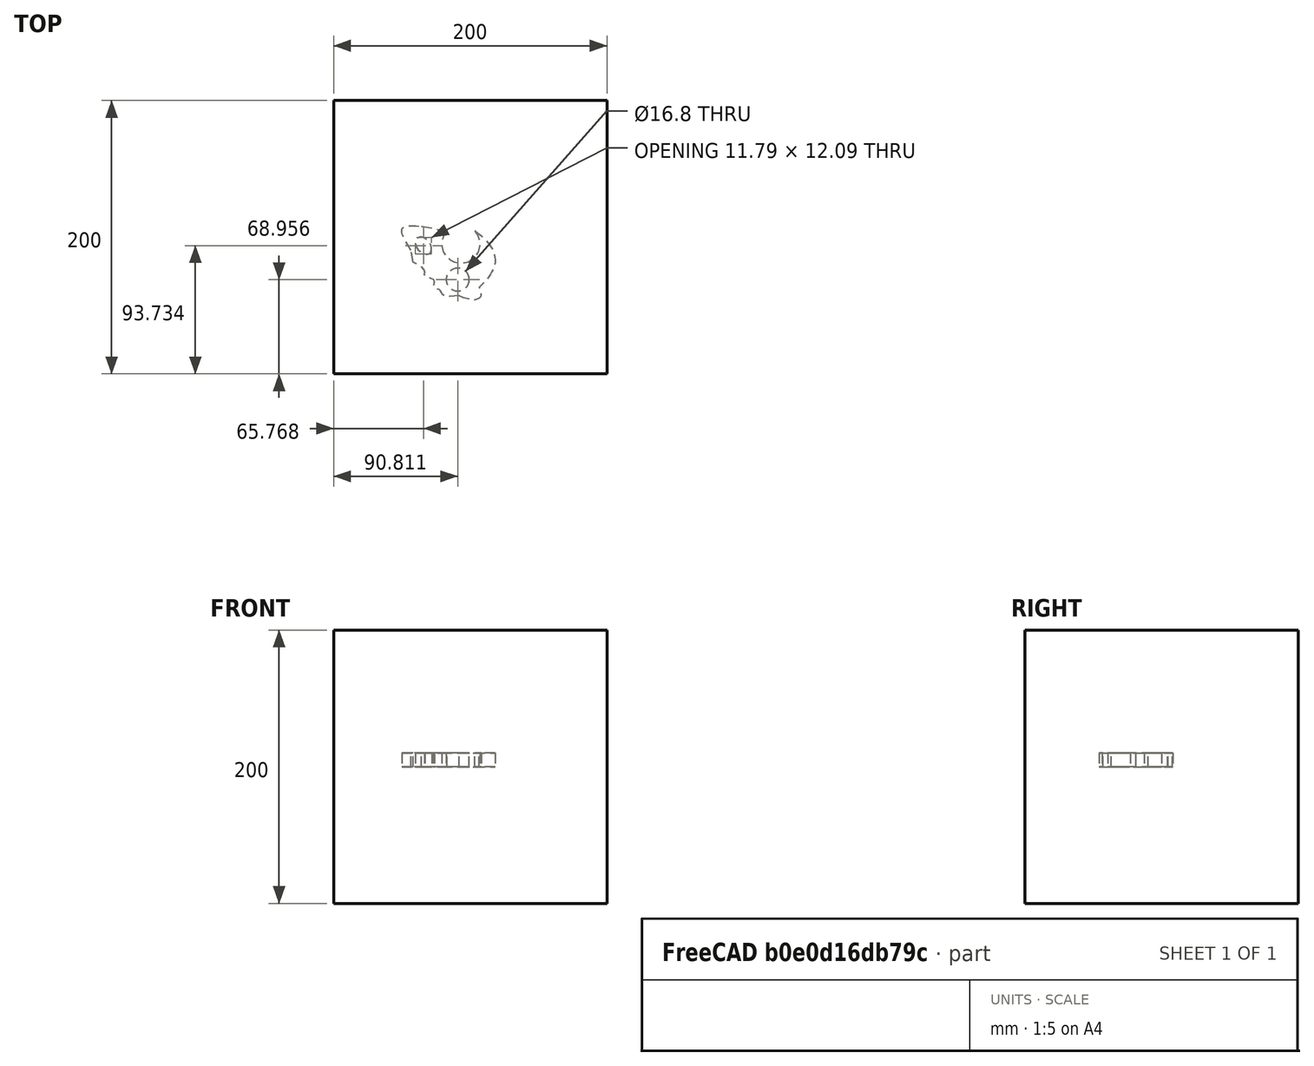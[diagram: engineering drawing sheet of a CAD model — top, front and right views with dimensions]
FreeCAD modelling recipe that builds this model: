
FCSTD DOCUMENT  (FreeCAD 1.0R39109 (Git))
Label: extrudeAllShapes
License: All rights reserved
LicenseURL: http://en.wikipedia.org/wiki/All_rights_reserved
objects: App::DocumentObjectGroupPython×1248, App::Part×2, Part::FeaturePython×1, Sketcher::SketchObject×1, Part::Extrusion×1
note: 4 computed .brp shape members not serialized (recipe doc carries the construction recipe); baked Part::Feature solids carry a one-line shape summary decoded from their .brp

FEATURE [App::DocumentObjectGroupPython] HALFPI  # scripted group (container) (typed FeaturePython)
  name = HALFPI
  value = pi/2.
FEATURE [App::DocumentObjectGroupPython] PI  # scripted group (container) (typed FeaturePython)
  name = PI
  value = 1.*pi
FEATURE [App::DocumentObjectGroupPython] TWOPI  # scripted group (container) (typed FeaturePython)
  name = TWOPI
  value = 2.*pi
FEATURE [App::DocumentObjectGroupPython] Constants  # scripted group (container) (typed FeaturePython)
  Group = -> [HALFPI,PI,TWOPI]
FEATURE [App::DocumentObjectGroupPython] Variables  # scripted group (container) (typed FeaturePython)
FEATURE [App::DocumentObjectGroupPython] Quantities  # scripted group (container) (typed FeaturePython)
FEATURE [App::DocumentObjectGroupPython] Isotopes  # scripted group (container) (typed FeaturePython)
FEATURE [App::DocumentObjectGroupPython] Elements  # scripted group (container) (typed FeaturePython)
FEATURE [App::DocumentObjectGroupPython] G4Isotopes  # scripted group (container) (typed FeaturePython)
FEATURE [App::DocumentObjectGroupPython] H_element  # scripted group (container) (typed FeaturePython)
  Z = 1
  atom_value = 1.008
  formula = H
  name = H_element
FEATURE [App::DocumentObjectGroupPython] He_element  # scripted group (container) (typed FeaturePython)
  Z = 2
  atom_value = 4.0026
  formula = He
  name = He_element
FEATURE [App::DocumentObjectGroupPython] Li_element  # scripted group (container) (typed FeaturePython)
  Z = 3
  atom_value = 6.94
  formula = Li
  name = Li_element
FEATURE [App::DocumentObjectGroupPython] Be_element  # scripted group (container) (typed FeaturePython)
  Z = 4
  atom_value = 9.01218
  formula = Be
  name = Be_element
FEATURE [App::DocumentObjectGroupPython] B_element  # scripted group (container) (typed FeaturePython)
  Z = 5
  atom_value = 10.81
  formula = B
  name = B_element
FEATURE [App::DocumentObjectGroupPython] C_element  # scripted group (container) (typed FeaturePython)
  Z = 6
  atom_value = 12.011
  formula = C
  name = C_element
FEATURE [App::DocumentObjectGroupPython] N_element  # scripted group (container) (typed FeaturePython)
  Z = 7
  atom_value = 14.007
  formula = N
  name = N_element
FEATURE [App::DocumentObjectGroupPython] O_element  # scripted group (container) (typed FeaturePython)
  Z = 8
  atom_value = 15.999
  formula = O
  name = O_element
FEATURE [App::DocumentObjectGroupPython] F_element  # scripted group (container) (typed FeaturePython)
  Z = 9
  atom_value = 18.9984
  formula = F
  name = F_element
FEATURE [App::DocumentObjectGroupPython] Ne_element  # scripted group (container) (typed FeaturePython)
  Z = 10
  atom_value = 20.1797
  formula = Ne
  name = Ne_element
FEATURE [App::DocumentObjectGroupPython] Na_element  # scripted group (container) (typed FeaturePython)
  Z = 11
  atom_value = 22.9898
  formula = Na
  name = Na_element
FEATURE [App::DocumentObjectGroupPython] Mg_element  # scripted group (container) (typed FeaturePython)
  Z = 12
  atom_value = 24.305
  formula = Mg
  name = Mg_element
FEATURE [App::DocumentObjectGroupPython] Al_element  # scripted group (container) (typed FeaturePython)
  Z = 13
  atom_value = 26.9815
  formula = Al
  name = Al_element
FEATURE [App::DocumentObjectGroupPython] Si_element  # scripted group (container) (typed FeaturePython)
  Z = 14
  atom_value = 28.085
  formula = Si
  name = Si_element
FEATURE [App::DocumentObjectGroupPython] P_element  # scripted group (container) (typed FeaturePython)
  Z = 15
  atom_value = 30.9738
  formula = P
  name = P_element
FEATURE [App::DocumentObjectGroupPython] S_element  # scripted group (container) (typed FeaturePython)
  Z = 16
  atom_value = 32.06
  formula = S
  name = S_element
FEATURE [App::DocumentObjectGroupPython] Cl_element  # scripted group (container) (typed FeaturePython)
  Z = 17
  atom_value = 35.45
  formula = Cl
  name = Cl_element
FEATURE [App::DocumentObjectGroupPython] Ar_element  # scripted group (container) (typed FeaturePython)
  Z = 18
  atom_value = 39.95
  formula = Ar
  name = Ar_element
FEATURE [App::DocumentObjectGroupPython] K_element  # scripted group (container) (typed FeaturePython)
  Z = 19
  atom_value = 39.0983
  formula = K
  name = K_element
FEATURE [App::DocumentObjectGroupPython] Ca_element  # scripted group (container) (typed FeaturePython)
  Z = 20
  atom_value = 40.078
  formula = Ca
  name = Ca_element
FEATURE [App::DocumentObjectGroupPython] Sc_element  # scripted group (container) (typed FeaturePython)
  Z = 21
  atom_value = 44.9559
  formula = Sc
  name = Sc_element
FEATURE [App::DocumentObjectGroupPython] Ti_element  # scripted group (container) (typed FeaturePython)
  Z = 22
  atom_value = 47.867
  formula = Ti
  name = Ti_element
FEATURE [App::DocumentObjectGroupPython] V_element  # scripted group (container) (typed FeaturePython)
  Z = 23
  atom_value = 50.9415
  formula = V
  name = V_element
FEATURE [App::DocumentObjectGroupPython] Cr_element  # scripted group (container) (typed FeaturePython)
  Z = 24
  atom_value = 51.9961
  formula = Cr
  name = Cr_element
FEATURE [App::DocumentObjectGroupPython] Mn_element  # scripted group (container) (typed FeaturePython)
  Z = 25
  atom_value = 54.938
  formula = Mn
  name = Mn_element
FEATURE [App::DocumentObjectGroupPython] Fe_element  # scripted group (container) (typed FeaturePython)
  Z = 26
  atom_value = 55.845
  formula = Fe
  name = Fe_element
FEATURE [App::DocumentObjectGroupPython] Co_element  # scripted group (container) (typed FeaturePython)
  Z = 27
  atom_value = 58.9332
  formula = Co
  name = Co_element
FEATURE [App::DocumentObjectGroupPython] Ni_element  # scripted group (container) (typed FeaturePython)
  Z = 28
  atom_value = 58.6934
  formula = Ni
  name = Ni_element
FEATURE [App::DocumentObjectGroupPython] Cu_element  # scripted group (container) (typed FeaturePython)
  Z = 29
  atom_value = 63.546
  formula = Cu
  name = Cu_element
FEATURE [App::DocumentObjectGroupPython] Zn_element  # scripted group (container) (typed FeaturePython)
  Z = 30
  atom_value = 65.38
  formula = Zn
  name = Zn_element
FEATURE [App::DocumentObjectGroupPython] Ga_element  # scripted group (container) (typed FeaturePython)
  Z = 31
  atom_value = 69.723
  formula = Ga
  name = Ga_element
FEATURE [App::DocumentObjectGroupPython] Ge_element  # scripted group (container) (typed FeaturePython)
  Z = 32
  atom_value = 72.63
  formula = Ge
  name = Ge_element
FEATURE [App::DocumentObjectGroupPython] As_element  # scripted group (container) (typed FeaturePython)
  Z = 33
  atom_value = 74.9216
  formula = As
  name = As_element
FEATURE [App::DocumentObjectGroupPython] Se_element  # scripted group (container) (typed FeaturePython)
  Z = 34
  atom_value = 78.971
  formula = Se
  name = Se_element
FEATURE [App::DocumentObjectGroupPython] Br_element  # scripted group (container) (typed FeaturePython)
  Z = 35
  atom_value = 79.904
  formula = Br
  name = Br_element
FEATURE [App::DocumentObjectGroupPython] Kr_element  # scripted group (container) (typed FeaturePython)
  Z = 36
  atom_value = 83.798
  formula = Kr
  name = Kr_element
FEATURE [App::DocumentObjectGroupPython] Rb_element  # scripted group (container) (typed FeaturePython)
  Z = 37
  atom_value = 85.4678
  formula = Rb
  name = Rb_element
FEATURE [App::DocumentObjectGroupPython] Sr_element  # scripted group (container) (typed FeaturePython)
  Z = 38
  atom_value = 87.62
  formula = Sr
  name = Sr_element
FEATURE [App::DocumentObjectGroupPython] Y_element  # scripted group (container) (typed FeaturePython)
  Z = 39
  atom_value = 88.9058
  formula = Y
  name = Y_element
FEATURE [App::DocumentObjectGroupPython] Zr_element  # scripted group (container) (typed FeaturePython)
  Z = 40
  atom_value = 91.224
  formula = Zr
  name = Zr_element
FEATURE [App::DocumentObjectGroupPython] Nb_element  # scripted group (container) (typed FeaturePython)
  Z = 41
  atom_value = 92.9064
  formula = Nb
  name = Nb_element
FEATURE [App::DocumentObjectGroupPython] Mo_element  # scripted group (container) (typed FeaturePython)
  Z = 42
  atom_value = 95.95
  formula = Mo
  name = Mo_element
FEATURE [App::DocumentObjectGroupPython] Tc_element  # scripted group (container) (typed FeaturePython)
  Z = 43
  atom_value = 97
  formula = Tc
  name = Tc_element
FEATURE [App::DocumentObjectGroupPython] Ru_element  # scripted group (container) (typed FeaturePython)
  Z = 44
  atom_value = 101.07
  formula = Ru
  name = Ru_element
FEATURE [App::DocumentObjectGroupPython] Rh_element  # scripted group (container) (typed FeaturePython)
  Z = 45
  atom_value = 102.905
  formula = Rh
  name = Rh_element
FEATURE [App::DocumentObjectGroupPython] Pd_element  # scripted group (container) (typed FeaturePython)
  Z = 46
  atom_value = 106.42
  formula = Pd
  name = Pd_element
FEATURE [App::DocumentObjectGroupPython] Ag_element  # scripted group (container) (typed FeaturePython)
  Z = 47
  atom_value = 107.868
  formula = Ag
  name = Ag_element
FEATURE [App::DocumentObjectGroupPython] Cd_element  # scripted group (container) (typed FeaturePython)
  Z = 48
  atom_value = 112.414
  formula = Cd
  name = Cd_element
FEATURE [App::DocumentObjectGroupPython] In_element  # scripted group (container) (typed FeaturePython)
  Z = 49
  atom_value = 114.818
  formula = In
  name = In_element
FEATURE [App::DocumentObjectGroupPython] Sn_element  # scripted group (container) (typed FeaturePython)
  Z = 50
  atom_value = 118.71
  formula = Sn
  name = Sn_element
FEATURE [App::DocumentObjectGroupPython] Sb_element  # scripted group (container) (typed FeaturePython)
  Z = 51
  atom_value = 121.76
  formula = Sb
  name = Sb_element
FEATURE [App::DocumentObjectGroupPython] Te_element  # scripted group (container) (typed FeaturePython)
  Z = 52
  atom_value = 127.6
  formula = Te
  name = Te_element
FEATURE [App::DocumentObjectGroupPython] I_element  # scripted group (container) (typed FeaturePython)
  Z = 53
  atom_value = 126.904
  formula = I
  name = I_element
FEATURE [App::DocumentObjectGroupPython] Xe_element  # scripted group (container) (typed FeaturePython)
  Z = 54
  atom_value = 131.293
  formula = Xe
  name = Xe_element
FEATURE [App::DocumentObjectGroupPython] Cs_element  # scripted group (container) (typed FeaturePython)
  Z = 55
  atom_value = 132.905
  formula = Cs
  name = Cs_element
FEATURE [App::DocumentObjectGroupPython] Ba_element  # scripted group (container) (typed FeaturePython)
  Z = 56
  atom_value = 137.327
  formula = Ba
  name = Ba_element
FEATURE [App::DocumentObjectGroupPython] La_element  # scripted group (container) (typed FeaturePython)
  Z = 57
  atom_value = 138.905
  formula = La
  name = La_element
FEATURE [App::DocumentObjectGroupPython] Ce_element  # scripted group (container) (typed FeaturePython)
  Z = 58
  atom_value = 140.116
  formula = Ce
  name = Ce_element
FEATURE [App::DocumentObjectGroupPython] Pr_element  # scripted group (container) (typed FeaturePython)
  Z = 59
  atom_value = 140.908
  formula = Pr
  name = Pr_element
FEATURE [App::DocumentObjectGroupPython] Nd_element  # scripted group (container) (typed FeaturePython)
  Z = 60
  atom_value = 144.242
  formula = Nd
  name = Nd_element
FEATURE [App::DocumentObjectGroupPython] Pm_element  # scripted group (container) (typed FeaturePython)
  Z = 61
  atom_value = 145
  formula = Pm
  name = Pm_element
FEATURE [App::DocumentObjectGroupPython] Sm_element  # scripted group (container) (typed FeaturePython)
  Z = 62
  atom_value = 150.36
  formula = Sm
  name = Sm_element
FEATURE [App::DocumentObjectGroupPython] Eu_element  # scripted group (container) (typed FeaturePython)
  Z = 63
  atom_value = 151.964
  formula = Eu
  name = Eu_element
FEATURE [App::DocumentObjectGroupPython] Gd_element  # scripted group (container) (typed FeaturePython)
  Z = 64
  atom_value = 157.25
  formula = Gd
  name = Gd_element
FEATURE [App::DocumentObjectGroupPython] Tb_element  # scripted group (container) (typed FeaturePython)
  Z = 65
  atom_value = 158.925
  formula = Tb
  name = Tb_element
FEATURE [App::DocumentObjectGroupPython] Dy_element  # scripted group (container) (typed FeaturePython)
  Z = 66
  atom_value = 162.5
  formula = Dy
  name = Dy_element
FEATURE [App::DocumentObjectGroupPython] Ho_element  # scripted group (container) (typed FeaturePython)
  Z = 67
  atom_value = 164.93
  formula = Ho
  name = Ho_element
FEATURE [App::DocumentObjectGroupPython] Er_element  # scripted group (container) (typed FeaturePython)
  Z = 68
  atom_value = 167.259
  formula = Er
  name = Er_element
FEATURE [App::DocumentObjectGroupPython] Tm_element  # scripted group (container) (typed FeaturePython)
  Z = 69
  atom_value = 168.934
  formula = Tm
  name = Tm_element
FEATURE [App::DocumentObjectGroupPython] Yb_element  # scripted group (container) (typed FeaturePython)
  Z = 70
  atom_value = 173.045
  formula = Yb
  name = Yb_element
FEATURE [App::DocumentObjectGroupPython] Lu_element  # scripted group (container) (typed FeaturePython)
  Z = 71
  atom_value = 174.967
  formula = Lu
  name = Lu_element
FEATURE [App::DocumentObjectGroupPython] Hf_element  # scripted group (container) (typed FeaturePython)
  Z = 72
  atom_value = 178.49
  formula = Hf
  name = Hf_element
FEATURE [App::DocumentObjectGroupPython] Ta_element  # scripted group (container) (typed FeaturePython)
  Z = 73
  atom_value = 180.948
  formula = Ta
  name = Ta_element
FEATURE [App::DocumentObjectGroupPython] W_element  # scripted group (container) (typed FeaturePython)
  Z = 74
  atom_value = 183.84
  formula = W
  name = W_element
FEATURE [App::DocumentObjectGroupPython] Re_element  # scripted group (container) (typed FeaturePython)
  Z = 75
  atom_value = 186.207
  formula = Re
  name = Re_element
FEATURE [App::DocumentObjectGroupPython] Os_element  # scripted group (container) (typed FeaturePython)
  Z = 76
  atom_value = 190.23
  formula = Os
  name = Os_element
FEATURE [App::DocumentObjectGroupPython] Ir_element  # scripted group (container) (typed FeaturePython)
  Z = 77
  atom_value = 192.217
  formula = Ir
  name = Ir_element
FEATURE [App::DocumentObjectGroupPython] Pt_element  # scripted group (container) (typed FeaturePython)
  Z = 78
  atom_value = 195.084
  formula = Pt
  name = Pt_element
FEATURE [App::DocumentObjectGroupPython] Au_element  # scripted group (container) (typed FeaturePython)
  Z = 79
  atom_value = 196.967
  formula = Au
  name = Au_element
FEATURE [App::DocumentObjectGroupPython] Hg_element  # scripted group (container) (typed FeaturePython)
  Z = 80
  atom_value = 200.592
  formula = Hg
  name = Hg_element
FEATURE [App::DocumentObjectGroupPython] Tl_element  # scripted group (container) (typed FeaturePython)
  Z = 81
  atom_value = 204.38
  formula = Tl
  name = Tl_element
FEATURE [App::DocumentObjectGroupPython] Pb_element  # scripted group (container) (typed FeaturePython)
  Z = 82
  atom_value = 207.2
  formula = Pb
  name = Pb_element
FEATURE [App::DocumentObjectGroupPython] Bi_element  # scripted group (container) (typed FeaturePython)
  Z = 83
  atom_value = 208.98
  formula = Bi
  name = Bi_element
FEATURE [App::DocumentObjectGroupPython] Po_element  # scripted group (container) (typed FeaturePython)
  Z = 84
  atom_value = 209
  formula = Po
  name = Po_element
FEATURE [App::DocumentObjectGroupPython] At_element  # scripted group (container) (typed FeaturePython)
  Z = 85
  atom_value = 210
  formula = At
  name = At_element
FEATURE [App::DocumentObjectGroupPython] Rn_element  # scripted group (container) (typed FeaturePython)
  Z = 86
  atom_value = 222
  formula = Rn
  name = Rn_element
FEATURE [App::DocumentObjectGroupPython] Fr_element  # scripted group (container) (typed FeaturePython)
  Z = 87
  atom_value = 223
  formula = Fr
  name = Fr_element
FEATURE [App::DocumentObjectGroupPython] Ra_element  # scripted group (container) (typed FeaturePython)
  Z = 88
  atom_value = 226
  formula = Ra
  name = Ra_element
FEATURE [App::DocumentObjectGroupPython] Ac_element  # scripted group (container) (typed FeaturePython)
  Z = 89
  atom_value = 227
  formula = Ac
  name = Ac_element
FEATURE [App::DocumentObjectGroupPython] Th_element  # scripted group (container) (typed FeaturePython)
  Z = 90
  atom_value = 232.038
  formula = Th
  name = Th_element
FEATURE [App::DocumentObjectGroupPython] Pa_element  # scripted group (container) (typed FeaturePython)
  Z = 91
  atom_value = 231.036
  formula = Pa
  name = Pa_element
FEATURE [App::DocumentObjectGroupPython] U_element  # scripted group (container) (typed FeaturePython)
  Z = 92
  atom_value = 238.029
  formula = U
  name = U_element
FEATURE [App::DocumentObjectGroupPython] Np_element  # scripted group (container) (typed FeaturePython)
  Z = 93
  atom_value = 237
  formula = Np
  name = Np_element
FEATURE [App::DocumentObjectGroupPython] Pu_element  # scripted group (container) (typed FeaturePython)
  Z = 94
  atom_value = 244
  formula = Pu
  name = Pu_element
FEATURE [App::DocumentObjectGroupPython] Am_element  # scripted group (container) (typed FeaturePython)
  Z = 95
  atom_value = 243
  formula = Am
  name = Am_element
FEATURE [App::DocumentObjectGroupPython] Cm_element  # scripted group (container) (typed FeaturePython)
  Z = 96
  atom_value = 247
  formula = Cm
  name = Cm_element
FEATURE [App::DocumentObjectGroupPython] Bk_element  # scripted group (container) (typed FeaturePython)
  Z = 97
  atom_value = 247
  formula = Bk
  name = Bk_element
FEATURE [App::DocumentObjectGroupPython] Cf_element  # scripted group (container) (typed FeaturePython)
  Z = 98
  atom_value = 251
  formula = Cf
  name = Cf_element
FEATURE [App::DocumentObjectGroupPython] G4Elements  # scripted group (container) (typed FeaturePython)
  Group = -> [H_element,He_element,Li_element,Be_element,B_element,C_element,N_element,O_element,F_element,Ne_element,Na_element,Mg_element,Al_element,Si_element,P_element,S_element,Cl_element,Ar_element,K_element,Ca_element,Sc_element,Ti_element,V_element,Cr_element,Mn_element,Fe_element,Co_element,Ni_element,Cu_element,Zn_element,Ga_element,Ge_element,As_element,Se_element,Br_element,Kr_element,Rb_element,+61 more]
FEATURE [App::DocumentObjectGroupPython] H_element001  label="H_element : 0.101"  # scripted group (container) (typed FeaturePython)
  n = 0.101327
FEATURE [App::DocumentObjectGroupPython] C_element001  label="C_element : 0.775"  # scripted group (container) (typed FeaturePython)
  n = 0.7755
FEATURE [App::DocumentObjectGroupPython] N_element001  label="N_element : 0.035"  # scripted group (container) (typed FeaturePython)
  n = 0.035057
FEATURE [App::DocumentObjectGroupPython] O_element001  label="O_element : 0.052"  # scripted group (container) (typed FeaturePython)
  n = 0.0523159
FEATURE [App::DocumentObjectGroupPython] F_element001  label="F_element : 0.017"  # scripted group (container) (typed FeaturePython)
  n = 0.017422
FEATURE [App::DocumentObjectGroupPython] Ca_element001  label="Ca_element : 0.018"  # scripted group (container) (typed FeaturePython)
  n = 0.018378
FEATURE [App::DocumentObjectGroupPython] G4_A_150_TISSUE  label="G4_A-150_TISSUE"  # scripted group (container) (typed FeaturePython)
  Dunit = g/cm3
  Dvalue = 1.127
  Group = -> [H_element001,C_element001,N_element001,O_element001,F_element001,Ca_element001]
  conduct = 2
  density = 1
  expand = 3
  formula = G4_A-150_TISSUE
  name = G4_A-150_TISSUE
  specific = 4
FEATURE [App::DocumentObjectGroupPython] C_element002  label="C_element : 3"  # scripted group (container) (typed FeaturePython)
  n = 3
  ref = C_element
FEATURE [App::DocumentObjectGroupPython] H_element002  label="H_element : 6"  # scripted group (container) (typed FeaturePython)
  n = 6
  ref = H_element
FEATURE [App::DocumentObjectGroupPython] O_element002  label="O_element : 1"  # scripted group (container) (typed FeaturePython)
  n = 1
  ref = O_element
FEATURE [App::DocumentObjectGroupPython] G4_ACETONE  # scripted group (container) (typed FeaturePython)
  Dunit = g/cm3
  Dvalue = 0.7899
  Group = -> [C_element002,H_element002,O_element002]
  conduct = 2
  density = 1
  expand = 3
  formula = G4_ACETONE
  name = G4_ACETONE
  specific = 4
FEATURE [App::DocumentObjectGroupPython] C_element003  label="C_element : 2"  # scripted group (container) (typed FeaturePython)
  n = 2
  ref = C_element
FEATURE [App::DocumentObjectGroupPython] H_element003  label="H_element : 2"  # scripted group (container) (typed FeaturePython)
  n = 2
  ref = H_element
FEATURE [App::DocumentObjectGroupPython] G4_ACETYLENE  # scripted group (container) (typed FeaturePython)
  Dunit = g/cm3
  Dvalue = 0.0010967
  Group = -> [C_element003,H_element003]
  conduct = 2
  density = 1
  expand = 3
  formula = G4_ACETYLENE
  name = G4_ACETYLENE
  specific = 4
FEATURE [App::DocumentObjectGroupPython] C_element004  label="C_element : 5"  # scripted group (container) (typed FeaturePython)
  n = 5
  ref = C_element
FEATURE [App::DocumentObjectGroupPython] H_element004  label="H_element : 5"  # scripted group (container) (typed FeaturePython)
  n = 5
  ref = H_element
FEATURE [App::DocumentObjectGroupPython] N_element002  label="N_element : 5"  # scripted group (container) (typed FeaturePython)
  n = 5
  ref = N_element
FEATURE [App::DocumentObjectGroupPython] G4_ADENINE  # scripted group (container) (typed FeaturePython)
  Dunit = g/cm3
  Dvalue = 1.6
  Group = -> [C_element004,H_element004,N_element002]
  conduct = 2
  density = 1
  expand = 3
  formula = G4_ADENINE
  name = G4_ADENINE
  specific = 4
FEATURE [App::DocumentObjectGroupPython] H_element005  label="H_element : 0.114"  # scripted group (container) (typed FeaturePython)
  n = 0.114
FEATURE [App::DocumentObjectGroupPython] C_element005  label="C_element : 0.598"  # scripted group (container) (typed FeaturePython)
  n = 0.598
FEATURE [App::DocumentObjectGroupPython] N_element003  label="N_element : 0.007"  # scripted group (container) (typed FeaturePython)
  n = 0.007
FEATURE [App::DocumentObjectGroupPython] O_element003  label="O_element : 0.278"  # scripted group (container) (typed FeaturePython)
  n = 0.278
FEATURE [App::DocumentObjectGroupPython] Na_element001  label="Na_element : 0.001"  # scripted group (container) (typed FeaturePython)
  n = 0.001
FEATURE [App::DocumentObjectGroupPython] S_element001  label="S_element : 0.001"  # scripted group (container) (typed FeaturePython)
  n = 0.001
FEATURE [App::DocumentObjectGroupPython] Cl_element001  label="Cl_element : 0.001"  # scripted group (container) (typed FeaturePython)
  n = 0.001
FEATURE [App::DocumentObjectGroupPython] G4_ADIPOSE_TISSUE_ICRP  # scripted group (container) (typed FeaturePython)
  Dunit = g/cm3
  Dvalue = 0.95
  Group = -> [H_element005,C_element005,N_element003,O_element003,Na_element001,S_element001,Cl_element001]
  conduct = 2
  density = 1
  expand = 3
  formula = G4_ADIPOSE_TISSUE_ICRP
  name = G4_ADIPOSE_TISSUE_ICRP
  specific = 4
FEATURE [App::DocumentObjectGroupPython] C_element006  label="C_element : 0.000"  # scripted group (container) (typed FeaturePython)
  n = 0.000124
FEATURE [App::DocumentObjectGroupPython] N_element004  label="N_element : 0.755"  # scripted group (container) (typed FeaturePython)
  n = 0.755268
FEATURE [App::DocumentObjectGroupPython] O_element004  label="O_element : 0.232"  # scripted group (container) (typed FeaturePython)
  n = 0.231781
FEATURE [App::DocumentObjectGroupPython] Ar_element001  label="Ar_element : 0.013"  # scripted group (container) (typed FeaturePython)
  n = 0.012827
FEATURE [App::DocumentObjectGroupPython] G4_AIR  # scripted group (container) (typed FeaturePython)
  Dunit = g/cm3
  Dvalue = 0.00120479
  Group = -> [C_element006,N_element004,O_element004,Ar_element001]
  conduct = 2
  density = 1
  expand = 3
  formula = G4_AIR
  name = G4_AIR
  specific = 4
FEATURE [App::DocumentObjectGroupPython] C_element007  label="C_element : 006"  # scripted group (container) (typed FeaturePython)
  n = 3
  ref = C_element
FEATURE [App::DocumentObjectGroupPython] H_element006  label="H_element : 7"  # scripted group (container) (typed FeaturePython)
  n = 7
  ref = H_element
FEATURE [App::DocumentObjectGroupPython] N_element005  label="N_element : 1"  # scripted group (container) (typed FeaturePython)
  n = 1
  ref = N_element
FEATURE [App::DocumentObjectGroupPython] O_element005  label="O_element : 2"  # scripted group (container) (typed FeaturePython)
  n = 2
  ref = O_element
FEATURE [App::DocumentObjectGroupPython] G4_ALANINE  # scripted group (container) (typed FeaturePython)
  Dunit = g/cm3
  Dvalue = 1.42
  Group = -> [C_element007,H_element006,N_element005,O_element005]
  conduct = 2
  density = 1
  expand = 3
  formula = G4_ALANINE
  name = G4_ALANINE
  specific = 4
FEATURE [App::DocumentObjectGroupPython] Al_element001  label="Al_element : 2"  # scripted group (container) (typed FeaturePython)
  n = 2
  ref = Al_element
FEATURE [App::DocumentObjectGroupPython] O_element006  label="O_element : 3"  # scripted group (container) (typed FeaturePython)
  n = 3
  ref = O_element
FEATURE [App::DocumentObjectGroupPython] G4_ALUMINUM_OXIDE  # scripted group (container) (typed FeaturePython)
  Dunit = g/cm3
  Dvalue = 3.97
  Group = -> [Al_element001,O_element006]
  conduct = 2
  density = 1
  expand = 3
  formula = G4_ALUMINUM_OXIDE
  name = G4_ALUMINUM_OXIDE
  specific = 4
FEATURE [App::DocumentObjectGroupPython] H_element007  label="H_element : 0.106"  # scripted group (container) (typed FeaturePython)
  n = 0.10593
FEATURE [App::DocumentObjectGroupPython] C_element008  label="C_element : 0.789"  # scripted group (container) (typed FeaturePython)
  n = 0.788974
FEATURE [App::DocumentObjectGroupPython] O_element007  label="O_element : 0.105"  # scripted group (container) (typed FeaturePython)
  n = 0.105096
FEATURE [App::DocumentObjectGroupPython] G4_AMBER  # scripted group (container) (typed FeaturePython)
  Dunit = g/cm3
  Dvalue = 1.1
  Group = -> [H_element007,C_element008,O_element007]
  conduct = 2
  density = 1
  expand = 3
  formula = G4_AMBER
  name = G4_AMBER
  specific = 4
FEATURE [App::DocumentObjectGroupPython] N_element006  label="N_element : 006"  # scripted group (container) (typed FeaturePython)
  n = 1
  ref = N_element
FEATURE [App::DocumentObjectGroupPython] H_element008  label="H_element : 3"  # scripted group (container) (typed FeaturePython)
  n = 3
  ref = H_element
FEATURE [App::DocumentObjectGroupPython] G4_AMMONIA  # scripted group (container) (typed FeaturePython)
  Dunit = g/cm3
  Dvalue = 0.000826019
  Group = -> [N_element006,H_element008]
  conduct = 2
  density = 1
  expand = 3
  formula = G4_AMMONIA
  name = G4_AMMONIA
  specific = 4
FEATURE [App::DocumentObjectGroupPython] C_element009  label="C_element : 6"  # scripted group (container) (typed FeaturePython)
  n = 6
  ref = C_element
FEATURE [App::DocumentObjectGroupPython] H_element009  label="H_element : 008"  # scripted group (container) (typed FeaturePython)
  n = 7
  ref = H_element
FEATURE [App::DocumentObjectGroupPython] N_element007  label="N_element : 007"  # scripted group (container) (typed FeaturePython)
  n = 1
  ref = N_element
FEATURE [App::DocumentObjectGroupPython] G4_ANILINE  # scripted group (container) (typed FeaturePython)
  Dunit = g/cm3
  Dvalue = 1.0235
  Group = -> [C_element009,H_element009,N_element007]
  conduct = 2
  density = 1
  expand = 3
  formula = G4_ANILINE
  name = G4_ANILINE
  specific = 4
FEATURE [App::DocumentObjectGroupPython] C_element010  label="C_element : 14"  # scripted group (container) (typed FeaturePython)
  n = 14
  ref = C_element
FEATURE [App::DocumentObjectGroupPython] H_element010  label="H_element : 10"  # scripted group (container) (typed FeaturePython)
  n = 10
  ref = H_element
FEATURE [App::DocumentObjectGroupPython] G4_ANTHRACENE  # scripted group (container) (typed FeaturePython)
  Dunit = g/cm3
  Dvalue = 1.283
  Group = -> [C_element010,H_element010]
  conduct = 2
  density = 1
  expand = 3
  formula = G4_ANTHRACENE
  name = G4_ANTHRACENE
  specific = 4
FEATURE [App::DocumentObjectGroupPython] H_element011  label="H_element : 0.065"  # scripted group (container) (typed FeaturePython)
  n = 0.0654709
FEATURE [App::DocumentObjectGroupPython] C_element011  label="C_element : 0.537"  # scripted group (container) (typed FeaturePython)
  n = 0.536944
FEATURE [App::DocumentObjectGroupPython] N_element008  label="N_element : 0.021"  # scripted group (container) (typed FeaturePython)
  n = 0.0215
FEATURE [App::DocumentObjectGroupPython] O_element008  label="O_element : 0.032"  # scripted group (container) (typed FeaturePython)
  n = 0.032085
FEATURE [App::DocumentObjectGroupPython] F_element002  label="F_element : 0.167"  # scripted group (container) (typed FeaturePython)
  n = 0.167411
FEATURE [App::DocumentObjectGroupPython] Ca_element002  label="Ca_element : 0.177"  # scripted group (container) (typed FeaturePython)
  n = 0.176589
FEATURE [App::DocumentObjectGroupPython] G4_B_100_BONE  label="G4_B-100_BONE"  # scripted group (container) (typed FeaturePython)
  Dunit = g/cm3
  Dvalue = 1.45
  Group = -> [H_element011,C_element011,N_element008,O_element008,F_element002,Ca_element002]
  conduct = 2
  density = 1
  expand = 3
  formula = G4_B-100_BONE
  name = G4_B-100_BONE
  specific = 4
FEATURE [App::DocumentObjectGroupPython] H_element012  label="H_element : 0.057"  # scripted group (container) (typed FeaturePython)
  n = 0.057441
FEATURE [App::DocumentObjectGroupPython] C_element012  label="C_element : 0.790"  # scripted group (container) (typed FeaturePython)
  n = 0.774591
FEATURE [App::DocumentObjectGroupPython] O_element009  label="O_element : 0.168"  # scripted group (container) (typed FeaturePython)
  n = 0.167968
FEATURE [App::DocumentObjectGroupPython] G4_BAKELITE  # scripted group (container) (typed FeaturePython)
  Dunit = g/cm3
  Dvalue = 1.25
  Group = -> [H_element012,C_element012,O_element009]
  conduct = 2
  density = 1
  expand = 3
  formula = G4_BAKELITE
  name = G4_BAKELITE
  specific = 4
FEATURE [App::DocumentObjectGroupPython] Ba_element001  label="Ba_element : 1"  # scripted group (container) (typed FeaturePython)
  n = 1
  ref = Ba_element
FEATURE [App::DocumentObjectGroupPython] F_element003  label="F_element : 2"  # scripted group (container) (typed FeaturePython)
  n = 2
  ref = F_element
FEATURE [App::DocumentObjectGroupPython] G4_BARIUM_FLUORIDE  # scripted group (container) (typed FeaturePython)
  Dunit = g/cm3
  Dvalue = 4.89
  Group = -> [Ba_element001,F_element003]
  conduct = 2
  density = 1
  expand = 3
  formula = G4_BARIUM_FLUORIDE
  name = G4_BARIUM_FLUORIDE
  specific = 4
FEATURE [App::DocumentObjectGroupPython] Ba_element002  label="Ba_element : 002"  # scripted group (container) (typed FeaturePython)
  n = 1
  ref = Ba_element
FEATURE [App::DocumentObjectGroupPython] S_element002  label="S_element : 1"  # scripted group (container) (typed FeaturePython)
  n = 1
  ref = S_element
FEATURE [App::DocumentObjectGroupPython] O_element010  label="O_element : 4"  # scripted group (container) (typed FeaturePython)
  n = 4
  ref = O_element
FEATURE [App::DocumentObjectGroupPython] G4_BARIUM_SULFATE  # scripted group (container) (typed FeaturePython)
  Dunit = g/cm3
  Dvalue = 4.5
  Group = -> [Ba_element002,S_element002,O_element010]
  conduct = 2
  density = 1
  expand = 3
  formula = G4_BARIUM_SULFATE
  name = G4_BARIUM_SULFATE
  specific = 4
FEATURE [App::DocumentObjectGroupPython] C_element013  label="C_element : 007"  # scripted group (container) (typed FeaturePython)
  n = 6
  ref = C_element
FEATURE [App::DocumentObjectGroupPython] H_element013  label="H_element : 009"  # scripted group (container) (typed FeaturePython)
  n = 6
  ref = H_element
FEATURE [App::DocumentObjectGroupPython] G4_BENZENE  # scripted group (container) (typed FeaturePython)
  Dunit = g/cm3
  Dvalue = 0.87865
  Group = -> [C_element013,H_element013]
  conduct = 2
  density = 1
  expand = 3
  formula = G4_BENZENE
  name = G4_BENZENE
  specific = 4
FEATURE [App::DocumentObjectGroupPython] Be_element001  label="Be_element : 1"  # scripted group (container) (typed FeaturePython)
  n = 1
  ref = Be_element
FEATURE [App::DocumentObjectGroupPython] O_element011  label="O_element : 005"  # scripted group (container) (typed FeaturePython)
  n = 1
  ref = O_element
FEATURE [App::DocumentObjectGroupPython] G4_BERYLLIUM_OXIDE  # scripted group (container) (typed FeaturePython)
  Dunit = g/cm3
  Dvalue = 3.01
  Group = -> [Be_element001,O_element011]
  conduct = 2
  density = 1
  expand = 3
  formula = G4_BERYLLIUM_OXIDE
  name = G4_BERYLLIUM_OXIDE
  specific = 4
FEATURE [App::DocumentObjectGroupPython] Bi_element001  label="Bi_element : 4"  # scripted group (container) (typed FeaturePython)
  n = 4
  ref = Bi_element
FEATURE [App::DocumentObjectGroupPython] Ge_element001  label="Ge_element : 3"  # scripted group (container) (typed FeaturePython)
  n = 3
  ref = Ge_element
FEATURE [App::DocumentObjectGroupPython] O_element012  label="O_element : 12"  # scripted group (container) (typed FeaturePython)
  n = 12
  ref = O_element
FEATURE [App::DocumentObjectGroupPython] G4_BGO  # scripted group (container) (typed FeaturePython)
  Dunit = g/cm3
  Dvalue = 7.13
  Group = -> [Bi_element001,Ge_element001,O_element012]
  conduct = 2
  density = 1
  expand = 3
  formula = G4_BGO
  name = G4_BGO
  specific = 4
FEATURE [App::DocumentObjectGroupPython] H_element014  label="H_element : 0.102"  # scripted group (container) (typed FeaturePython)
  n = 0.102
FEATURE [App::DocumentObjectGroupPython] C_element014  label="C_element : 0.110"  # scripted group (container) (typed FeaturePython)
  n = 0.11
FEATURE [App::DocumentObjectGroupPython] N_element009  label="N_element : 0.033"  # scripted group (container) (typed FeaturePython)
  n = 0.033
FEATURE [App::DocumentObjectGroupPython] O_element013  label="O_element : 0.745"  # scripted group (container) (typed FeaturePython)
  n = 0.745
FEATURE [App::DocumentObjectGroupPython] Na_element002  label="Na_element : 0.002"  # scripted group (container) (typed FeaturePython)
  n = 0.001
FEATURE [App::DocumentObjectGroupPython] P_element001  label="P_element : 0.001"  # scripted group (container) (typed FeaturePython)
  n = 0.001
FEATURE [App::DocumentObjectGroupPython] S_element003  label="S_element : 0.002"  # scripted group (container) (typed FeaturePython)
  n = 0.002
FEATURE [App::DocumentObjectGroupPython] Cl_element002  label="Cl_element : 0.003"  # scripted group (container) (typed FeaturePython)
  n = 0.003
FEATURE [App::DocumentObjectGroupPython] K_element001  label="K_element : 0.002"  # scripted group (container) (typed FeaturePython)
  n = 0.002
FEATURE [App::DocumentObjectGroupPython] Fe_element001  label="Fe_element : 0.001"  # scripted group (container) (typed FeaturePython)
  n = 0.001
FEATURE [App::DocumentObjectGroupPython] G4_BLOOD_ICRP  # scripted group (container) (typed FeaturePython)
  Dunit = g/cm3
  Dvalue = 1.06
  Group = -> [H_element014,C_element014,N_element009,O_element013,Na_element002,P_element001,S_element003,Cl_element002,K_element001,Fe_element001]
  conduct = 2
  density = 1
  expand = 3
  formula = G4_BLOOD_ICRP
  name = G4_BLOOD_ICRP
  specific = 4
FEATURE [App::DocumentObjectGroupPython] H_element015  label="H_element : 0.064"  # scripted group (container) (typed FeaturePython)
  n = 0.064
FEATURE [App::DocumentObjectGroupPython] C_element015  label="C_element : 0.278"  # scripted group (container) (typed FeaturePython)
  n = 0.278
FEATURE [App::DocumentObjectGroupPython] N_element010  label="N_element : 0.027"  # scripted group (container) (typed FeaturePython)
  n = 0.027
FEATURE [App::DocumentObjectGroupPython] O_element014  label="O_element : 0.410"  # scripted group (container) (typed FeaturePython)
  n = 0.41
FEATURE [App::DocumentObjectGroupPython] Mg_element001  label="Mg_element : 0.002"  # scripted group (container) (typed FeaturePython)
  n = 0.002
FEATURE [App::DocumentObjectGroupPython] P_element002  label="P_element : 0.070"  # scripted group (container) (typed FeaturePython)
  n = 0.07
FEATURE [App::DocumentObjectGroupPython] S_element004  label="S_element : 0.003"  # scripted group (container) (typed FeaturePython)
  n = 0.002
FEATURE [App::DocumentObjectGroupPython] Ca_element003  label="Ca_element : 0.147"  # scripted group (container) (typed FeaturePython)
  n = 0.147
FEATURE [App::DocumentObjectGroupPython] G4_BONE_COMPACT_ICRU  # scripted group (container) (typed FeaturePython)
  Dunit = g/cm3
  Dvalue = 1.85
  Group = -> [H_element015,C_element015,N_element010,O_element014,Mg_element001,P_element002,S_element004,Ca_element003]
  conduct = 2
  density = 1
  expand = 3
  formula = G4_BONE_COMPACT_ICRU
  name = G4_BONE_COMPACT_ICRU
  specific = 4
FEATURE [App::DocumentObjectGroupPython] H_element016  label="H_element : 0.034"  # scripted group (container) (typed FeaturePython)
  n = 0.034
FEATURE [App::DocumentObjectGroupPython] C_element016  label="C_element : 0.155"  # scripted group (container) (typed FeaturePython)
  n = 0.155
FEATURE [App::DocumentObjectGroupPython] N_element011  label="N_element : 0.042"  # scripted group (container) (typed FeaturePython)
  n = 0.042
FEATURE [App::DocumentObjectGroupPython] O_element015  label="O_element : 0.435"  # scripted group (container) (typed FeaturePython)
  n = 0.435
FEATURE [App::DocumentObjectGroupPython] Na_element003  label="Na_element : 0.003"  # scripted group (container) (typed FeaturePython)
  n = 0.001
FEATURE [App::DocumentObjectGroupPython] Mg_element002  label="Mg_element : 0.003"  # scripted group (container) (typed FeaturePython)
  n = 0.002
FEATURE [App::DocumentObjectGroupPython] P_element003  label="P_element : 0.103"  # scripted group (container) (typed FeaturePython)
  n = 0.103
FEATURE [App::DocumentObjectGroupPython] S_element005  label="S_element : 0.004"  # scripted group (container) (typed FeaturePython)
  n = 0.003
FEATURE [App::DocumentObjectGroupPython] Ca_element004  label="Ca_element : 0.225"  # scripted group (container) (typed FeaturePython)
  n = 0.225
FEATURE [App::DocumentObjectGroupPython] G4_BONE_CORTICAL_ICRP  # scripted group (container) (typed FeaturePython)
  Dunit = g/cm3
  Dvalue = 1.92
  Group = -> [H_element016,C_element016,N_element011,O_element015,Na_element003,Mg_element002,P_element003,S_element005,Ca_element004]
  conduct = 2
  density = 1
  expand = 3
  formula = G4_BONE_CORTICAL_ICRP
  name = G4_BONE_CORTICAL_ICRP
  specific = 4
FEATURE [App::DocumentObjectGroupPython] B_element001  label="B_element : 4"  # scripted group (container) (typed FeaturePython)
  n = 4
  ref = B_element
FEATURE [App::DocumentObjectGroupPython] C_element017  label="C_element : 1"  # scripted group (container) (typed FeaturePython)
  n = 1
  ref = C_element
FEATURE [App::DocumentObjectGroupPython] G4_BORON_CARBIDE  # scripted group (container) (typed FeaturePython)
  Dunit = g/cm3
  Dvalue = 2.52
  Group = -> [B_element001,C_element017]
  conduct = 2
  density = 1
  expand = 3
  formula = G4_BORON_CARBIDE
  name = G4_BORON_CARBIDE
  specific = 4
FEATURE [App::DocumentObjectGroupPython] B_element002  label="B_element : 2"  # scripted group (container) (typed FeaturePython)
  n = 2
  ref = B_element
FEATURE [App::DocumentObjectGroupPython] O_element016  label="O_element : 006"  # scripted group (container) (typed FeaturePython)
  n = 3
  ref = O_element
FEATURE [App::DocumentObjectGroupPython] G4_BORON_OXIDE  # scripted group (container) (typed FeaturePython)
  Dunit = g/cm3
  Dvalue = 1.812
  Group = -> [B_element002,O_element016]
  conduct = 2
  density = 1
  expand = 3
  formula = G4_BORON_OXIDE
  name = G4_BORON_OXIDE
  specific = 4
FEATURE [App::DocumentObjectGroupPython] H_element017  label="H_element : 0.107"  # scripted group (container) (typed FeaturePython)
  n = 0.107
FEATURE [App::DocumentObjectGroupPython] C_element018  label="C_element : 0.145"  # scripted group (container) (typed FeaturePython)
  n = 0.145
FEATURE [App::DocumentObjectGroupPython] N_element012  label="N_element : 0.022"  # scripted group (container) (typed FeaturePython)
  n = 0.022
FEATURE [App::DocumentObjectGroupPython] O_element017  label="O_element : 0.712"  # scripted group (container) (typed FeaturePython)
  n = 0.712
FEATURE [App::DocumentObjectGroupPython] Na_element004  label="Na_element : 0.004"  # scripted group (container) (typed FeaturePython)
  n = 0.002
FEATURE [App::DocumentObjectGroupPython] P_element004  label="P_element : 0.004"  # scripted group (container) (typed FeaturePython)
  n = 0.004
FEATURE [App::DocumentObjectGroupPython] S_element006  label="S_element : 0.005"  # scripted group (container) (typed FeaturePython)
  n = 0.002
FEATURE [App::DocumentObjectGroupPython] Cl_element003  label="Cl_element : 0.004"  # scripted group (container) (typed FeaturePython)
  n = 0.003
FEATURE [App::DocumentObjectGroupPython] K_element002  label="K_element : 0.003"  # scripted group (container) (typed FeaturePython)
  n = 0.003
FEATURE [App::DocumentObjectGroupPython] G4_BRAIN_ICRP  # scripted group (container) (typed FeaturePython)
  Dunit = g/cm3
  Dvalue = 1.04
  Group = -> [H_element017,C_element018,N_element012,O_element017,Na_element004,P_element004,S_element006,Cl_element003,K_element002]
  conduct = 2
  density = 1
  expand = 3
  formula = G4_BRAIN_ICRP
  name = G4_BRAIN_ICRP
  specific = 4
FEATURE [App::DocumentObjectGroupPython] C_element019  label="C_element : 4"  # scripted group (container) (typed FeaturePython)
  n = 4
  ref = C_element
FEATURE [App::DocumentObjectGroupPython] H_element018  label="H_element : 010"  # scripted group (container) (typed FeaturePython)
  n = 10
  ref = H_element
FEATURE [App::DocumentObjectGroupPython] G4_BUTANE  # scripted group (container) (typed FeaturePython)
  Dunit = g/cm3
  Dvalue = 0.00249343
  Group = -> [C_element019,H_element018]
  conduct = 2
  density = 1
  expand = 3
  formula = G4_BUTANE
  name = G4_BUTANE
  specific = 4
FEATURE [App::DocumentObjectGroupPython] C_element020  label="C_element : 008"  # scripted group (container) (typed FeaturePython)
  n = 4
  ref = C_element
FEATURE [App::DocumentObjectGroupPython] H_element019  label="H_element : 011"  # scripted group (container) (typed FeaturePython)
  n = 10
  ref = H_element
FEATURE [App::DocumentObjectGroupPython] O_element018  label="O_element : 007"  # scripted group (container) (typed FeaturePython)
  n = 1
  ref = O_element
FEATURE [App::DocumentObjectGroupPython] G4_N_BUTYL_ALCOHOL  label="G4_N-BUTYL_ALCOHOL"  # scripted group (container) (typed FeaturePython)
  Dunit = g/cm3
  Dvalue = 0.8098
  Group = -> [C_element020,H_element019,O_element018]
  conduct = 2
  density = 1
  expand = 3
  formula = G4_N-BUTYL_ALCOHOL
  name = G4_N-BUTYL_ALCOHOL
  specific = 4
FEATURE [App::DocumentObjectGroupPython] H_element020  label="H_element : 0.025"  # scripted group (container) (typed FeaturePython)
  n = 0.02468
FEATURE [App::DocumentObjectGroupPython] C_element021  label="C_element : 0.502"  # scripted group (container) (typed FeaturePython)
  n = 0.501611
FEATURE [App::DocumentObjectGroupPython] O_element019  label="O_element : 0.005"  # scripted group (container) (typed FeaturePython)
  n = 0.004527
FEATURE [App::DocumentObjectGroupPython] F_element004  label="F_element : 0.465"  # scripted group (container) (typed FeaturePython)
  n = 0.465209
FEATURE [App::DocumentObjectGroupPython] Si_element001  label="Si_element : 0.004"  # scripted group (container) (typed FeaturePython)
  n = 0.003973
FEATURE [App::DocumentObjectGroupPython] G4_C_552  label="G4_C-552"  # scripted group (container) (typed FeaturePython)
  Dunit = g/cm3
  Dvalue = 1.76
  Group = -> [H_element020,C_element021,O_element019,F_element004,Si_element001]
  conduct = 2
  density = 1
  expand = 3
  formula = G4_C-552
  name = G4_C-552
  specific = 4
FEATURE [App::DocumentObjectGroupPython] Cd_element001  label="Cd_element : 1"  # scripted group (container) (typed FeaturePython)
  n = 1
  ref = Cd_element
FEATURE [App::DocumentObjectGroupPython] Te_element001  label="Te_element : 1"  # scripted group (container) (typed FeaturePython)
  n = 1
  ref = Te_element
FEATURE [App::DocumentObjectGroupPython] G4_CADMIUM_TELLURIDE  # scripted group (container) (typed FeaturePython)
  Dunit = g/cm3
  Dvalue = 6.2
  Group = -> [Cd_element001,Te_element001]
  conduct = 2
  density = 1
  expand = 3
  formula = G4_CADMIUM_TELLURIDE
  name = G4_CADMIUM_TELLURIDE
  specific = 4
FEATURE [App::DocumentObjectGroupPython] Cd_element002  label="Cd_element : 002"  # scripted group (container) (typed FeaturePython)
  n = 1
  ref = Cd_element
FEATURE [App::DocumentObjectGroupPython] W_element001  label="W_element : 1"  # scripted group (container) (typed FeaturePython)
  n = 1
  ref = W_element
FEATURE [App::DocumentObjectGroupPython] O_element020  label="O_element : 008"  # scripted group (container) (typed FeaturePython)
  n = 4
  ref = O_element
FEATURE [App::DocumentObjectGroupPython] G4_CADMIUM_TUNGSTATE  # scripted group (container) (typed FeaturePython)
  Dunit = g/cm3
  Dvalue = 7.9
  Group = -> [Cd_element002,W_element001,O_element020]
  conduct = 2
  density = 1
  expand = 3
  formula = G4_CADMIUM_TUNGSTATE
  name = G4_CADMIUM_TUNGSTATE
  specific = 4
FEATURE [App::DocumentObjectGroupPython] Ca_element005  label="Ca_element : 1"  # scripted group (container) (typed FeaturePython)
  n = 1
  ref = Ca_element
FEATURE [App::DocumentObjectGroupPython] C_element022  label="C_element : 009"  # scripted group (container) (typed FeaturePython)
  n = 1
  ref = C_element
FEATURE [App::DocumentObjectGroupPython] O_element021  label="O_element : 009"  # scripted group (container) (typed FeaturePython)
  n = 3
  ref = O_element
FEATURE [App::DocumentObjectGroupPython] G4_CALCIUM_CARBONATE  # scripted group (container) (typed FeaturePython)
  Dunit = g/cm3
  Dvalue = 2.8
  Group = -> [Ca_element005,C_element022,O_element021]
  conduct = 2
  density = 1
  expand = 3
  formula = G4_CALCIUM_CARBONATE
  name = G4_CALCIUM_CARBONATE
  specific = 4
FEATURE [App::DocumentObjectGroupPython] Ca_element006  label="Ca_element : 002"  # scripted group (container) (typed FeaturePython)
  n = 1
  ref = Ca_element
FEATURE [App::DocumentObjectGroupPython] F_element005  label="F_element : 003"  # scripted group (container) (typed FeaturePython)
  n = 2
  ref = F_element
FEATURE [App::DocumentObjectGroupPython] G4_CALCIUM_FLUORIDE  # scripted group (container) (typed FeaturePython)
  Dunit = g/cm3
  Dvalue = 3.18
  Group = -> [Ca_element006,F_element005]
  conduct = 2
  density = 1
  expand = 3
  formula = G4_CALCIUM_FLUORIDE
  name = G4_CALCIUM_FLUORIDE
  specific = 4
FEATURE [App::DocumentObjectGroupPython] Ca_element007  label="Ca_element : 003"  # scripted group (container) (typed FeaturePython)
  n = 1
  ref = Ca_element
FEATURE [App::DocumentObjectGroupPython] O_element022  label="O_element : 010"  # scripted group (container) (typed FeaturePython)
  n = 1
  ref = O_element
FEATURE [App::DocumentObjectGroupPython] G4_CALCIUM_OXIDE  # scripted group (container) (typed FeaturePython)
  Dunit = g/cm3
  Dvalue = 3.3
  Group = -> [Ca_element007,O_element022]
  conduct = 2
  density = 1
  expand = 3
  formula = G4_CALCIUM_OXIDE
  name = G4_CALCIUM_OXIDE
  specific = 4
FEATURE [App::DocumentObjectGroupPython] Ca_element008  label="Ca_element : 004"  # scripted group (container) (typed FeaturePython)
  n = 1
  ref = Ca_element
FEATURE [App::DocumentObjectGroupPython] S_element007  label="S_element : 002"  # scripted group (container) (typed FeaturePython)
  n = 1
  ref = S_element
FEATURE [App::DocumentObjectGroupPython] O_element023  label="O_element : 011"  # scripted group (container) (typed FeaturePython)
  n = 4
  ref = O_element
FEATURE [App::DocumentObjectGroupPython] G4_CALCIUM_SULFATE  # scripted group (container) (typed FeaturePython)
  Dunit = g/cm3
  Dvalue = 2.96
  Group = -> [Ca_element008,S_element007,O_element023]
  conduct = 2
  density = 1
  expand = 3
  formula = G4_CALCIUM_SULFATE
  name = G4_CALCIUM_SULFATE
  specific = 4
FEATURE [App::DocumentObjectGroupPython] Ca_element009  label="Ca_element : 005"  # scripted group (container) (typed FeaturePython)
  n = 1
  ref = Ca_element
FEATURE [App::DocumentObjectGroupPython] W_element002  label="W_element : 002"  # scripted group (container) (typed FeaturePython)
  n = 1
  ref = W_element
FEATURE [App::DocumentObjectGroupPython] O_element024  label="O_element : 012"  # scripted group (container) (typed FeaturePython)
  n = 4
  ref = O_element
FEATURE [App::DocumentObjectGroupPython] G4_CALCIUM_TUNGSTATE  # scripted group (container) (typed FeaturePython)
  Dunit = g/cm3
  Dvalue = 6.062
  Group = -> [Ca_element009,W_element002,O_element024]
  conduct = 2
  density = 1
  expand = 3
  formula = G4_CALCIUM_TUNGSTATE
  name = G4_CALCIUM_TUNGSTATE
  specific = 4
FEATURE [App::DocumentObjectGroupPython] C_element023  label="C_element : 010"  # scripted group (container) (typed FeaturePython)
  n = 1
  ref = C_element
FEATURE [App::DocumentObjectGroupPython] O_element025  label="O_element : 013"  # scripted group (container) (typed FeaturePython)
  n = 2
  ref = O_element
FEATURE [App::DocumentObjectGroupPython] G4_CARBON_DIOXIDE  # scripted group (container) (typed FeaturePython)
  Dunit = g/cm3
  Dvalue = 0.00184212
  Group = -> [C_element023,O_element025]
  conduct = 2
  density = 1
  expand = 3
  formula = G4_CARBON_DIOXIDE
  name = G4_CARBON_DIOXIDE
  specific = 4
FEATURE [App::DocumentObjectGroupPython] C_element024  label="C_element : 011"  # scripted group (container) (typed FeaturePython)
  n = 1
  ref = C_element
FEATURE [App::DocumentObjectGroupPython] Cl_element004  label="Cl_element : 4"  # scripted group (container) (typed FeaturePython)
  n = 4
  ref = Cl_element
FEATURE [App::DocumentObjectGroupPython] G4_CARBON_TETRACHLORIDE  # scripted group (container) (typed FeaturePython)
  Dunit = g/cm3
  Dvalue = 1.594
  Group = -> [C_element024,Cl_element004]
  conduct = 2
  density = 1
  expand = 3
  formula = G4_CARBON_TETRACHLORIDE
  name = G4_CARBON_TETRACHLORIDE
  specific = 4
FEATURE [App::DocumentObjectGroupPython] C_element025  label="C_element : 012"  # scripted group (container) (typed FeaturePython)
  n = 6
  ref = C_element
FEATURE [App::DocumentObjectGroupPython] H_element021  label="H_element : 012"  # scripted group (container) (typed FeaturePython)
  n = 10
  ref = H_element
FEATURE [App::DocumentObjectGroupPython] O_element026  label="O_element : 5"  # scripted group (container) (typed FeaturePython)
  n = 5
  ref = O_element
FEATURE [App::DocumentObjectGroupPython] G4_CELLULOSE_CELLOPHANE  # scripted group (container) (typed FeaturePython)
  Dunit = g/cm3
  Dvalue = 1.42
  Group = -> [C_element025,H_element021,O_element026]
  conduct = 2
  density = 1
  expand = 3
  formula = G4_CELLULOSE_CELLOPHANE
  name = G4_CELLULOSE_CELLOPHANE
  specific = 4
FEATURE [App::DocumentObjectGroupPython] H_element022  label="H_element : 0.067"  # scripted group (container) (typed FeaturePython)
  n = 0.067125
FEATURE [App::DocumentObjectGroupPython] C_element026  label="C_element : 0.545"  # scripted group (container) (typed FeaturePython)
  n = 0.545403
FEATURE [App::DocumentObjectGroupPython] O_element027  label="O_element : 0.387"  # scripted group (container) (typed FeaturePython)
  n = 0.387472
FEATURE [App::DocumentObjectGroupPython] G4_CELLULOSE_BUTYRATE  # scripted group (container) (typed FeaturePython)
  Dunit = g/cm3
  Dvalue = 1.2
  Group = -> [H_element022,C_element026,O_element027]
  conduct = 2
  density = 1
  expand = 3
  formula = G4_CELLULOSE_BUTYRATE
  name = G4_CELLULOSE_BUTYRATE
  specific = 4
FEATURE [App::DocumentObjectGroupPython] H_element023  label="H_element : 0.029"  # scripted group (container) (typed FeaturePython)
  n = 0.029216
FEATURE [App::DocumentObjectGroupPython] C_element027  label="C_element : 0.271"  # scripted group (container) (typed FeaturePython)
  n = 0.271296
FEATURE [App::DocumentObjectGroupPython] N_element013  label="N_element : 0.121"  # scripted group (container) (typed FeaturePython)
  n = 0.121276
FEATURE [App::DocumentObjectGroupPython] O_element028  label="O_element : 0.578"  # scripted group (container) (typed FeaturePython)
  n = 0.578212
FEATURE [App::DocumentObjectGroupPython] G4_CELLULOSE_NITRATE  # scripted group (container) (typed FeaturePython)
  Dunit = g/cm3
  Dvalue = 1.49
  Group = -> [H_element023,C_element027,N_element013,O_element028]
  conduct = 2
  density = 1
  expand = 3
  formula = G4_CELLULOSE_NITRATE
  name = G4_CELLULOSE_NITRATE
  specific = 4
FEATURE [App::DocumentObjectGroupPython] H_element024  label="H_element : 0.108"  # scripted group (container) (typed FeaturePython)
  n = 0.107596
FEATURE [App::DocumentObjectGroupPython] N_element014  label="N_element : 0.001"  # scripted group (container) (typed FeaturePython)
  n = 0.0008
FEATURE [App::DocumentObjectGroupPython] O_element029  label="O_element : 0.875"  # scripted group (container) (typed FeaturePython)
  n = 0.874976
FEATURE [App::DocumentObjectGroupPython] S_element008  label="S_element : 0.015"  # scripted group (container) (typed FeaturePython)
  n = 0.014627
FEATURE [App::DocumentObjectGroupPython] Ce_element001  label="Ce_element : 0.002"  # scripted group (container) (typed FeaturePython)
  n = 0.002001
FEATURE [App::DocumentObjectGroupPython] G4_CERIC_SULFATE  # scripted group (container) (typed FeaturePython)
  Dunit = g/cm3
  Dvalue = 1.03
  Group = -> [H_element024,N_element014,O_element029,S_element008,Ce_element001]
  conduct = 2
  density = 1
  expand = 3
  formula = G4_CERIC_SULFATE
  name = G4_CERIC_SULFATE
  specific = 4
FEATURE [App::DocumentObjectGroupPython] Cs_element001  label="Cs_element : 1"  # scripted group (container) (typed FeaturePython)
  n = 1
  ref = Cs_element
FEATURE [App::DocumentObjectGroupPython] F_element006  label="F_element : 1"  # scripted group (container) (typed FeaturePython)
  n = 1
  ref = F_element
FEATURE [App::DocumentObjectGroupPython] G4_CESIUM_FLUORIDE  # scripted group (container) (typed FeaturePython)
  Dunit = g/cm3
  Dvalue = 4.115
  Group = -> [Cs_element001,F_element006]
  conduct = 2
  density = 1
  expand = 3
  formula = G4_CESIUM_FLUORIDE
  name = G4_CESIUM_FLUORIDE
  specific = 4
FEATURE [App::DocumentObjectGroupPython] Cs_element002  label="Cs_element : 002"  # scripted group (container) (typed FeaturePython)
  n = 1
  ref = Cs_element
FEATURE [App::DocumentObjectGroupPython] I_element001  label="I_element : 1"  # scripted group (container) (typed FeaturePython)
  n = 1
  ref = I_element
FEATURE [App::DocumentObjectGroupPython] G4_CESIUM_IODIDE  # scripted group (container) (typed FeaturePython)
  Dunit = g/cm3
  Dvalue = 4.51
  Group = -> [Cs_element002,I_element001]
  conduct = 2
  density = 1
  expand = 3
  formula = G4_CESIUM_IODIDE
  name = G4_CESIUM_IODIDE
  specific = 4
FEATURE [App::DocumentObjectGroupPython] C_element028  label="C_element : 013"  # scripted group (container) (typed FeaturePython)
  n = 6
  ref = C_element
FEATURE [App::DocumentObjectGroupPython] H_element025  label="H_element : 013"  # scripted group (container) (typed FeaturePython)
  n = 5
  ref = H_element
FEATURE [App::DocumentObjectGroupPython] Cl_element005  label="Cl_element : 1"  # scripted group (container) (typed FeaturePython)
  n = 1
  ref = Cl_element
FEATURE [App::DocumentObjectGroupPython] G4_CHLOROBENZENE  # scripted group (container) (typed FeaturePython)
  Dunit = g/cm3
  Dvalue = 1.1058
  Group = -> [C_element028,H_element025,Cl_element005]
  conduct = 2
  density = 1
  expand = 3
  formula = G4_CHLOROBENZENE
  name = G4_CHLOROBENZENE
  specific = 4
FEATURE [App::DocumentObjectGroupPython] C_element029  label="C_element : 014"  # scripted group (container) (typed FeaturePython)
  n = 1
  ref = C_element
FEATURE [App::DocumentObjectGroupPython] H_element026  label="H_element : 1"  # scripted group (container) (typed FeaturePython)
  n = 1
  ref = H_element
FEATURE [App::DocumentObjectGroupPython] Cl_element006  label="Cl_element : 3"  # scripted group (container) (typed FeaturePython)
  n = 3
  ref = Cl_element
FEATURE [App::DocumentObjectGroupPython] G4_CHLOROFORM  # scripted group (container) (typed FeaturePython)
  Dunit = g/cm3
  Dvalue = 1.4832
  Group = -> [C_element029,H_element026,Cl_element006]
  conduct = 2
  density = 1
  expand = 3
  formula = G4_CHLOROFORM
  name = G4_CHLOROFORM
  specific = 4
FEATURE [App::DocumentObjectGroupPython] H_element027  label="H_element : 0.010"  # scripted group (container) (typed FeaturePython)
  n = 0.01
FEATURE [App::DocumentObjectGroupPython] C_element030  label="C_element : 0.001"  # scripted group (container) (typed FeaturePython)
  n = 0.001
FEATURE [App::DocumentObjectGroupPython] O_element030  label="O_element : 0.529"  # scripted group (container) (typed FeaturePython)
  n = 0.529107
FEATURE [App::DocumentObjectGroupPython] Na_element005  label="Na_element : 0.016"  # scripted group (container) (typed FeaturePython)
  n = 0.016
FEATURE [App::DocumentObjectGroupPython] Mg_element003  label="Mg_element : 0.004"  # scripted group (container) (typed FeaturePython)
  n = 0.002
FEATURE [App::DocumentObjectGroupPython] Al_element002  label="Al_element : 0.034"  # scripted group (container) (typed FeaturePython)
  n = 0.033872
FEATURE [App::DocumentObjectGroupPython] Si_element002  label="Si_element : 0.337"  # scripted group (container) (typed FeaturePython)
  n = 0.337021
FEATURE [App::DocumentObjectGroupPython] K_element003  label="K_element : 0.013"  # scripted group (container) (typed FeaturePython)
  n = 0.013
FEATURE [App::DocumentObjectGroupPython] Ca_element010  label="Ca_element : 0.044"  # scripted group (container) (typed FeaturePython)
  n = 0.044
FEATURE [App::DocumentObjectGroupPython] Fe_element002  label="Fe_element : 0.014"  # scripted group (container) (typed FeaturePython)
  n = 0.014
FEATURE [App::DocumentObjectGroupPython] G4_CONCRETE  # scripted group (container) (typed FeaturePython)
  Dunit = g/cm3
  Dvalue = 2.3
  Group = -> [H_element027,C_element030,O_element030,Na_element005,Mg_element003,Al_element002,Si_element002,K_element003,Ca_element010,Fe_element002]
  conduct = 2
  density = 1
  expand = 3
  formula = G4_CONCRETE
  name = G4_CONCRETE
  specific = 4
FEATURE [App::DocumentObjectGroupPython] C_element031  label="C_element : 015"  # scripted group (container) (typed FeaturePython)
  n = 6
  ref = C_element
FEATURE [App::DocumentObjectGroupPython] H_element028  label="H_element : 12"  # scripted group (container) (typed FeaturePython)
  n = 12
  ref = H_element
FEATURE [App::DocumentObjectGroupPython] G4_CYCLOHEXANE  # scripted group (container) (typed FeaturePython)
  Dunit = g/cm3
  Dvalue = 0.779
  Group = -> [C_element031,H_element028]
  conduct = 2
  density = 1
  expand = 3
  formula = G4_CYCLOHEXANE
  name = G4_CYCLOHEXANE
  specific = 4
FEATURE [App::DocumentObjectGroupPython] C_element032  label="C_element : 016"  # scripted group (container) (typed FeaturePython)
  n = 6
  ref = C_element
FEATURE [App::DocumentObjectGroupPython] H_element029  label="H_element : 4"  # scripted group (container) (typed FeaturePython)
  n = 4
  ref = H_element
FEATURE [App::DocumentObjectGroupPython] Cl_element007  label="Cl_element : 2"  # scripted group (container) (typed FeaturePython)
  n = 2
  ref = Cl_element
FEATURE [App::DocumentObjectGroupPython] G4_1_2_DICHLOROBENZENE  label="G4_1.2-DICHLOROBENZENE"  # scripted group (container) (typed FeaturePython)
  Dunit = g/cm3
  Dvalue = 1.3048
  Group = -> [C_element032,H_element029,Cl_element007]
  conduct = 2
  density = 1
  expand = 3
  formula = G4_1.2-DICHLOROBENZENE
  name = G4_1.2-DICHLOROBENZENE
  specific = 4
FEATURE [App::DocumentObjectGroupPython] C_element033  label="C_element : 017"  # scripted group (container) (typed FeaturePython)
  n = 4
  ref = C_element
FEATURE [App::DocumentObjectGroupPython] H_element030  label="H_element : 8"  # scripted group (container) (typed FeaturePython)
  n = 8
  ref = H_element
FEATURE [App::DocumentObjectGroupPython] O_element031  label="O_element : 014"  # scripted group (container) (typed FeaturePython)
  n = 1
  ref = O_element
FEATURE [App::DocumentObjectGroupPython] Cl_element008  label="Cl_element : 005"  # scripted group (container) (typed FeaturePython)
  n = 2
  ref = Cl_element
FEATURE [App::DocumentObjectGroupPython] G4_DICHLORODIETHYL_ETHER  # scripted group (container) (typed FeaturePython)
  Dunit = g/cm3
  Dvalue = 1.2199
  Group = -> [C_element033,H_element030,O_element031,Cl_element008]
  conduct = 2
  density = 1
  expand = 3
  formula = G4_DICHLORODIETHYL_ETHER
  name = G4_DICHLORODIETHYL_ETHER
  specific = 4
FEATURE [App::DocumentObjectGroupPython] C_element034  label="C_element : 018"  # scripted group (container) (typed FeaturePython)
  n = 2
  ref = C_element
FEATURE [App::DocumentObjectGroupPython] H_element031  label="H_element : 014"  # scripted group (container) (typed FeaturePython)
  n = 4
  ref = H_element
FEATURE [App::DocumentObjectGroupPython] Cl_element009  label="Cl_element : 006"  # scripted group (container) (typed FeaturePython)
  n = 2
  ref = Cl_element
FEATURE [App::DocumentObjectGroupPython] G4_1_2_DICHLOROETHANE  label="G4_1.2-DICHLOROETHANE"  # scripted group (container) (typed FeaturePython)
  Dunit = g/cm3
  Dvalue = 1.2351
  Group = -> [C_element034,H_element031,Cl_element009]
  conduct = 2
  density = 1
  expand = 3
  formula = G4_1.2-DICHLOROETHANE
  name = G4_1.2-DICHLOROETHANE
  specific = 4
FEATURE [App::DocumentObjectGroupPython] C_element035  label="C_element : 019"  # scripted group (container) (typed FeaturePython)
  n = 4
  ref = C_element
FEATURE [App::DocumentObjectGroupPython] H_element032  label="H_element : 015"  # scripted group (container) (typed FeaturePython)
  n = 10
  ref = H_element
FEATURE [App::DocumentObjectGroupPython] O_element032  label="O_element : 015"  # scripted group (container) (typed FeaturePython)
  n = 1
  ref = O_element
FEATURE [App::DocumentObjectGroupPython] G4_DIETHYL_ETHER  # scripted group (container) (typed FeaturePython)
  Dunit = g/cm3
  Dvalue = 0.71378
  Group = -> [C_element035,H_element032,O_element032]
  conduct = 2
  density = 1
  expand = 3
  formula = G4_DIETHYL_ETHER
  name = G4_DIETHYL_ETHER
  specific = 4
FEATURE [App::DocumentObjectGroupPython] C_element036  label="C_element : 020"  # scripted group (container) (typed FeaturePython)
  n = 3
  ref = C_element
FEATURE [App::DocumentObjectGroupPython] H_element033  label="H_element : 016"  # scripted group (container) (typed FeaturePython)
  n = 7
  ref = H_element
FEATURE [App::DocumentObjectGroupPython] N_element015  label="N_element : 008"  # scripted group (container) (typed FeaturePython)
  n = 1
  ref = N_element
FEATURE [App::DocumentObjectGroupPython] O_element033  label="O_element : 016"  # scripted group (container) (typed FeaturePython)
  n = 1
  ref = O_element
FEATURE [App::DocumentObjectGroupPython] G4_N_N_DIMETHYL_FORMAMIDE  label="G4_N.N-DIMETHYL_FORMAMIDE"  # scripted group (container) (typed FeaturePython)
  Dunit = g/cm3
  Dvalue = 0.9487
  Group = -> [C_element036,H_element033,N_element015,O_element033]
  conduct = 2
  density = 1
  expand = 3
  formula = G4_N.N-DIMETHYL_FORMAMIDE
  name = G4_N.N-DIMETHYL_FORMAMIDE
  specific = 4
FEATURE [App::DocumentObjectGroupPython] C_element037  label="C_element : 021"  # scripted group (container) (typed FeaturePython)
  n = 2
  ref = C_element
FEATURE [App::DocumentObjectGroupPython] H_element034  label="H_element : 017"  # scripted group (container) (typed FeaturePython)
  n = 6
  ref = H_element
FEATURE [App::DocumentObjectGroupPython] O_element034  label="O_element : 017"  # scripted group (container) (typed FeaturePython)
  n = 1
  ref = O_element
FEATURE [App::DocumentObjectGroupPython] S_element009  label="S_element : 003"  # scripted group (container) (typed FeaturePython)
  n = 1
  ref = S_element
FEATURE [App::DocumentObjectGroupPython] G4_DIMETHYL_SULFOXIDE  # scripted group (container) (typed FeaturePython)
  Dunit = g/cm3
  Dvalue = 1.1014
  Group = -> [C_element037,H_element034,O_element034,S_element009]
  conduct = 2
  density = 1
  expand = 3
  formula = G4_DIMETHYL_SULFOXIDE
  name = G4_DIMETHYL_SULFOXIDE
  specific = 4
FEATURE [App::DocumentObjectGroupPython] C_element038  label="C_element : 022"  # scripted group (container) (typed FeaturePython)
  n = 2
  ref = C_element
FEATURE [App::DocumentObjectGroupPython] H_element035  label="H_element : 018"  # scripted group (container) (typed FeaturePython)
  n = 6
  ref = H_element
FEATURE [App::DocumentObjectGroupPython] G4_ETHANE  # scripted group (container) (typed FeaturePython)
  Dunit = g/cm3
  Dvalue = 0.00125324
  Group = -> [C_element038,H_element035]
  conduct = 2
  density = 1
  expand = 3
  formula = G4_ETHANE
  name = G4_ETHANE
  specific = 4
FEATURE [App::DocumentObjectGroupPython] C_element039  label="C_element : 023"  # scripted group (container) (typed FeaturePython)
  n = 2
  ref = C_element
FEATURE [App::DocumentObjectGroupPython] H_element036  label="H_element : 019"  # scripted group (container) (typed FeaturePython)
  n = 6
  ref = H_element
FEATURE [App::DocumentObjectGroupPython] O_element035  label="O_element : 018"  # scripted group (container) (typed FeaturePython)
  n = 1
  ref = O_element
FEATURE [App::DocumentObjectGroupPython] G4_ETHYL_ALCOHOL  # scripted group (container) (typed FeaturePython)
  Dunit = g/cm3
  Dvalue = 0.7893
  Group = -> [C_element039,H_element036,O_element035]
  conduct = 2
  density = 1
  expand = 3
  formula = G4_ETHYL_ALCOHOL
  name = G4_ETHYL_ALCOHOL
  specific = 4
FEATURE [App::DocumentObjectGroupPython] H_element037  label="H_element : 0.090"  # scripted group (container) (typed FeaturePython)
  n = 0.090027
FEATURE [App::DocumentObjectGroupPython] C_element040  label="C_element : 0.585"  # scripted group (container) (typed FeaturePython)
  n = 0.585182
FEATURE [App::DocumentObjectGroupPython] O_element036  label="O_element : 0.325"  # scripted group (container) (typed FeaturePython)
  n = 0.324791
FEATURE [App::DocumentObjectGroupPython] G4_ETHYL_CELLULOSE  # scripted group (container) (typed FeaturePython)
  Dunit = g/cm3
  Dvalue = 1.13
  Group = -> [H_element037,C_element040,O_element036]
  conduct = 2
  density = 1
  expand = 3
  formula = G4_ETHYL_CELLULOSE
  name = G4_ETHYL_CELLULOSE
  specific = 4
FEATURE [App::DocumentObjectGroupPython] C_element041  label="C_element : 024"  # scripted group (container) (typed FeaturePython)
  n = 2
  ref = C_element
FEATURE [App::DocumentObjectGroupPython] H_element038  label="H_element : 020"  # scripted group (container) (typed FeaturePython)
  n = 4
  ref = H_element
FEATURE [App::DocumentObjectGroupPython] G4_ETHYLENE  # scripted group (container) (typed FeaturePython)
  Dunit = g/cm3
  Dvalue = 0.00117497
  Group = -> [C_element041,H_element038]
  conduct = 2
  density = 1
  expand = 3
  formula = G4_ETHYLENE
  name = G4_ETHYLENE
  specific = 4
FEATURE [App::DocumentObjectGroupPython] H_element039  label="H_element : 0.096"  # scripted group (container) (typed FeaturePython)
  n = 0.096
FEATURE [App::DocumentObjectGroupPython] C_element042  label="C_element : 0.195"  # scripted group (container) (typed FeaturePython)
  n = 0.195
FEATURE [App::DocumentObjectGroupPython] N_element016  label="N_element : 0.057"  # scripted group (container) (typed FeaturePython)
  n = 0.057
FEATURE [App::DocumentObjectGroupPython] O_element037  label="O_element : 0.646"  # scripted group (container) (typed FeaturePython)
  n = 0.646
FEATURE [App::DocumentObjectGroupPython] Na_element006  label="Na_element : 0.017"  # scripted group (container) (typed FeaturePython)
  n = 0.001
FEATURE [App::DocumentObjectGroupPython] P_element005  label="P_element : 0.104"  # scripted group (container) (typed FeaturePython)
  n = 0.001
FEATURE [App::DocumentObjectGroupPython] S_element010  label="S_element : 0.016"  # scripted group (container) (typed FeaturePython)
  n = 0.003
FEATURE [App::DocumentObjectGroupPython] Cl_element010  label="Cl_element : 0.005"  # scripted group (container) (typed FeaturePython)
  n = 0.001
FEATURE [App::DocumentObjectGroupPython] G4_EYE_LENS_ICRP  # scripted group (container) (typed FeaturePython)
  Dunit = g/cm3
  Dvalue = 1.07
  Group = -> [H_element039,C_element042,N_element016,O_element037,Na_element006,P_element005,S_element010,Cl_element010]
  conduct = 2
  density = 1
  expand = 3
  formula = G4_EYE_LENS_ICRP
  name = G4_EYE_LENS_ICRP
  specific = 4
FEATURE [App::DocumentObjectGroupPython] Fe_element003  label="Fe_element : 2"  # scripted group (container) (typed FeaturePython)
  n = 2
  ref = Fe_element
FEATURE [App::DocumentObjectGroupPython] O_element038  label="O_element : 019"  # scripted group (container) (typed FeaturePython)
  n = 3
  ref = O_element
FEATURE [App::DocumentObjectGroupPython] G4_FERRIC_OXIDE  # scripted group (container) (typed FeaturePython)
  Dunit = g/cm3
  Dvalue = 5.2
  Group = -> [Fe_element003,O_element038]
  conduct = 2
  density = 1
  expand = 3
  formula = G4_FERRIC_OXIDE
  name = G4_FERRIC_OXIDE
  specific = 4
FEATURE [App::DocumentObjectGroupPython] Fe_element004  label="Fe_element : 1"  # scripted group (container) (typed FeaturePython)
  n = 1
  ref = Fe_element
FEATURE [App::DocumentObjectGroupPython] B_element003  label="B_element : 1"  # scripted group (container) (typed FeaturePython)
  n = 1
  ref = B_element
FEATURE [App::DocumentObjectGroupPython] G4_FERROBORIDE  # scripted group (container) (typed FeaturePython)
  Dunit = g/cm3
  Dvalue = 7.15
  Group = -> [Fe_element004,B_element003]
  conduct = 2
  density = 1
  expand = 3
  formula = G4_FERROBORIDE
  name = G4_FERROBORIDE
  specific = 4
FEATURE [App::DocumentObjectGroupPython] Fe_element005  label="Fe_element : 003"  # scripted group (container) (typed FeaturePython)
  n = 1
  ref = Fe_element
FEATURE [App::DocumentObjectGroupPython] O_element039  label="O_element : 020"  # scripted group (container) (typed FeaturePython)
  n = 1
  ref = O_element
FEATURE [App::DocumentObjectGroupPython] G4_FERROUS_OXIDE  # scripted group (container) (typed FeaturePython)
  Dunit = g/cm3
  Dvalue = 5.7
  Group = -> [Fe_element005,O_element039]
  conduct = 2
  density = 1
  expand = 3
  formula = G4_FERROUS_OXIDE
  name = G4_FERROUS_OXIDE
  specific = 4
FEATURE [App::DocumentObjectGroupPython] H_element040  label="H_element : 0.115"  # scripted group (container) (typed FeaturePython)
  n = 0.108259
FEATURE [App::DocumentObjectGroupPython] N_element017  label="N_element : 0.000"  # scripted group (container) (typed FeaturePython)
  n = 2.7e-05
FEATURE [App::DocumentObjectGroupPython] O_element040  label="O_element : 0.879"  # scripted group (container) (typed FeaturePython)
  n = 0.878636
FEATURE [App::DocumentObjectGroupPython] Na_element007  label="Na_element : 0.000"  # scripted group (container) (typed FeaturePython)
  n = 2.2e-05
FEATURE [App::DocumentObjectGroupPython] S_element011  label="S_element : 0.013"  # scripted group (container) (typed FeaturePython)
  n = 0.012968
FEATURE [App::DocumentObjectGroupPython] Cl_element011  label="Cl_element : 0.000"  # scripted group (container) (typed FeaturePython)
  n = 3.4e-05
FEATURE [App::DocumentObjectGroupPython] Fe_element006  label="Fe_element : 0.000"  # scripted group (container) (typed FeaturePython)
  n = 5.4e-05
FEATURE [App::DocumentObjectGroupPython] G4_FERROUS_SULFATE  # scripted group (container) (typed FeaturePython)
  Dunit = g/cm3
  Dvalue = 1.024
  Group = -> [H_element040,N_element017,O_element040,Na_element007,S_element011,Cl_element011,Fe_element006]
  conduct = 2
  density = 1
  expand = 3
  formula = G4_FERROUS_SULFATE
  name = G4_FERROUS_SULFATE
  specific = 4
FEATURE [App::DocumentObjectGroupPython] C_element043  label="C_element : 0.099"  # scripted group (container) (typed FeaturePython)
  n = 0.099335
FEATURE [App::DocumentObjectGroupPython] F_element007  label="F_element : 0.314"  # scripted group (container) (typed FeaturePython)
  n = 0.314247
FEATURE [App::DocumentObjectGroupPython] Cl_element012  label="Cl_element : 0.586"  # scripted group (container) (typed FeaturePython)
  n = 0.586418
FEATURE [App::DocumentObjectGroupPython] G4_FREON_12  label="G4_FREON-12"  # scripted group (container) (typed FeaturePython)
  Dunit = g/cm3
  Dvalue = 1.12
  Group = -> [C_element043,F_element007,Cl_element012]
  conduct = 2
  density = 1
  expand = 3
  formula = G4_FREON-12
  name = G4_FREON-12
  specific = 4
FEATURE [App::DocumentObjectGroupPython] C_element044  label="C_element : 0.057"  # scripted group (container) (typed FeaturePython)
  n = 0.057245
FEATURE [App::DocumentObjectGroupPython] F_element008  label="F_element : 0.181"  # scripted group (container) (typed FeaturePython)
  n = 0.181096
FEATURE [App::DocumentObjectGroupPython] Br_element001  label="Br_element : 0.762"  # scripted group (container) (typed FeaturePython)
  n = 0.761659
FEATURE [App::DocumentObjectGroupPython] G4_FREON_12B2  label="G4_FREON-12B2"  # scripted group (container) (typed FeaturePython)
  Dunit = g/cm3
  Dvalue = 1.8
  Group = -> [C_element044,F_element008,Br_element001]
  conduct = 2
  density = 1
  expand = 3
  formula = G4_FREON-12B2
  name = G4_FREON-12B2
  specific = 4
FEATURE [App::DocumentObjectGroupPython] C_element045  label="C_element : 0.115"  # scripted group (container) (typed FeaturePython)
  n = 0.114983
FEATURE [App::DocumentObjectGroupPython] F_element009  label="F_element : 0.546"  # scripted group (container) (typed FeaturePython)
  n = 0.545621
FEATURE [App::DocumentObjectGroupPython] Cl_element013  label="Cl_element : 0.339"  # scripted group (container) (typed FeaturePython)
  n = 0.339396
FEATURE [App::DocumentObjectGroupPython] G4_FREON_13  label="G4_FREON-13"  # scripted group (container) (typed FeaturePython)
  Dunit = g/cm3
  Dvalue = 0.95
  Group = -> [C_element045,F_element009,Cl_element013]
  conduct = 2
  density = 1
  expand = 3
  formula = G4_FREON-13
  name = G4_FREON-13
  specific = 4
FEATURE [App::DocumentObjectGroupPython] C_element046  label="C_element : 025"  # scripted group (container) (typed FeaturePython)
  n = 1
  ref = C_element
FEATURE [App::DocumentObjectGroupPython] F_element010  label="F_element : 3"  # scripted group (container) (typed FeaturePython)
  n = 3
  ref = F_element
FEATURE [App::DocumentObjectGroupPython] Br_element002  label="Br_element : 1"  # scripted group (container) (typed FeaturePython)
  n = 1
  ref = Br_element
FEATURE [App::DocumentObjectGroupPython] G4_FREON_13B1  label="G4_FREON-13B1"  # scripted group (container) (typed FeaturePython)
  Dunit = g/cm3
  Dvalue = 1.5
  Group = -> [C_element046,F_element010,Br_element002]
  conduct = 2
  density = 1
  expand = 3
  formula = G4_FREON-13B1
  name = G4_FREON-13B1
  specific = 4
FEATURE [App::DocumentObjectGroupPython] C_element047  label="C_element : 0.061"  # scripted group (container) (typed FeaturePython)
  n = 0.061309
FEATURE [App::DocumentObjectGroupPython] F_element011  label="F_element : 0.291"  # scripted group (container) (typed FeaturePython)
  n = 0.290924
FEATURE [App::DocumentObjectGroupPython] I_element002  label="I_element : 0.648"  # scripted group (container) (typed FeaturePython)
  n = 0.647767
FEATURE [App::DocumentObjectGroupPython] G4_FREON_13I1  label="G4_FREON-13I1"  # scripted group (container) (typed FeaturePython)
  Dunit = g/cm3
  Dvalue = 1.8
  Group = -> [C_element047,F_element011,I_element002]
  conduct = 2
  density = 1
  expand = 3
  formula = G4_FREON-13I1
  name = G4_FREON-13I1
  specific = 4
FEATURE [App::DocumentObjectGroupPython] Gd_element001  label="Gd_element : 2"  # scripted group (container) (typed FeaturePython)
  n = 2
  ref = Gd_element
FEATURE [App::DocumentObjectGroupPython] O_element041  label="O_element : 021"  # scripted group (container) (typed FeaturePython)
  n = 2
  ref = O_element
FEATURE [App::DocumentObjectGroupPython] S_element012  label="S_element : 004"  # scripted group (container) (typed FeaturePython)
  n = 1
  ref = S_element
FEATURE [App::DocumentObjectGroupPython] G4_GADOLINIUM_OXYSULFIDE  # scripted group (container) (typed FeaturePython)
  Dunit = g/cm3
  Dvalue = 7.44
  Group = -> [Gd_element001,O_element041,S_element012]
  conduct = 2
  density = 1
  expand = 3
  formula = G4_GADOLINIUM_OXYSULFIDE
  name = G4_GADOLINIUM_OXYSULFIDE
  specific = 4
FEATURE [App::DocumentObjectGroupPython] Ga_element001  label="Ga_element : 1"  # scripted group (container) (typed FeaturePython)
  n = 1
  ref = Ga_element
FEATURE [App::DocumentObjectGroupPython] As_element001  label="As_element : 1"  # scripted group (container) (typed FeaturePython)
  n = 1
  ref = As_element
FEATURE [App::DocumentObjectGroupPython] G4_GALLIUM_ARSENIDE  # scripted group (container) (typed FeaturePython)
  Dunit = g/cm3
  Dvalue = 5.31
  Group = -> [Ga_element001,As_element001]
  conduct = 2
  density = 1
  expand = 3
  formula = G4_GALLIUM_ARSENIDE
  name = G4_GALLIUM_ARSENIDE
  specific = 4
FEATURE [App::DocumentObjectGroupPython] H_element041  label="H_element : 0.081"  # scripted group (container) (typed FeaturePython)
  n = 0.08118
FEATURE [App::DocumentObjectGroupPython] C_element048  label="C_element : 0.416"  # scripted group (container) (typed FeaturePython)
  n = 0.41606
FEATURE [App::DocumentObjectGroupPython] N_element018  label="N_element : 0.111"  # scripted group (container) (typed FeaturePython)
  n = 0.11124
FEATURE [App::DocumentObjectGroupPython] O_element042  label="O_element : 0.381"  # scripted group (container) (typed FeaturePython)
  n = 0.38064
FEATURE [App::DocumentObjectGroupPython] S_element013  label="S_element : 0.011"  # scripted group (container) (typed FeaturePython)
  n = 0.01088
FEATURE [App::DocumentObjectGroupPython] G4_GEL_PHOTO_EMULSION  # scripted group (container) (typed FeaturePython)
  Dunit = g/cm3
  Dvalue = 1.2914
  Group = -> [H_element041,C_element048,N_element018,O_element042,S_element013]
  conduct = 2
  density = 1
  expand = 3
  formula = G4_GEL_PHOTO_EMULSION
  name = G4_GEL_PHOTO_EMULSION
  specific = 4
FEATURE [App::DocumentObjectGroupPython] B_element004  label="B_element : 0.040"  # scripted group (container) (typed FeaturePython)
  n = 0.0400639
FEATURE [App::DocumentObjectGroupPython] O_element043  label="O_element : 0.540"  # scripted group (container) (typed FeaturePython)
  n = 0.539561
FEATURE [App::DocumentObjectGroupPython] Na_element008  label="Na_element : 0.028"  # scripted group (container) (typed FeaturePython)
  n = 0.0281909
FEATURE [App::DocumentObjectGroupPython] Al_element003  label="Al_element : 0.012"  # scripted group (container) (typed FeaturePython)
  n = 0.011644
FEATURE [App::DocumentObjectGroupPython] Si_element003  label="Si_element : 0.377"  # scripted group (container) (typed FeaturePython)
  n = 0.377219
FEATURE [App::DocumentObjectGroupPython] K_element004  label="K_element : 0.014"  # scripted group (container) (typed FeaturePython)
  n = 0.00332099
FEATURE [App::DocumentObjectGroupPython] G4_Pyrex_Glass  # scripted group (container) (typed FeaturePython)
  Dunit = g/cm3
  Dvalue = 2.23
  Group = -> [B_element004,O_element043,Na_element008,Al_element003,Si_element003,K_element004]
  conduct = 2
  density = 1
  expand = 3
  formula = G4_Pyrex_Glass
  name = G4_Pyrex_Glass
  specific = 4
FEATURE [App::DocumentObjectGroupPython] O_element044  label="O_element : 0.156"  # scripted group (container) (typed FeaturePython)
  n = 0.156453
FEATURE [App::DocumentObjectGroupPython] Si_element004  label="Si_element : 0.081"  # scripted group (container) (typed FeaturePython)
  n = 0.080866
FEATURE [App::DocumentObjectGroupPython] Ti_element001  label="Ti_element : 0.008"  # scripted group (container) (typed FeaturePython)
  n = 0.008092
FEATURE [App::DocumentObjectGroupPython] As_element002  label="As_element : 0.003"  # scripted group (container) (typed FeaturePython)
  n = 0.002651
FEATURE [App::DocumentObjectGroupPython] Pb_element001  label="Pb_element : 0.752"  # scripted group (container) (typed FeaturePython)
  n = 0.751938
FEATURE [App::DocumentObjectGroupPython] G4_GLASS_LEAD  # scripted group (container) (typed FeaturePython)
  Dunit = g/cm3
  Dvalue = 6.22
  Group = -> [O_element044,Si_element004,Ti_element001,As_element002,Pb_element001]
  conduct = 2
  density = 1
  expand = 3
  formula = G4_GLASS_LEAD
  name = G4_GLASS_LEAD
  specific = 4
FEATURE [App::DocumentObjectGroupPython] O_element045  label="O_element : 0.460"  # scripted group (container) (typed FeaturePython)
  n = 0.4598
FEATURE [App::DocumentObjectGroupPython] Na_element009  label="Na_element : 0.096"  # scripted group (container) (typed FeaturePython)
  n = 0.0964411
FEATURE [App::DocumentObjectGroupPython] Si_element005  label="Si_element : 0.378"  # scripted group (container) (typed FeaturePython)
  n = 0.336553
FEATURE [App::DocumentObjectGroupPython] Ca_element011  label="Ca_element : 0.107"  # scripted group (container) (typed FeaturePython)
  n = 0.107205
FEATURE [App::DocumentObjectGroupPython] G4_GLASS_PLATE  # scripted group (container) (typed FeaturePython)
  Dunit = g/cm3
  Dvalue = 2.4
  Group = -> [O_element045,Na_element009,Si_element005,Ca_element011]
  conduct = 2
  density = 1
  expand = 3
  formula = G4_GLASS_PLATE
  name = G4_GLASS_PLATE
  specific = 4
FEATURE [App::DocumentObjectGroupPython] C_element049  label="C_element : 026"  # scripted group (container) (typed FeaturePython)
  n = 5
  ref = C_element
FEATURE [App::DocumentObjectGroupPython] H_element042  label="H_element : 021"  # scripted group (container) (typed FeaturePython)
  n = 10
  ref = H_element
FEATURE [App::DocumentObjectGroupPython] N_element019  label="N_element : 2"  # scripted group (container) (typed FeaturePython)
  n = 2
  ref = N_element
FEATURE [App::DocumentObjectGroupPython] O_element046  label="O_element : 022"  # scripted group (container) (typed FeaturePython)
  n = 3
  ref = O_element
FEATURE [App::DocumentObjectGroupPython] G4_GLUTAMINE  # scripted group (container) (typed FeaturePython)
  Dunit = g/cm3
  Dvalue = 1.46
  Group = -> [C_element049,H_element042,N_element019,O_element046]
  conduct = 2
  density = 1
  expand = 3
  formula = G4_GLUTAMINE
  name = G4_GLUTAMINE
  specific = 4
FEATURE [App::DocumentObjectGroupPython] C_element050  label="C_element : 027"  # scripted group (container) (typed FeaturePython)
  n = 3
  ref = C_element
FEATURE [App::DocumentObjectGroupPython] H_element043  label="H_element : 022"  # scripted group (container) (typed FeaturePython)
  n = 8
  ref = H_element
FEATURE [App::DocumentObjectGroupPython] O_element047  label="O_element : 023"  # scripted group (container) (typed FeaturePython)
  n = 3
  ref = O_element
FEATURE [App::DocumentObjectGroupPython] G4_GLYCEROL  # scripted group (container) (typed FeaturePython)
  Dunit = g/cm3
  Dvalue = 1.2613
  Group = -> [C_element050,H_element043,O_element047]
  conduct = 2
  density = 1
  expand = 3
  formula = G4_GLYCEROL
  name = G4_GLYCEROL
  specific = 4
FEATURE [App::DocumentObjectGroupPython] C_element051  label="C_element : 028"  # scripted group (container) (typed FeaturePython)
  n = 5
  ref = C_element
FEATURE [App::DocumentObjectGroupPython] H_element044  label="H_element : 023"  # scripted group (container) (typed FeaturePython)
  n = 5
  ref = H_element
FEATURE [App::DocumentObjectGroupPython] N_element020  label="N_element : 009"  # scripted group (container) (typed FeaturePython)
  n = 5
  ref = N_element
FEATURE [App::DocumentObjectGroupPython] O_element048  label="O_element : 024"  # scripted group (container) (typed FeaturePython)
  n = 1
  ref = O_element
FEATURE [App::DocumentObjectGroupPython] G4_GUANINE  # scripted group (container) (typed FeaturePython)
  Dunit = g/cm3
  Dvalue = 2.2
  Group = -> [C_element051,H_element044,N_element020,O_element048]
  conduct = 2
  density = 1
  expand = 3
  formula = G4_GUANINE
  name = G4_GUANINE
  specific = 4
FEATURE [App::DocumentObjectGroupPython] Ca_element012  label="Ca_element : 006"  # scripted group (container) (typed FeaturePython)
  n = 1
  ref = Ca_element
FEATURE [App::DocumentObjectGroupPython] S_element014  label="S_element : 005"  # scripted group (container) (typed FeaturePython)
  n = 1
  ref = S_element
FEATURE [App::DocumentObjectGroupPython] O_element049  label="O_element : 6"  # scripted group (container) (typed FeaturePython)
  n = 6
  ref = O_element
FEATURE [App::DocumentObjectGroupPython] H_element045  label="H_element : 024"  # scripted group (container) (typed FeaturePython)
  n = 4
  ref = H_element
FEATURE [App::DocumentObjectGroupPython] G4_GYPSUM  # scripted group (container) (typed FeaturePython)
  Dunit = g/cm3
  Dvalue = 2.32
  Group = -> [Ca_element012,S_element014,O_element049,H_element045]
  conduct = 2
  density = 1
  expand = 3
  formula = G4_GYPSUM
  name = G4_GYPSUM
  specific = 4
FEATURE [App::DocumentObjectGroupPython] C_element052  label="C_element : 7"  # scripted group (container) (typed FeaturePython)
  n = 7
  ref = C_element
FEATURE [App::DocumentObjectGroupPython] H_element046  label="H_element : 16"  # scripted group (container) (typed FeaturePython)
  n = 16
  ref = H_element
FEATURE [App::DocumentObjectGroupPython] G4_N_HEPTANE  label="G4_N-HEPTANE"  # scripted group (container) (typed FeaturePython)
  Dunit = g/cm3
  Dvalue = 0.68376
  Group = -> [C_element052,H_element046]
  conduct = 2
  density = 1
  expand = 3
  formula = G4_N-HEPTANE
  name = G4_N-HEPTANE
  specific = 4
FEATURE [App::DocumentObjectGroupPython] C_element053  label="C_element : 029"  # scripted group (container) (typed FeaturePython)
  n = 6
  ref = C_element
FEATURE [App::DocumentObjectGroupPython] H_element047  label="H_element : 14"  # scripted group (container) (typed FeaturePython)
  n = 14
  ref = H_element
FEATURE [App::DocumentObjectGroupPython] G4_N_HEXANE  label="G4_N-HEXANE"  # scripted group (container) (typed FeaturePython)
  Dunit = g/cm3
  Dvalue = 0.6603
  Group = -> [C_element053,H_element047]
  conduct = 2
  density = 1
  expand = 3
  formula = G4_N-HEXANE
  name = G4_N-HEXANE
  specific = 4
FEATURE [App::DocumentObjectGroupPython] C_element054  label="C_element : 22"  # scripted group (container) (typed FeaturePython)
  n = 22
  ref = C_element
FEATURE [App::DocumentObjectGroupPython] H_element048  label="H_element : 025"  # scripted group (container) (typed FeaturePython)
  n = 10
  ref = H_element
FEATURE [App::DocumentObjectGroupPython] N_element021  label="N_element : 010"  # scripted group (container) (typed FeaturePython)
  n = 2
  ref = N_element
FEATURE [App::DocumentObjectGroupPython] O_element050  label="O_element : 025"  # scripted group (container) (typed FeaturePython)
  n = 5
  ref = O_element
FEATURE [App::DocumentObjectGroupPython] G4_KAPTON  # scripted group (container) (typed FeaturePython)
  Dunit = g/cm3
  Dvalue = 1.42
  Group = -> [C_element054,H_element048,N_element021,O_element050]
  conduct = 2
  density = 1
  expand = 3
  formula = G4_KAPTON
  name = G4_KAPTON
  specific = 4
FEATURE [App::DocumentObjectGroupPython] La_element001  label="La_element : 1"  # scripted group (container) (typed FeaturePython)
  n = 1
  ref = La_element
FEATURE [App::DocumentObjectGroupPython] Br_element003  label="Br_element : 002"  # scripted group (container) (typed FeaturePython)
  n = 1
  ref = Br_element
FEATURE [App::DocumentObjectGroupPython] O_element051  label="O_element : 026"  # scripted group (container) (typed FeaturePython)
  n = 1
  ref = O_element
FEATURE [App::DocumentObjectGroupPython] G4_LANTHANUM_OXYBROMIDE  # scripted group (container) (typed FeaturePython)
  Dunit = g/cm3
  Dvalue = 6.28
  Group = -> [La_element001,Br_element003,O_element051]
  conduct = 2
  density = 1
  expand = 3
  formula = G4_LANTHANUM_OXYBROMIDE
  name = G4_LANTHANUM_OXYBROMIDE
  specific = 4
FEATURE [App::DocumentObjectGroupPython] La_element002  label="La_element : 2"  # scripted group (container) (typed FeaturePython)
  n = 2
  ref = La_element
FEATURE [App::DocumentObjectGroupPython] O_element052  label="O_element : 027"  # scripted group (container) (typed FeaturePython)
  n = 2
  ref = O_element
FEATURE [App::DocumentObjectGroupPython] S_element015  label="S_element : 006"  # scripted group (container) (typed FeaturePython)
  n = 1
  ref = S_element
FEATURE [App::DocumentObjectGroupPython] G4_LANTHANUM_OXYSULFIDE  # scripted group (container) (typed FeaturePython)
  Dunit = g/cm3
  Dvalue = 5.86
  Group = -> [La_element002,O_element052,S_element015]
  conduct = 2
  density = 1
  expand = 3
  formula = G4_LANTHANUM_OXYSULFIDE
  name = G4_LANTHANUM_OXYSULFIDE
  specific = 4
FEATURE [App::DocumentObjectGroupPython] O_element053  label="O_element : 0.072"  # scripted group (container) (typed FeaturePython)
  n = 0.071682
FEATURE [App::DocumentObjectGroupPython] Pb_element002  label="Pb_element : 0.928"  # scripted group (container) (typed FeaturePython)
  n = 0.928318
FEATURE [App::DocumentObjectGroupPython] G4_LEAD_OXIDE  # scripted group (container) (typed FeaturePython)
  Dunit = g/cm3
  Dvalue = 9.53
  Group = -> [O_element053,Pb_element002]
  conduct = 2
  density = 1
  expand = 3
  formula = G4_LEAD_OXIDE
  name = G4_LEAD_OXIDE
  specific = 4
FEATURE [App::DocumentObjectGroupPython] Li_element001  label="Li_element : 1"  # scripted group (container) (typed FeaturePython)
  n = 1
  ref = Li_element
FEATURE [App::DocumentObjectGroupPython] N_element022  label="N_element : 011"  # scripted group (container) (typed FeaturePython)
  n = 1
  ref = N_element
FEATURE [App::DocumentObjectGroupPython] H_element049  label="H_element : 026"  # scripted group (container) (typed FeaturePython)
  n = 2
  ref = H_element
FEATURE [App::DocumentObjectGroupPython] G4_LITHIUM_AMIDE  # scripted group (container) (typed FeaturePython)
  Dunit = g/cm3
  Dvalue = 1.178
  Group = -> [Li_element001,N_element022,H_element049]
  conduct = 2
  density = 1
  expand = 3
  formula = G4_LITHIUM_AMIDE
  name = G4_LITHIUM_AMIDE
  specific = 4
FEATURE [App::DocumentObjectGroupPython] Li_element002  label="Li_element : 2"  # scripted group (container) (typed FeaturePython)
  n = 2
  ref = Li_element
FEATURE [App::DocumentObjectGroupPython] C_element055  label="C_element : 030"  # scripted group (container) (typed FeaturePython)
  n = 1
  ref = C_element
FEATURE [App::DocumentObjectGroupPython] O_element054  label="O_element : 028"  # scripted group (container) (typed FeaturePython)
  n = 3
  ref = O_element
FEATURE [App::DocumentObjectGroupPython] G4_LITHIUM_CARBONATE  # scripted group (container) (typed FeaturePython)
  Dunit = g/cm3
  Dvalue = 2.11
  Group = -> [Li_element002,C_element055,O_element054]
  conduct = 2
  density = 1
  expand = 3
  formula = G4_LITHIUM_CARBONATE
  name = G4_LITHIUM_CARBONATE
  specific = 4
FEATURE [App::DocumentObjectGroupPython] Li_element003  label="Li_element : 003"  # scripted group (container) (typed FeaturePython)
  n = 1
  ref = Li_element
FEATURE [App::DocumentObjectGroupPython] F_element012  label="F_element : 004"  # scripted group (container) (typed FeaturePython)
  n = 1
  ref = F_element
FEATURE [App::DocumentObjectGroupPython] G4_LITHIUM_FLUORIDE  # scripted group (container) (typed FeaturePython)
  Dunit = g/cm3
  Dvalue = 2.635
  Group = -> [Li_element003,F_element012]
  conduct = 2
  density = 1
  expand = 3
  formula = G4_LITHIUM_FLUORIDE
  name = G4_LITHIUM_FLUORIDE
  specific = 4
FEATURE [App::DocumentObjectGroupPython] Li_element004  label="Li_element : 004"  # scripted group (container) (typed FeaturePython)
  n = 1
  ref = Li_element
FEATURE [App::DocumentObjectGroupPython] H_element050  label="H_element : 027"  # scripted group (container) (typed FeaturePython)
  n = 1
  ref = H_element
FEATURE [App::DocumentObjectGroupPython] G4_LITHIUM_HYDRIDE  # scripted group (container) (typed FeaturePython)
  Dunit = g/cm3
  Dvalue = 0.82
  Group = -> [Li_element004,H_element050]
  conduct = 2
  density = 1
  expand = 3
  formula = G4_LITHIUM_HYDRIDE
  name = G4_LITHIUM_HYDRIDE
  specific = 4
FEATURE [App::DocumentObjectGroupPython] Li_element005  label="Li_element : 005"  # scripted group (container) (typed FeaturePython)
  n = 1
  ref = Li_element
FEATURE [App::DocumentObjectGroupPython] I_element003  label="I_element : 002"  # scripted group (container) (typed FeaturePython)
  n = 1
  ref = I_element
FEATURE [App::DocumentObjectGroupPython] G4_LITHIUM_IODIDE  # scripted group (container) (typed FeaturePython)
  Dunit = g/cm3
  Dvalue = 3.494
  Group = -> [Li_element005,I_element003]
  conduct = 2
  density = 1
  expand = 3
  formula = G4_LITHIUM_IODIDE
  name = G4_LITHIUM_IODIDE
  specific = 4
FEATURE [App::DocumentObjectGroupPython] Li_element006  label="Li_element : 006"  # scripted group (container) (typed FeaturePython)
  n = 2
  ref = Li_element
FEATURE [App::DocumentObjectGroupPython] O_element055  label="O_element : 029"  # scripted group (container) (typed FeaturePython)
  n = 1
  ref = O_element
FEATURE [App::DocumentObjectGroupPython] G4_LITHIUM_OXIDE  # scripted group (container) (typed FeaturePython)
  Dunit = g/cm3
  Dvalue = 2.013
  Group = -> [Li_element006,O_element055]
  conduct = 2
  density = 1
  expand = 3
  formula = G4_LITHIUM_OXIDE
  name = G4_LITHIUM_OXIDE
  specific = 4
FEATURE [App::DocumentObjectGroupPython] Li_element007  label="Li_element : 007"  # scripted group (container) (typed FeaturePython)
  n = 2
  ref = Li_element
FEATURE [App::DocumentObjectGroupPython] B_element005  label="B_element : 005"  # scripted group (container) (typed FeaturePython)
  n = 4
  ref = B_element
FEATURE [App::DocumentObjectGroupPython] O_element056  label="O_element : 7"  # scripted group (container) (typed FeaturePython)
  n = 7
  ref = O_element
FEATURE [App::DocumentObjectGroupPython] G4_LITHIUM_TETRABORATE  # scripted group (container) (typed FeaturePython)
  Dunit = g/cm3
  Dvalue = 2.44
  Group = -> [Li_element007,B_element005,O_element056]
  conduct = 2
  density = 1
  expand = 3
  formula = G4_LITHIUM_TETRABORATE
  name = G4_LITHIUM_TETRABORATE
  specific = 4
FEATURE [App::DocumentObjectGroupPython] H_element051  label="H_element : 0.105"  # scripted group (container) (typed FeaturePython)
  n = 0.105
FEATURE [App::DocumentObjectGroupPython] C_element056  label="C_element : 0.083"  # scripted group (container) (typed FeaturePython)
  n = 0.083
FEATURE [App::DocumentObjectGroupPython] N_element023  label="N_element : 0.023"  # scripted group (container) (typed FeaturePython)
  n = 0.023
FEATURE [App::DocumentObjectGroupPython] O_element057  label="O_element : 0.779"  # scripted group (container) (typed FeaturePython)
  n = 0.779
FEATURE [App::DocumentObjectGroupPython] Na_element010  label="Na_element : 0.097"  # scripted group (container) (typed FeaturePython)
  n = 0.002
FEATURE [App::DocumentObjectGroupPython] P_element006  label="P_element : 0.105"  # scripted group (container) (typed FeaturePython)
  n = 0.001
FEATURE [App::DocumentObjectGroupPython] S_element016  label="S_element : 0.017"  # scripted group (container) (typed FeaturePython)
  n = 0.002
FEATURE [App::DocumentObjectGroupPython] Cl_element014  label="Cl_element : 0.587"  # scripted group (container) (typed FeaturePython)
  n = 0.003
FEATURE [App::DocumentObjectGroupPython] K_element005  label="K_element : 0.015"  # scripted group (container) (typed FeaturePython)
  n = 0.002
FEATURE [App::DocumentObjectGroupPython] G4_LUNG_ICRP  # scripted group (container) (typed FeaturePython)
  Dunit = g/cm3
  Dvalue = 1.04
  Group = -> [H_element051,C_element056,N_element023,O_element057,Na_element010,P_element006,S_element016,Cl_element014,K_element005]
  conduct = 2
  density = 1
  expand = 3
  formula = G4_LUNG_ICRP
  name = G4_LUNG_ICRP
  specific = 4
FEATURE [App::DocumentObjectGroupPython] H_element052  label="H_element : 0.116"  # scripted group (container) (typed FeaturePython)
  n = 0.114318
FEATURE [App::DocumentObjectGroupPython] C_element057  label="C_element : 0.656"  # scripted group (container) (typed FeaturePython)
  n = 0.655824
FEATURE [App::DocumentObjectGroupPython] O_element058  label="O_element : 0.092"  # scripted group (container) (typed FeaturePython)
  n = 0.0921831
FEATURE [App::DocumentObjectGroupPython] Mg_element004  label="Mg_element : 0.135"  # scripted group (container) (typed FeaturePython)
  n = 0.134792
FEATURE [App::DocumentObjectGroupPython] Ca_element013  label="Ca_element : 0.003"  # scripted group (container) (typed FeaturePython)
  n = 0.002883
FEATURE [App::DocumentObjectGroupPython] G4_M3_WAX  # scripted group (container) (typed FeaturePython)
  Dunit = g/cm3
  Dvalue = 1.05
  Group = -> [H_element052,C_element057,O_element058,Mg_element004,Ca_element013]
  conduct = 2
  density = 1
  expand = 3
  formula = G4_M3_WAX
  name = G4_M3_WAX
  specific = 4
FEATURE [App::DocumentObjectGroupPython] Mg_element005  label="Mg_element : 1"  # scripted group (container) (typed FeaturePython)
  n = 1
  ref = Mg_element
FEATURE [App::DocumentObjectGroupPython] C_element058  label="C_element : 031"  # scripted group (container) (typed FeaturePython)
  n = 1
  ref = C_element
FEATURE [App::DocumentObjectGroupPython] O_element059  label="O_element : 030"  # scripted group (container) (typed FeaturePython)
  n = 3
  ref = O_element
FEATURE [App::DocumentObjectGroupPython] G4_MAGNESIUM_CARBONATE  # scripted group (container) (typed FeaturePython)
  Dunit = g/cm3
  Dvalue = 2.958
  Group = -> [Mg_element005,C_element058,O_element059]
  conduct = 2
  density = 1
  expand = 3
  formula = G4_MAGNESIUM_CARBONATE
  name = G4_MAGNESIUM_CARBONATE
  specific = 4
FEATURE [App::DocumentObjectGroupPython] Mg_element006  label="Mg_element : 002"  # scripted group (container) (typed FeaturePython)
  n = 1
  ref = Mg_element
FEATURE [App::DocumentObjectGroupPython] F_element013  label="F_element : 005"  # scripted group (container) (typed FeaturePython)
  n = 2
  ref = F_element
FEATURE [App::DocumentObjectGroupPython] G4_MAGNESIUM_FLUORIDE  # scripted group (container) (typed FeaturePython)
  Dunit = g/cm3
  Dvalue = 3
  Group = -> [Mg_element006,F_element013]
  conduct = 2
  density = 1
  expand = 3
  formula = G4_MAGNESIUM_FLUORIDE
  name = G4_MAGNESIUM_FLUORIDE
  specific = 4
FEATURE [App::DocumentObjectGroupPython] Mg_element007  label="Mg_element : 003"  # scripted group (container) (typed FeaturePython)
  n = 1
  ref = Mg_element
FEATURE [App::DocumentObjectGroupPython] O_element060  label="O_element : 031"  # scripted group (container) (typed FeaturePython)
  n = 1
  ref = O_element
FEATURE [App::DocumentObjectGroupPython] G4_MAGNESIUM_OXIDE  # scripted group (container) (typed FeaturePython)
  Dunit = g/cm3
  Dvalue = 3.58
  Group = -> [Mg_element007,O_element060]
  conduct = 2
  density = 1
  expand = 3
  formula = G4_MAGNESIUM_OXIDE
  name = G4_MAGNESIUM_OXIDE
  specific = 4
FEATURE [App::DocumentObjectGroupPython] Mg_element008  label="Mg_element : 004"  # scripted group (container) (typed FeaturePython)
  n = 1
  ref = Mg_element
FEATURE [App::DocumentObjectGroupPython] B_element006  label="B_element : 006"  # scripted group (container) (typed FeaturePython)
  n = 4
  ref = B_element
FEATURE [App::DocumentObjectGroupPython] O_element061  label="O_element : 032"  # scripted group (container) (typed FeaturePython)
  n = 7
  ref = O_element
FEATURE [App::DocumentObjectGroupPython] G4_MAGNESIUM_TETRABORATE  # scripted group (container) (typed FeaturePython)
  Dunit = g/cm3
  Dvalue = 2.53
  Group = -> [Mg_element008,B_element006,O_element061]
  conduct = 2
  density = 1
  expand = 3
  formula = G4_MAGNESIUM_TETRABORATE
  name = G4_MAGNESIUM_TETRABORATE
  specific = 4
FEATURE [App::DocumentObjectGroupPython] Hg_element001  label="Hg_element : 1"  # scripted group (container) (typed FeaturePython)
  n = 1
  ref = Hg_element
FEATURE [App::DocumentObjectGroupPython] I_element004  label="I_element : 2"  # scripted group (container) (typed FeaturePython)
  n = 2
  ref = I_element
FEATURE [App::DocumentObjectGroupPython] G4_MERCURIC_IODIDE  # scripted group (container) (typed FeaturePython)
  Dunit = g/cm3
  Dvalue = 6.36
  Group = -> [Hg_element001,I_element004]
  conduct = 2
  density = 1
  expand = 3
  formula = G4_MERCURIC_IODIDE
  name = G4_MERCURIC_IODIDE
  specific = 4
FEATURE [App::DocumentObjectGroupPython] C_element059  label="C_element : 032"  # scripted group (container) (typed FeaturePython)
  n = 1
  ref = C_element
FEATURE [App::DocumentObjectGroupPython] H_element053  label="H_element : 028"  # scripted group (container) (typed FeaturePython)
  n = 4
  ref = H_element
FEATURE [App::DocumentObjectGroupPython] G4_METHANE  # scripted group (container) (typed FeaturePython)
  Dunit = g/cm3
  Dvalue = 0.000667151
  Group = -> [C_element059,H_element053]
  conduct = 2
  density = 1
  expand = 3
  formula = G4_METHANE
  name = G4_METHANE
  specific = 4
FEATURE [App::DocumentObjectGroupPython] C_element060  label="C_element : 033"  # scripted group (container) (typed FeaturePython)
  n = 1
  ref = C_element
FEATURE [App::DocumentObjectGroupPython] H_element054  label="H_element : 029"  # scripted group (container) (typed FeaturePython)
  n = 4
  ref = H_element
FEATURE [App::DocumentObjectGroupPython] O_element062  label="O_element : 033"  # scripted group (container) (typed FeaturePython)
  n = 1
  ref = O_element
FEATURE [App::DocumentObjectGroupPython] G4_METHANOL  # scripted group (container) (typed FeaturePython)
  Dunit = g/cm3
  Dvalue = 0.7914
  Group = -> [C_element060,H_element054,O_element062]
  conduct = 2
  density = 1
  expand = 3
  formula = G4_METHANOL
  name = G4_METHANOL
  specific = 4
FEATURE [App::DocumentObjectGroupPython] H_element055  label="H_element : 0.134"  # scripted group (container) (typed FeaturePython)
  n = 0.13404
FEATURE [App::DocumentObjectGroupPython] C_element061  label="C_element : 0.778"  # scripted group (container) (typed FeaturePython)
  n = 0.77796
FEATURE [App::DocumentObjectGroupPython] O_element063  label="O_element : 0.035"  # scripted group (container) (typed FeaturePython)
  n = 0.03502
FEATURE [App::DocumentObjectGroupPython] Mg_element009  label="Mg_element : 0.039"  # scripted group (container) (typed FeaturePython)
  n = 0.038594
FEATURE [App::DocumentObjectGroupPython] Ti_element002  label="Ti_element : 0.014"  # scripted group (container) (typed FeaturePython)
  n = 0.014386
FEATURE [App::DocumentObjectGroupPython] G4_MIX_D_WAX  # scripted group (container) (typed FeaturePython)
  Dunit = g/cm3
  Dvalue = 0.99
  Group = -> [H_element055,C_element061,O_element063,Mg_element009,Ti_element002]
  conduct = 2
  density = 1
  expand = 3
  formula = G4_MIX_D_WAX
  name = G4_MIX_D_WAX
  specific = 4
FEATURE [App::DocumentObjectGroupPython] H_element056  label="H_element : 0.135"  # scripted group (container) (typed FeaturePython)
  n = 0.081192
FEATURE [App::DocumentObjectGroupPython] C_element062  label="C_element : 0.583"  # scripted group (container) (typed FeaturePython)
  n = 0.583442
FEATURE [App::DocumentObjectGroupPython] N_element024  label="N_element : 0.018"  # scripted group (container) (typed FeaturePython)
  n = 0.017798
FEATURE [App::DocumentObjectGroupPython] O_element064  label="O_element : 0.186"  # scripted group (container) (typed FeaturePython)
  n = 0.186381
FEATURE [App::DocumentObjectGroupPython] Mg_element010  label="Mg_element : 0.130"  # scripted group (container) (typed FeaturePython)
  n = 0.130287
FEATURE [App::DocumentObjectGroupPython] Cl_element015  label="Cl_element : 0.588"  # scripted group (container) (typed FeaturePython)
  n = 0.0009
FEATURE [App::DocumentObjectGroupPython] G4_MS20_TISSUE  # scripted group (container) (typed FeaturePython)
  Dunit = g/cm3
  Dvalue = 1
  Group = -> [H_element056,C_element062,N_element024,O_element064,Mg_element010,Cl_element015]
  conduct = 2
  density = 1
  expand = 3
  formula = G4_MS20_TISSUE
  name = G4_MS20_TISSUE
  specific = 4
FEATURE [App::DocumentObjectGroupPython] H_element057  label="H_element : 0.136"  # scripted group (container) (typed FeaturePython)
  n = 0.102
FEATURE [App::DocumentObjectGroupPython] C_element063  label="C_element : 0.143"  # scripted group (container) (typed FeaturePython)
  n = 0.143
FEATURE [App::DocumentObjectGroupPython] N_element025  label="N_element : 0.034"  # scripted group (container) (typed FeaturePython)
  n = 0.034
FEATURE [App::DocumentObjectGroupPython] O_element065  label="O_element : 0.710"  # scripted group (container) (typed FeaturePython)
  n = 0.71
FEATURE [App::DocumentObjectGroupPython] Na_element011  label="Na_element : 0.098"  # scripted group (container) (typed FeaturePython)
  n = 0.001
FEATURE [App::DocumentObjectGroupPython] P_element007  label="P_element : 0.002"  # scripted group (container) (typed FeaturePython)
  n = 0.002
FEATURE [App::DocumentObjectGroupPython] S_element017  label="S_element : 0.018"  # scripted group (container) (typed FeaturePython)
  n = 0.003
FEATURE [App::DocumentObjectGroupPython] Cl_element016  label="Cl_element : 0.589"  # scripted group (container) (typed FeaturePython)
  n = 0.001
FEATURE [App::DocumentObjectGroupPython] K_element006  label="K_element : 0.004"  # scripted group (container) (typed FeaturePython)
  n = 0.004
FEATURE [App::DocumentObjectGroupPython] G4_MUSCLE_SKELETAL_ICRP  # scripted group (container) (typed FeaturePython)
  Dunit = g/cm3
  Dvalue = 1.05
  Group = -> [H_element057,C_element063,N_element025,O_element065,Na_element011,P_element007,S_element017,Cl_element016,K_element006]
  conduct = 2
  density = 1
  expand = 3
  formula = G4_MUSCLE_SKELETAL_ICRP
  name = G4_MUSCLE_SKELETAL_ICRP
  specific = 4
FEATURE [App::DocumentObjectGroupPython] H_element058  label="H_element : 0.137"  # scripted group (container) (typed FeaturePython)
  n = 0.102102
FEATURE [App::DocumentObjectGroupPython] C_element064  label="C_element : 0.123"  # scripted group (container) (typed FeaturePython)
  n = 0.123123
FEATURE [App::DocumentObjectGroupPython] N_element026  label="N_element : 0.756"  # scripted group (container) (typed FeaturePython)
  n = 0.035035
FEATURE [App::DocumentObjectGroupPython] O_element066  label="O_element : 0.730"  # scripted group (container) (typed FeaturePython)
  n = 0.72973
FEATURE [App::DocumentObjectGroupPython] Na_element012  label="Na_element : 0.099"  # scripted group (container) (typed FeaturePython)
  n = 0.001001
FEATURE [App::DocumentObjectGroupPython] P_element008  label="P_element : 0.106"  # scripted group (container) (typed FeaturePython)
  n = 0.002002
FEATURE [App::DocumentObjectGroupPython] S_element018  label="S_element : 0.019"  # scripted group (container) (typed FeaturePython)
  n = 0.004004
FEATURE [App::DocumentObjectGroupPython] K_element007  label="K_element : 0.016"  # scripted group (container) (typed FeaturePython)
  n = 0.003003
FEATURE [App::DocumentObjectGroupPython] G4_MUSCLE_STRIATED_ICRU  # scripted group (container) (typed FeaturePython)
  Dunit = g/cm3
  Dvalue = 1.04
  Group = -> [H_element058,C_element064,N_element026,O_element066,Na_element012,P_element008,S_element018,K_element007]
  conduct = 2
  density = 1
  expand = 3
  formula = G4_MUSCLE_STRIATED_ICRU
  name = G4_MUSCLE_STRIATED_ICRU
  specific = 4
FEATURE [App::DocumentObjectGroupPython] H_element059  label="H_element : 0.098"  # scripted group (container) (typed FeaturePython)
  n = 0.0982341
FEATURE [App::DocumentObjectGroupPython] C_element065  label="C_element : 0.156"  # scripted group (container) (typed FeaturePython)
  n = 0.156214
FEATURE [App::DocumentObjectGroupPython] N_element027  label="N_element : 0.757"  # scripted group (container) (typed FeaturePython)
  n = 0.035451
FEATURE [App::DocumentObjectGroupPython] O_element067  label="O_element : 0.880"  # scripted group (container) (typed FeaturePython)
  n = 0.710101
FEATURE [App::DocumentObjectGroupPython] G4_MUSCLE_WITH_SUCROSE  # scripted group (container) (typed FeaturePython)
  Dunit = g/cm3
  Dvalue = 1.11
  Group = -> [H_element059,C_element065,N_element027,O_element067]
  conduct = 2
  density = 1
  expand = 3
  formula = G4_MUSCLE_WITH_SUCROSE
  name = G4_MUSCLE_WITH_SUCROSE
  specific = 4
FEATURE [App::DocumentObjectGroupPython] H_element060  label="H_element : 0.138"  # scripted group (container) (typed FeaturePython)
  n = 0.101969
FEATURE [App::DocumentObjectGroupPython] C_element066  label="C_element : 0.120"  # scripted group (container) (typed FeaturePython)
  n = 0.120058
FEATURE [App::DocumentObjectGroupPython] N_element028  label="N_element : 0.758"  # scripted group (container) (typed FeaturePython)
  n = 0.035451
FEATURE [App::DocumentObjectGroupPython] O_element068  label="O_element : 0.743"  # scripted group (container) (typed FeaturePython)
  n = 0.742522
FEATURE [App::DocumentObjectGroupPython] G4_MUSCLE_WITHOUT_SUCROSE  # scripted group (container) (typed FeaturePython)
  Dunit = g/cm3
  Dvalue = 1.07
  Group = -> [H_element060,C_element066,N_element028,O_element068]
  conduct = 2
  density = 1
  expand = 3
  formula = G4_MUSCLE_WITHOUT_SUCROSE
  name = G4_MUSCLE_WITHOUT_SUCROSE
  specific = 4
FEATURE [App::DocumentObjectGroupPython] C_element067  label="C_element : 10"  # scripted group (container) (typed FeaturePython)
  n = 10
  ref = C_element
FEATURE [App::DocumentObjectGroupPython] H_element061  label="H_element : 030"  # scripted group (container) (typed FeaturePython)
  n = 8
  ref = H_element
FEATURE [App::DocumentObjectGroupPython] G4_NAPHTHALENE  # scripted group (container) (typed FeaturePython)
  Dunit = g/cm3
  Dvalue = 1.145
  Group = -> [C_element067,H_element061]
  conduct = 2
  density = 1
  expand = 3
  formula = G4_NAPHTHALENE
  name = G4_NAPHTHALENE
  specific = 4
FEATURE [App::DocumentObjectGroupPython] C_element068  label="C_element : 034"  # scripted group (container) (typed FeaturePython)
  n = 6
  ref = C_element
FEATURE [App::DocumentObjectGroupPython] H_element062  label="H_element : 031"  # scripted group (container) (typed FeaturePython)
  n = 5
  ref = H_element
FEATURE [App::DocumentObjectGroupPython] N_element029  label="N_element : 012"  # scripted group (container) (typed FeaturePython)
  n = 1
  ref = N_element
FEATURE [App::DocumentObjectGroupPython] O_element069  label="O_element : 034"  # scripted group (container) (typed FeaturePython)
  n = 2
  ref = O_element
FEATURE [App::DocumentObjectGroupPython] G4_NITROBENZENE  # scripted group (container) (typed FeaturePython)
  Dunit = g/cm3
  Dvalue = 1.19867
  Group = -> [C_element068,H_element062,N_element029,O_element069]
  conduct = 2
  density = 1
  expand = 3
  formula = G4_NITROBENZENE
  name = G4_NITROBENZENE
  specific = 4
FEATURE [App::DocumentObjectGroupPython] N_element030  label="N_element : 013"  # scripted group (container) (typed FeaturePython)
  n = 2
  ref = N_element
FEATURE [App::DocumentObjectGroupPython] O_element070  label="O_element : 035"  # scripted group (container) (typed FeaturePython)
  n = 1
  ref = O_element
FEATURE [App::DocumentObjectGroupPython] G4_NITROUS_OXIDE  # scripted group (container) (typed FeaturePython)
  Dunit = g/cm3
  Dvalue = 0.00183094
  Group = -> [N_element030,O_element070]
  conduct = 2
  density = 1
  expand = 3
  formula = G4_NITROUS_OXIDE
  name = G4_NITROUS_OXIDE
  specific = 4
FEATURE [App::DocumentObjectGroupPython] H_element063  label="H_element : 0.104"  # scripted group (container) (typed FeaturePython)
  n = 0.103509
FEATURE [App::DocumentObjectGroupPython] C_element069  label="C_element : 0.648"  # scripted group (container) (typed FeaturePython)
  n = 0.648416
FEATURE [App::DocumentObjectGroupPython] N_element031  label="N_element : 0.100"  # scripted group (container) (typed FeaturePython)
  n = 0.0995361
FEATURE [App::DocumentObjectGroupPython] O_element071  label="O_element : 0.149"  # scripted group (container) (typed FeaturePython)
  n = 0.148539
FEATURE [App::DocumentObjectGroupPython] G4_NYLON_8062  label="G4_NYLON-8062"  # scripted group (container) (typed FeaturePython)
  Dunit = g/cm3
  Dvalue = 1.08
  Group = -> [H_element063,C_element069,N_element031,O_element071]
  conduct = 2
  density = 1
  expand = 3
  formula = G4_NYLON-8062
  name = G4_NYLON-8062
  specific = 4
FEATURE [App::DocumentObjectGroupPython] C_element070  label="C_element : 035"  # scripted group (container) (typed FeaturePython)
  n = 6
  ref = C_element
FEATURE [App::DocumentObjectGroupPython] H_element064  label="H_element : 11"  # scripted group (container) (typed FeaturePython)
  n = 11
  ref = H_element
FEATURE [App::DocumentObjectGroupPython] N_element032  label="N_element : 014"  # scripted group (container) (typed FeaturePython)
  n = 1
  ref = N_element
FEATURE [App::DocumentObjectGroupPython] O_element072  label="O_element : 036"  # scripted group (container) (typed FeaturePython)
  n = 1
  ref = O_element
FEATURE [App::DocumentObjectGroupPython] G4_NYLON_6_6  label="G4_NYLON-6-6"  # scripted group (container) (typed FeaturePython)
  Dunit = g/cm3
  Dvalue = 1.14
  Group = -> [C_element070,H_element064,N_element032,O_element072]
  conduct = 2
  density = 1
  expand = 3
  formula = G4_NYLON-6-6
  name = G4_NYLON-6-6
  specific = 4
FEATURE [App::DocumentObjectGroupPython] H_element065  label="H_element : 0.139"  # scripted group (container) (typed FeaturePython)
  n = 0.107062
FEATURE [App::DocumentObjectGroupPython] C_element071  label="C_element : 0.680"  # scripted group (container) (typed FeaturePython)
  n = 0.680449
FEATURE [App::DocumentObjectGroupPython] N_element033  label="N_element : 0.099"  # scripted group (container) (typed FeaturePython)
  n = 0.099189
FEATURE [App::DocumentObjectGroupPython] O_element073  label="O_element : 0.113"  # scripted group (container) (typed FeaturePython)
  n = 0.1133
FEATURE [App::DocumentObjectGroupPython] G4_NYLON_6_10  label="G4_NYLON-6-10"  # scripted group (container) (typed FeaturePython)
  Dunit = g/cm3
  Dvalue = 1.14
  Group = -> [H_element065,C_element071,N_element033,O_element073]
  conduct = 2
  density = 1
  expand = 3
  formula = G4_NYLON-6-10
  name = G4_NYLON-6-10
  specific = 4
FEATURE [App::DocumentObjectGroupPython] H_element066  label="H_element : 0.140"  # scripted group (container) (typed FeaturePython)
  n = 0.115476
FEATURE [App::DocumentObjectGroupPython] C_element072  label="C_element : 0.721"  # scripted group (container) (typed FeaturePython)
  n = 0.720818
FEATURE [App::DocumentObjectGroupPython] N_element034  label="N_element : 0.076"  # scripted group (container) (typed FeaturePython)
  n = 0.0764169
FEATURE [App::DocumentObjectGroupPython] O_element074  label="O_element : 0.087"  # scripted group (container) (typed FeaturePython)
  n = 0.0872889
FEATURE [App::DocumentObjectGroupPython] G4_NYLON_11_RILSAN  label="G4_NYLON-11_RILSAN"  # scripted group (container) (typed FeaturePython)
  Dunit = g/cm3
  Dvalue = 1.425
  Group = -> [H_element066,C_element072,N_element034,O_element074]
  conduct = 2
  density = 1
  expand = 3
  formula = G4_NYLON-11_RILSAN
  name = G4_NYLON-11_RILSAN
  specific = 4
FEATURE [App::DocumentObjectGroupPython] C_element073  label="C_element : 8"  # scripted group (container) (typed FeaturePython)
  n = 8
  ref = C_element
FEATURE [App::DocumentObjectGroupPython] H_element067  label="H_element : 18"  # scripted group (container) (typed FeaturePython)
  n = 18
  ref = H_element
FEATURE [App::DocumentObjectGroupPython] G4_OCTANE  # scripted group (container) (typed FeaturePython)
  Dunit = g/cm3
  Dvalue = 0.7026
  Group = -> [C_element073,H_element067]
  conduct = 2
  density = 1
  expand = 3
  formula = G4_OCTANE
  name = G4_OCTANE
  specific = 4
FEATURE [App::DocumentObjectGroupPython] C_element074  label="C_element : 25"  # scripted group (container) (typed FeaturePython)
  n = 25
  ref = C_element
FEATURE [App::DocumentObjectGroupPython] H_element068  label="H_element : 52"  # scripted group (container) (typed FeaturePython)
  n = 52
  ref = H_element
FEATURE [App::DocumentObjectGroupPython] G4_PARAFFIN  # scripted group (container) (typed FeaturePython)
  Dunit = g/cm3
  Dvalue = 0.93
  Group = -> [C_element074,H_element068]
  conduct = 2
  density = 1
  expand = 3
  formula = G4_PARAFFIN
  name = G4_PARAFFIN
  specific = 4
FEATURE [App::DocumentObjectGroupPython] C_element075  label="C_element : 036"  # scripted group (container) (typed FeaturePython)
  n = 5
  ref = C_element
FEATURE [App::DocumentObjectGroupPython] H_element069  label="H_element : 032"  # scripted group (container) (typed FeaturePython)
  n = 12
  ref = H_element
FEATURE [App::DocumentObjectGroupPython] G4_N_PENTANE  label="G4_N-PENTANE"  # scripted group (container) (typed FeaturePython)
  Dunit = g/cm3
  Dvalue = 0.6262
  Group = -> [C_element075,H_element069]
  conduct = 2
  density = 1
  expand = 3
  formula = G4_N-PENTANE
  name = G4_N-PENTANE
  specific = 4
FEATURE [App::DocumentObjectGroupPython] H_element070  label="H_element : 0.014"  # scripted group (container) (typed FeaturePython)
  n = 0.0141
FEATURE [App::DocumentObjectGroupPython] C_element076  label="C_element : 0.072"  # scripted group (container) (typed FeaturePython)
  n = 0.072261
FEATURE [App::DocumentObjectGroupPython] N_element035  label="N_element : 0.019"  # scripted group (container) (typed FeaturePython)
  n = 0.01932
FEATURE [App::DocumentObjectGroupPython] O_element075  label="O_element : 0.066"  # scripted group (container) (typed FeaturePython)
  n = 0.066101
FEATURE [App::DocumentObjectGroupPython] S_element019  label="S_element : 0.020"  # scripted group (container) (typed FeaturePython)
  n = 0.00189
FEATURE [App::DocumentObjectGroupPython] Br_element004  label="Br_element : 0.349"  # scripted group (container) (typed FeaturePython)
  n = 0.349103
FEATURE [App::DocumentObjectGroupPython] Ag_element001  label="Ag_element : 0.474"  # scripted group (container) (typed FeaturePython)
  n = 0.474105
FEATURE [App::DocumentObjectGroupPython] I_element005  label="I_element : 0.003"  # scripted group (container) (typed FeaturePython)
  n = 0.00312
FEATURE [App::DocumentObjectGroupPython] G4_PHOTO_EMULSION  # scripted group (container) (typed FeaturePython)
  Dunit = g/cm3
  Dvalue = 3.815
  Group = -> [H_element070,C_element076,N_element035,O_element075,S_element019,Br_element004,Ag_element001,I_element005]
  conduct = 2
  density = 1
  expand = 3
  formula = G4_PHOTO_EMULSION
  name = G4_PHOTO_EMULSION
  specific = 4
FEATURE [App::DocumentObjectGroupPython] C_element077  label="C_element : 9"  # scripted group (container) (typed FeaturePython)
  n = 9
  ref = C_element
FEATURE [App::DocumentObjectGroupPython] H_element071  label="H_element : 033"  # scripted group (container) (typed FeaturePython)
  n = 10
  ref = H_element
FEATURE [App::DocumentObjectGroupPython] G4_PLASTIC_SC_VINYLTOLUENE  # scripted group (container) (typed FeaturePython)
  Dunit = g/cm3
  Dvalue = 1.032
  Group = -> [C_element077,H_element071]
  conduct = 2
  density = 1
  expand = 3
  formula = G4_PLASTIC_SC_VINYLTOLUENE
  name = G4_PLASTIC_SC_VINYLTOLUENE
  specific = 4
FEATURE [App::DocumentObjectGroupPython] Pu_element001  label="Pu_element : 1"  # scripted group (container) (typed FeaturePython)
  n = 1
  ref = Pu_element
FEATURE [App::DocumentObjectGroupPython] O_element076  label="O_element : 037"  # scripted group (container) (typed FeaturePython)
  n = 2
  ref = O_element
FEATURE [App::DocumentObjectGroupPython] G4_PLUTONIUM_DIOXIDE  # scripted group (container) (typed FeaturePython)
  Dunit = g/cm3
  Dvalue = 11.46
  Group = -> [Pu_element001,O_element076]
  conduct = 2
  density = 1
  expand = 3
  formula = G4_PLUTONIUM_DIOXIDE
  name = G4_PLUTONIUM_DIOXIDE
  specific = 4
FEATURE [App::DocumentObjectGroupPython] C_element078  label="C_element : 037"  # scripted group (container) (typed FeaturePython)
  n = 3
  ref = C_element
FEATURE [App::DocumentObjectGroupPython] H_element072  label="H_element : 034"  # scripted group (container) (typed FeaturePython)
  n = 3
  ref = H_element
FEATURE [App::DocumentObjectGroupPython] N_element036  label="N_element : 015"  # scripted group (container) (typed FeaturePython)
  n = 1
  ref = N_element
FEATURE [App::DocumentObjectGroupPython] G4_POLYACRYLONITRILE  # scripted group (container) (typed FeaturePython)
  Dunit = g/cm3
  Dvalue = 1.17
  Group = -> [C_element078,H_element072,N_element036]
  conduct = 2
  density = 1
  expand = 3
  formula = G4_POLYACRYLONITRILE
  name = G4_POLYACRYLONITRILE
  specific = 4
FEATURE [App::DocumentObjectGroupPython] C_element079  label="C_element : 16"  # scripted group (container) (typed FeaturePython)
  n = 16
  ref = C_element
FEATURE [App::DocumentObjectGroupPython] H_element073  label="H_element : 035"  # scripted group (container) (typed FeaturePython)
  n = 14
  ref = H_element
FEATURE [App::DocumentObjectGroupPython] O_element077  label="O_element : 038"  # scripted group (container) (typed FeaturePython)
  n = 3
  ref = O_element
FEATURE [App::DocumentObjectGroupPython] G4_POLYCARBONATE  # scripted group (container) (typed FeaturePython)
  Dunit = g/cm3
  Dvalue = 1.2
  Group = -> [C_element079,H_element073,O_element077]
  conduct = 2
  density = 1
  expand = 3
  formula = G4_POLYCARBONATE
  name = G4_POLYCARBONATE
  specific = 4
FEATURE [App::DocumentObjectGroupPython] C_element080  label="C_element : 038"  # scripted group (container) (typed FeaturePython)
  n = 8
  ref = C_element
FEATURE [App::DocumentObjectGroupPython] H_element074  label="H_element : 036"  # scripted group (container) (typed FeaturePython)
  n = 7
  ref = H_element
FEATURE [App::DocumentObjectGroupPython] Cl_element017  label="Cl_element : 007"  # scripted group (container) (typed FeaturePython)
  n = 1
  ref = Cl_element
FEATURE [App::DocumentObjectGroupPython] G4_POLYCHLOROSTYRENE  # scripted group (container) (typed FeaturePython)
  Dunit = g/cm3
  Dvalue = 1.3
  Group = -> [C_element080,H_element074,Cl_element017]
  conduct = 2
  density = 1
  expand = 3
  formula = G4_POLYCHLOROSTYRENE
  name = G4_POLYCHLOROSTYRENE
  specific = 4
FEATURE [App::DocumentObjectGroupPython] C_element081  label="C_element : 039"  # scripted group (container) (typed FeaturePython)
  n = 1
  ref = C_element
FEATURE [App::DocumentObjectGroupPython] H_element075  label="H_element : 037"  # scripted group (container) (typed FeaturePython)
  n = 2
  ref = H_element
FEATURE [App::DocumentObjectGroupPython] G4_POLYETHYLENE  # scripted group (container) (typed FeaturePython)
  Dunit = g/cm3
  Dvalue = 0.94
  Group = -> [C_element081,H_element075]
  conduct = 2
  density = 1
  expand = 3
  formula = G4_POLYETHYLENE
  name = G4_POLYETHYLENE
  specific = 4
FEATURE [App::DocumentObjectGroupPython] C_element082  label="C_element : 040"  # scripted group (container) (typed FeaturePython)
  n = 10
  ref = C_element
FEATURE [App::DocumentObjectGroupPython] H_element076  label="H_element : 038"  # scripted group (container) (typed FeaturePython)
  n = 8
  ref = H_element
FEATURE [App::DocumentObjectGroupPython] O_element078  label="O_element : 039"  # scripted group (container) (typed FeaturePython)
  n = 4
  ref = O_element
FEATURE [App::DocumentObjectGroupPython] G4_MYLAR  # scripted group (container) (typed FeaturePython)
  Dunit = g/cm3
  Dvalue = 1.4
  Group = -> [C_element082,H_element076,O_element078]
  conduct = 2
  density = 1
  expand = 3
  formula = G4_MYLAR
  name = G4_MYLAR
  specific = 4
FEATURE [App::DocumentObjectGroupPython] C_element083  label="C_element : 041"  # scripted group (container) (typed FeaturePython)
  n = 5
  ref = C_element
FEATURE [App::DocumentObjectGroupPython] H_element077  label="H_element : 039"  # scripted group (container) (typed FeaturePython)
  n = 8
  ref = H_element
FEATURE [App::DocumentObjectGroupPython] O_element079  label="O_element : 040"  # scripted group (container) (typed FeaturePython)
  n = 2
  ref = O_element
FEATURE [App::DocumentObjectGroupPython] G4_PLEXIGLASS  # scripted group (container) (typed FeaturePython)
  Dunit = g/cm3
  Dvalue = 1.19
  Group = -> [C_element083,H_element077,O_element079]
  conduct = 2
  density = 1
  expand = 3
  formula = G4_PLEXIGLASS
  name = G4_PLEXIGLASS
  specific = 4
FEATURE [App::DocumentObjectGroupPython] C_element084  label="C_element : 042"  # scripted group (container) (typed FeaturePython)
  n = 1
  ref = C_element
FEATURE [App::DocumentObjectGroupPython] H_element078  label="H_element : 040"  # scripted group (container) (typed FeaturePython)
  n = 2
  ref = H_element
FEATURE [App::DocumentObjectGroupPython] O_element080  label="O_element : 041"  # scripted group (container) (typed FeaturePython)
  n = 1
  ref = O_element
FEATURE [App::DocumentObjectGroupPython] G4_POLYOXYMETHYLENE  # scripted group (container) (typed FeaturePython)
  Dunit = g/cm3
  Dvalue = 1.425
  Group = -> [C_element084,H_element078,O_element080]
  conduct = 2
  density = 1
  expand = 3
  formula = G4_POLYOXYMETHYLENE
  name = G4_POLYOXYMETHYLENE
  specific = 4
FEATURE [App::DocumentObjectGroupPython] C_element085  label="C_element : 043"  # scripted group (container) (typed FeaturePython)
  n = 2
  ref = C_element
FEATURE [App::DocumentObjectGroupPython] H_element079  label="H_element : 041"  # scripted group (container) (typed FeaturePython)
  n = 4
  ref = H_element
FEATURE [App::DocumentObjectGroupPython] G4_POLYPROPYLENE  # scripted group (container) (typed FeaturePython)
  Dunit = g/cm3
  Dvalue = 0.9
  Group = -> [C_element085,H_element079]
  conduct = 2
  density = 1
  expand = 3
  formula = G4_POLYPROPYLENE
  name = G4_POLYPROPYLENE
  specific = 4
FEATURE [App::DocumentObjectGroupPython] C_element086  label="C_element : 044"  # scripted group (container) (typed FeaturePython)
  n = 8
  ref = C_element
FEATURE [App::DocumentObjectGroupPython] H_element080  label="H_element : 042"  # scripted group (container) (typed FeaturePython)
  n = 8
  ref = H_element
FEATURE [App::DocumentObjectGroupPython] G4_POLYSTYRENE  # scripted group (container) (typed FeaturePython)
  Dunit = g/cm3
  Dvalue = 1.06
  Group = -> [C_element086,H_element080]
  conduct = 2
  density = 1
  expand = 3
  formula = G4_POLYSTYRENE
  name = G4_POLYSTYRENE
  specific = 4
FEATURE [App::DocumentObjectGroupPython] C_element087  label="C_element : 045"  # scripted group (container) (typed FeaturePython)
  n = 2
  ref = C_element
FEATURE [App::DocumentObjectGroupPython] F_element014  label="F_element : 4"  # scripted group (container) (typed FeaturePython)
  n = 4
  ref = F_element
FEATURE [App::DocumentObjectGroupPython] G4_TEFLON  # scripted group (container) (typed FeaturePython)
  Dunit = g/cm3
  Dvalue = 2.2
  Group = -> [C_element087,F_element014]
  conduct = 2
  density = 1
  expand = 3
  formula = G4_TEFLON
  name = G4_TEFLON
  specific = 4
FEATURE [App::DocumentObjectGroupPython] C_element088  label="C_element : 046"  # scripted group (container) (typed FeaturePython)
  n = 2
  ref = C_element
FEATURE [App::DocumentObjectGroupPython] F_element015  label="F_element : 006"  # scripted group (container) (typed FeaturePython)
  n = 3
  ref = F_element
FEATURE [App::DocumentObjectGroupPython] Cl_element018  label="Cl_element : 008"  # scripted group (container) (typed FeaturePython)
  n = 1
  ref = Cl_element
FEATURE [App::DocumentObjectGroupPython] G4_POLYTRIFLUOROCHLOROETHYLENE  # scripted group (container) (typed FeaturePython)
  Dunit = g/cm3
  Dvalue = 2.1
  Group = -> [C_element088,F_element015,Cl_element018]
  conduct = 2
  density = 1
  expand = 3
  formula = G4_POLYTRIFLUOROCHLOROETHYLENE
  name = G4_POLYTRIFLUOROCHLOROETHYLENE
  specific = 4
FEATURE [App::DocumentObjectGroupPython] C_element089  label="C_element : 047"  # scripted group (container) (typed FeaturePython)
  n = 4
  ref = C_element
FEATURE [App::DocumentObjectGroupPython] H_element081  label="H_element : 043"  # scripted group (container) (typed FeaturePython)
  n = 6
  ref = H_element
FEATURE [App::DocumentObjectGroupPython] O_element081  label="O_element : 042"  # scripted group (container) (typed FeaturePython)
  n = 2
  ref = O_element
FEATURE [App::DocumentObjectGroupPython] G4_POLYVINYL_ACETATE  # scripted group (container) (typed FeaturePython)
  Dunit = g/cm3
  Dvalue = 1.19
  Group = -> [C_element089,H_element081,O_element081]
  conduct = 2
  density = 1
  expand = 3
  formula = G4_POLYVINYL_ACETATE
  name = G4_POLYVINYL_ACETATE
  specific = 4
FEATURE [App::DocumentObjectGroupPython] C_element090  label="C_element : 048"  # scripted group (container) (typed FeaturePython)
  n = 2
  ref = C_element
FEATURE [App::DocumentObjectGroupPython] H_element082  label="H_element : 044"  # scripted group (container) (typed FeaturePython)
  n = 4
  ref = H_element
FEATURE [App::DocumentObjectGroupPython] O_element082  label="O_element : 043"  # scripted group (container) (typed FeaturePython)
  n = 1
  ref = O_element
FEATURE [App::DocumentObjectGroupPython] G4_POLYVINYL_ALCOHOL  # scripted group (container) (typed FeaturePython)
  Dunit = g/cm3
  Dvalue = 1.3
  Group = -> [C_element090,H_element082,O_element082]
  conduct = 2
  density = 1
  expand = 3
  formula = G4_POLYVINYL_ALCOHOL
  name = G4_POLYVINYL_ALCOHOL
  specific = 4
FEATURE [App::DocumentObjectGroupPython] C_element091  label="C_element : 049"  # scripted group (container) (typed FeaturePython)
  n = 8
  ref = C_element
FEATURE [App::DocumentObjectGroupPython] H_element083  label="H_element : 045"  # scripted group (container) (typed FeaturePython)
  n = 14
  ref = H_element
FEATURE [App::DocumentObjectGroupPython] O_element083  label="O_element : 044"  # scripted group (container) (typed FeaturePython)
  n = 2
  ref = O_element
FEATURE [App::DocumentObjectGroupPython] G4_POLYVINYL_BUTYRAL  # scripted group (container) (typed FeaturePython)
  Dunit = g/cm3
  Dvalue = 1.12
  Group = -> [C_element091,H_element083,O_element083]
  conduct = 2
  density = 1
  expand = 3
  formula = G4_POLYVINYL_BUTYRAL
  name = G4_POLYVINYL_BUTYRAL
  specific = 4
FEATURE [App::DocumentObjectGroupPython] C_element092  label="C_element : 050"  # scripted group (container) (typed FeaturePython)
  n = 2
  ref = C_element
FEATURE [App::DocumentObjectGroupPython] H_element084  label="H_element : 046"  # scripted group (container) (typed FeaturePython)
  n = 3
  ref = H_element
FEATURE [App::DocumentObjectGroupPython] Cl_element019  label="Cl_element : 009"  # scripted group (container) (typed FeaturePython)
  n = 1
  ref = Cl_element
FEATURE [App::DocumentObjectGroupPython] G4_POLYVINYL_CHLORIDE  # scripted group (container) (typed FeaturePython)
  Dunit = g/cm3
  Dvalue = 1.3
  Group = -> [C_element092,H_element084,Cl_element019]
  conduct = 2
  density = 1
  expand = 3
  formula = G4_POLYVINYL_CHLORIDE
  name = G4_POLYVINYL_CHLORIDE
  specific = 4
FEATURE [App::DocumentObjectGroupPython] C_element093  label="C_element : 051"  # scripted group (container) (typed FeaturePython)
  n = 2
  ref = C_element
FEATURE [App::DocumentObjectGroupPython] H_element085  label="H_element : 047"  # scripted group (container) (typed FeaturePython)
  n = 2
  ref = H_element
FEATURE [App::DocumentObjectGroupPython] Cl_element020  label="Cl_element : 010"  # scripted group (container) (typed FeaturePython)
  n = 2
  ref = Cl_element
FEATURE [App::DocumentObjectGroupPython] G4_POLYVINYLIDENE_CHLORIDE  # scripted group (container) (typed FeaturePython)
  Dunit = g/cm3
  Dvalue = 1.7
  Group = -> [C_element093,H_element085,Cl_element020]
  conduct = 2
  density = 1
  expand = 3
  formula = G4_POLYVINYLIDENE_CHLORIDE
  name = G4_POLYVINYLIDENE_CHLORIDE
  specific = 4
FEATURE [App::DocumentObjectGroupPython] C_element094  label="C_element : 052"  # scripted group (container) (typed FeaturePython)
  n = 2
  ref = C_element
FEATURE [App::DocumentObjectGroupPython] H_element086  label="H_element : 048"  # scripted group (container) (typed FeaturePython)
  n = 2
  ref = H_element
FEATURE [App::DocumentObjectGroupPython] F_element016  label="F_element : 007"  # scripted group (container) (typed FeaturePython)
  n = 2
  ref = F_element
FEATURE [App::DocumentObjectGroupPython] G4_POLYVINYLIDENE_FLUORIDE  # scripted group (container) (typed FeaturePython)
  Dunit = g/cm3
  Dvalue = 1.76
  Group = -> [C_element094,H_element086,F_element016]
  conduct = 2
  density = 1
  expand = 3
  formula = G4_POLYVINYLIDENE_FLUORIDE
  name = G4_POLYVINYLIDENE_FLUORIDE
  specific = 4
FEATURE [App::DocumentObjectGroupPython] C_element095  label="C_element : 053"  # scripted group (container) (typed FeaturePython)
  n = 6
  ref = C_element
FEATURE [App::DocumentObjectGroupPython] H_element087  label="H_element : 9"  # scripted group (container) (typed FeaturePython)
  n = 9
  ref = H_element
FEATURE [App::DocumentObjectGroupPython] N_element037  label="N_element : 016"  # scripted group (container) (typed FeaturePython)
  n = 1
  ref = N_element
FEATURE [App::DocumentObjectGroupPython] O_element084  label="O_element : 045"  # scripted group (container) (typed FeaturePython)
  n = 1
  ref = O_element
FEATURE [App::DocumentObjectGroupPython] G4_POLYVINYL_PYRROLIDONE  # scripted group (container) (typed FeaturePython)
  Dunit = g/cm3
  Dvalue = 1.25
  Group = -> [C_element095,H_element087,N_element037,O_element084]
  conduct = 2
  density = 1
  expand = 3
  formula = G4_POLYVINYL_PYRROLIDONE
  name = G4_POLYVINYL_PYRROLIDONE
  specific = 4
FEATURE [App::DocumentObjectGroupPython] K_element008  label="K_element : 1"  # scripted group (container) (typed FeaturePython)
  n = 1
  ref = K_element
FEATURE [App::DocumentObjectGroupPython] I_element006  label="I_element : 003"  # scripted group (container) (typed FeaturePython)
  n = 1
  ref = I_element
FEATURE [App::DocumentObjectGroupPython] G4_POTASSIUM_IODIDE  # scripted group (container) (typed FeaturePython)
  Dunit = g/cm3
  Dvalue = 3.13
  Group = -> [K_element008,I_element006]
  conduct = 2
  density = 1
  expand = 3
  formula = G4_POTASSIUM_IODIDE
  name = G4_POTASSIUM_IODIDE
  specific = 4
FEATURE [App::DocumentObjectGroupPython] K_element009  label="K_element : 2"  # scripted group (container) (typed FeaturePython)
  n = 2
  ref = K_element
FEATURE [App::DocumentObjectGroupPython] O_element085  label="O_element : 046"  # scripted group (container) (typed FeaturePython)
  n = 1
  ref = O_element
FEATURE [App::DocumentObjectGroupPython] G4_POTASSIUM_OXIDE  # scripted group (container) (typed FeaturePython)
  Dunit = g/cm3
  Dvalue = 2.32
  Group = -> [K_element009,O_element085]
  conduct = 2
  density = 1
  expand = 3
  formula = G4_POTASSIUM_OXIDE
  name = G4_POTASSIUM_OXIDE
  specific = 4
FEATURE [App::DocumentObjectGroupPython] C_element096  label="C_element : 054"  # scripted group (container) (typed FeaturePython)
  n = 3
  ref = C_element
FEATURE [App::DocumentObjectGroupPython] H_element088  label="H_element : 049"  # scripted group (container) (typed FeaturePython)
  n = 8
  ref = H_element
FEATURE [App::DocumentObjectGroupPython] G4_PROPANE  # scripted group (container) (typed FeaturePython)
  Dunit = g/cm3
  Dvalue = 0.00187939
  Group = -> [C_element096,H_element088]
  conduct = 2
  density = 1
  expand = 3
  formula = G4_PROPANE
  name = G4_PROPANE
  specific = 4
FEATURE [App::DocumentObjectGroupPython] C_element097  label="C_element : 055"  # scripted group (container) (typed FeaturePython)
  n = 3
  ref = C_element
FEATURE [App::DocumentObjectGroupPython] H_element089  label="H_element : 050"  # scripted group (container) (typed FeaturePython)
  n = 8
  ref = H_element
FEATURE [App::DocumentObjectGroupPython] G4_lPROPANE  # scripted group (container) (typed FeaturePython)
  Dunit = g/cm3
  Dvalue = 0.43
  Group = -> [C_element097,H_element089]
  conduct = 2
  density = 1
  expand = 3
  formula = G4_lPROPANE
  name = G4_lPROPANE
  specific = 4
FEATURE [App::DocumentObjectGroupPython] C_element098  label="C_element : 056"  # scripted group (container) (typed FeaturePython)
  n = 3
  ref = C_element
FEATURE [App::DocumentObjectGroupPython] H_element090  label="H_element : 051"  # scripted group (container) (typed FeaturePython)
  n = 8
  ref = H_element
FEATURE [App::DocumentObjectGroupPython] O_element086  label="O_element : 047"  # scripted group (container) (typed FeaturePython)
  n = 1
  ref = O_element
FEATURE [App::DocumentObjectGroupPython] G4_N_PROPYL_ALCOHOL  label="G4_N-PROPYL_ALCOHOL"  # scripted group (container) (typed FeaturePython)
  Dunit = g/cm3
  Dvalue = 0.8035
  Group = -> [C_element098,H_element090,O_element086]
  conduct = 2
  density = 1
  expand = 3
  formula = G4_N-PROPYL_ALCOHOL
  name = G4_N-PROPYL_ALCOHOL
  specific = 4
FEATURE [App::DocumentObjectGroupPython] C_element099  label="C_element : 057"  # scripted group (container) (typed FeaturePython)
  n = 5
  ref = C_element
FEATURE [App::DocumentObjectGroupPython] H_element091  label="H_element : 052"  # scripted group (container) (typed FeaturePython)
  n = 5
  ref = H_element
FEATURE [App::DocumentObjectGroupPython] N_element038  label="N_element : 017"  # scripted group (container) (typed FeaturePython)
  n = 1
  ref = N_element
FEATURE [App::DocumentObjectGroupPython] G4_PYRIDINE  # scripted group (container) (typed FeaturePython)
  Dunit = g/cm3
  Dvalue = 0.9819
  Group = -> [C_element099,H_element091,N_element038]
  conduct = 2
  density = 1
  expand = 3
  formula = G4_PYRIDINE
  name = G4_PYRIDINE
  specific = 4
FEATURE [App::DocumentObjectGroupPython] H_element092  label="H_element : 0.144"  # scripted group (container) (typed FeaturePython)
  n = 0.143711
FEATURE [App::DocumentObjectGroupPython] C_element100  label="C_element : 0.856"  # scripted group (container) (typed FeaturePython)
  n = 0.856289
FEATURE [App::DocumentObjectGroupPython] G4_RUBBER_BUTYL  # scripted group (container) (typed FeaturePython)
  Dunit = g/cm3
  Dvalue = 0.92
  Group = -> [H_element092,C_element100]
  conduct = 2
  density = 1
  expand = 3
  formula = G4_RUBBER_BUTYL
  name = G4_RUBBER_BUTYL
  specific = 4
FEATURE [App::DocumentObjectGroupPython] H_element093  label="H_element : 0.118"  # scripted group (container) (typed FeaturePython)
  n = 0.118371
FEATURE [App::DocumentObjectGroupPython] C_element101  label="C_element : 0.882"  # scripted group (container) (typed FeaturePython)
  n = 0.881629
FEATURE [App::DocumentObjectGroupPython] G4_RUBBER_NATURAL  # scripted group (container) (typed FeaturePython)
  Dunit = g/cm3
  Dvalue = 0.92
  Group = -> [H_element093,C_element101]
  conduct = 2
  density = 1
  expand = 3
  formula = G4_RUBBER_NATURAL
  name = G4_RUBBER_NATURAL
  specific = 4
FEATURE [App::DocumentObjectGroupPython] H_element094  label="H_element : 0.145"  # scripted group (container) (typed FeaturePython)
  n = 0.05692
FEATURE [App::DocumentObjectGroupPython] C_element102  label="C_element : 0.543"  # scripted group (container) (typed FeaturePython)
  n = 0.542646
FEATURE [App::DocumentObjectGroupPython] Cl_element021  label="Cl_element : 0.400"  # scripted group (container) (typed FeaturePython)
  n = 0.400434
FEATURE [App::DocumentObjectGroupPython] G4_RUBBER_NEOPRENE  # scripted group (container) (typed FeaturePython)
  Dunit = g/cm3
  Dvalue = 1.23
  Group = -> [H_element094,C_element102,Cl_element021]
  conduct = 2
  density = 1
  expand = 3
  formula = G4_RUBBER_NEOPRENE
  name = G4_RUBBER_NEOPRENE
  specific = 4
FEATURE [App::DocumentObjectGroupPython] Si_element006  label="Si_element : 1"  # scripted group (container) (typed FeaturePython)
  n = 1
  ref = Si_element
FEATURE [App::DocumentObjectGroupPython] O_element087  label="O_element : 048"  # scripted group (container) (typed FeaturePython)
  n = 2
  ref = O_element
FEATURE [App::DocumentObjectGroupPython] G4_SILICON_DIOXIDE  # scripted group (container) (typed FeaturePython)
  Dunit = g/cm3
  Dvalue = 2.32
  Group = -> [Si_element006,O_element087]
  conduct = 2
  density = 1
  expand = 3
  formula = G4_SILICON_DIOXIDE
  name = G4_SILICON_DIOXIDE
  specific = 4
FEATURE [App::DocumentObjectGroupPython] Ag_element002  label="Ag_element : 1"  # scripted group (container) (typed FeaturePython)
  n = 1
  ref = Ag_element
FEATURE [App::DocumentObjectGroupPython] Br_element005  label="Br_element : 003"  # scripted group (container) (typed FeaturePython)
  n = 1
  ref = Br_element
FEATURE [App::DocumentObjectGroupPython] G4_SILVER_BROMIDE  # scripted group (container) (typed FeaturePython)
  Dunit = g/cm3
  Dvalue = 6.473
  Group = -> [Ag_element002,Br_element005]
  conduct = 2
  density = 1
  expand = 3
  formula = G4_SILVER_BROMIDE
  name = G4_SILVER_BROMIDE
  specific = 4
FEATURE [App::DocumentObjectGroupPython] Ag_element003  label="Ag_element : 002"  # scripted group (container) (typed FeaturePython)
  n = 1
  ref = Ag_element
FEATURE [App::DocumentObjectGroupPython] Cl_element022  label="Cl_element : 011"  # scripted group (container) (typed FeaturePython)
  n = 1
  ref = Cl_element
FEATURE [App::DocumentObjectGroupPython] G4_SILVER_CHLORIDE  # scripted group (container) (typed FeaturePython)
  Dunit = g/cm3
  Dvalue = 5.56
  Group = -> [Ag_element003,Cl_element022]
  conduct = 2
  density = 1
  expand = 3
  formula = G4_SILVER_CHLORIDE
  name = G4_SILVER_CHLORIDE
  specific = 4
FEATURE [App::DocumentObjectGroupPython] Br_element006  label="Br_element : 0.423"  # scripted group (container) (typed FeaturePython)
  n = 0.422895
FEATURE [App::DocumentObjectGroupPython] Ag_element004  label="Ag_element : 0.574"  # scripted group (container) (typed FeaturePython)
  n = 0.573748
FEATURE [App::DocumentObjectGroupPython] I_element007  label="I_element : 0.649"  # scripted group (container) (typed FeaturePython)
  n = 0.003357
FEATURE [App::DocumentObjectGroupPython] G4_SILVER_HALIDES  # scripted group (container) (typed FeaturePython)
  Dunit = g/cm3
  Dvalue = 6.47
  Group = -> [Br_element006,Ag_element004,I_element007]
  conduct = 2
  density = 1
  expand = 3
  formula = G4_SILVER_HALIDES
  name = G4_SILVER_HALIDES
  specific = 4
FEATURE [App::DocumentObjectGroupPython] Ag_element005  label="Ag_element : 003"  # scripted group (container) (typed FeaturePython)
  n = 1
  ref = Ag_element
FEATURE [App::DocumentObjectGroupPython] I_element008  label="I_element : 004"  # scripted group (container) (typed FeaturePython)
  n = 1
  ref = I_element
FEATURE [App::DocumentObjectGroupPython] G4_SILVER_IODIDE  # scripted group (container) (typed FeaturePython)
  Dunit = g/cm3
  Dvalue = 6.01
  Group = -> [Ag_element005,I_element008]
  conduct = 2
  density = 1
  expand = 3
  formula = G4_SILVER_IODIDE
  name = G4_SILVER_IODIDE
  specific = 4
FEATURE [App::DocumentObjectGroupPython] H_element095  label="H_element : 0.100"  # scripted group (container) (typed FeaturePython)
  n = 0.1
FEATURE [App::DocumentObjectGroupPython] C_element103  label="C_element : 0.204"  # scripted group (container) (typed FeaturePython)
  n = 0.204
FEATURE [App::DocumentObjectGroupPython] N_element039  label="N_element : 0.759"  # scripted group (container) (typed FeaturePython)
  n = 0.042
FEATURE [App::DocumentObjectGroupPython] O_element088  label="O_element : 0.645"  # scripted group (container) (typed FeaturePython)
  n = 0.645
FEATURE [App::DocumentObjectGroupPython] Na_element013  label="Na_element : 0.100"  # scripted group (container) (typed FeaturePython)
  n = 0.002
FEATURE [App::DocumentObjectGroupPython] P_element009  label="P_element : 0.107"  # scripted group (container) (typed FeaturePython)
  n = 0.001
FEATURE [App::DocumentObjectGroupPython] S_element020  label="S_element : 0.021"  # scripted group (container) (typed FeaturePython)
  n = 0.002
FEATURE [App::DocumentObjectGroupPython] Cl_element023  label="Cl_element : 0.590"  # scripted group (container) (typed FeaturePython)
  n = 0.003
FEATURE [App::DocumentObjectGroupPython] K_element010  label="K_element : 0.001"  # scripted group (container) (typed FeaturePython)
  n = 0.001
FEATURE [App::DocumentObjectGroupPython] G4_SKIN_ICRP  # scripted group (container) (typed FeaturePython)
  Dunit = g/cm3
  Dvalue = 1.09
  Group = -> [H_element095,C_element103,N_element039,O_element088,Na_element013,P_element009,S_element020,Cl_element023,K_element010]
  conduct = 2
  density = 1
  expand = 3
  formula = G4_SKIN_ICRP
  name = G4_SKIN_ICRP
  specific = 4
FEATURE [App::DocumentObjectGroupPython] Na_element014  label="Na_element : 2"  # scripted group (container) (typed FeaturePython)
  n = 2
  ref = Na_element
FEATURE [App::DocumentObjectGroupPython] C_element104  label="C_element : 058"  # scripted group (container) (typed FeaturePython)
  n = 1
  ref = C_element
FEATURE [App::DocumentObjectGroupPython] O_element089  label="O_element : 049"  # scripted group (container) (typed FeaturePython)
  n = 3
  ref = O_element
FEATURE [App::DocumentObjectGroupPython] G4_SODIUM_CARBONATE  # scripted group (container) (typed FeaturePython)
  Dunit = g/cm3
  Dvalue = 2.532
  Group = -> [Na_element014,C_element104,O_element089]
  conduct = 2
  density = 1
  expand = 3
  formula = G4_SODIUM_CARBONATE
  name = G4_SODIUM_CARBONATE
  specific = 4
FEATURE [App::DocumentObjectGroupPython] Na_element015  label="Na_element : 1"  # scripted group (container) (typed FeaturePython)
  n = 1
  ref = Na_element
FEATURE [App::DocumentObjectGroupPython] I_element009  label="I_element : 005"  # scripted group (container) (typed FeaturePython)
  n = 1
  ref = I_element
FEATURE [App::DocumentObjectGroupPython] G4_SODIUM_IODIDE  # scripted group (container) (typed FeaturePython)
  Dunit = g/cm3
  Dvalue = 3.667
  Group = -> [Na_element015,I_element009]
  conduct = 2
  density = 1
  expand = 3
  formula = G4_SODIUM_IODIDE
  name = G4_SODIUM_IODIDE
  specific = 4
FEATURE [App::DocumentObjectGroupPython] Na_element016  label="Na_element : 003"  # scripted group (container) (typed FeaturePython)
  n = 2
  ref = Na_element
FEATURE [App::DocumentObjectGroupPython] O_element090  label="O_element : 050"  # scripted group (container) (typed FeaturePython)
  n = 1
  ref = O_element
FEATURE [App::DocumentObjectGroupPython] G4_SODIUM_MONOXIDE  # scripted group (container) (typed FeaturePython)
  Dunit = g/cm3
  Dvalue = 2.27
  Group = -> [Na_element016,O_element090]
  conduct = 2
  density = 1
  expand = 3
  formula = G4_SODIUM_MONOXIDE
  name = G4_SODIUM_MONOXIDE
  specific = 4
FEATURE [App::DocumentObjectGroupPython] Na_element017  label="Na_element : 004"  # scripted group (container) (typed FeaturePython)
  n = 1
  ref = Na_element
FEATURE [App::DocumentObjectGroupPython] N_element040  label="N_element : 018"  # scripted group (container) (typed FeaturePython)
  n = 1
  ref = N_element
FEATURE [App::DocumentObjectGroupPython] O_element091  label="O_element : 051"  # scripted group (container) (typed FeaturePython)
  n = 3
  ref = O_element
FEATURE [App::DocumentObjectGroupPython] G4_SODIUM_NITRATE  # scripted group (container) (typed FeaturePython)
  Dunit = g/cm3
  Dvalue = 2.261
  Group = -> [Na_element017,N_element040,O_element091]
  conduct = 2
  density = 1
  expand = 3
  formula = G4_SODIUM_NITRATE
  name = G4_SODIUM_NITRATE
  specific = 4
FEATURE [App::DocumentObjectGroupPython] C_element105  label="C_element : 059"  # scripted group (container) (typed FeaturePython)
  n = 14
  ref = C_element
FEATURE [App::DocumentObjectGroupPython] H_element096  label="H_element : 053"  # scripted group (container) (typed FeaturePython)
  n = 12
  ref = H_element
FEATURE [App::DocumentObjectGroupPython] G4_STILBENE  # scripted group (container) (typed FeaturePython)
  Dunit = g/cm3
  Dvalue = 0.9707
  Group = -> [C_element105,H_element096]
  conduct = 2
  density = 1
  expand = 3
  formula = G4_STILBENE
  name = G4_STILBENE
  specific = 4
FEATURE [App::DocumentObjectGroupPython] C_element106  label="C_element : 12"  # scripted group (container) (typed FeaturePython)
  n = 12
  ref = C_element
FEATURE [App::DocumentObjectGroupPython] H_element097  label="H_element : 22"  # scripted group (container) (typed FeaturePython)
  n = 22
  ref = H_element
FEATURE [App::DocumentObjectGroupPython] O_element092  label="O_element : 11"  # scripted group (container) (typed FeaturePython)
  n = 11
  ref = O_element
FEATURE [App::DocumentObjectGroupPython] G4_SUCROSE  # scripted group (container) (typed FeaturePython)
  Dunit = g/cm3
  Dvalue = 1.5805
  Group = -> [C_element106,H_element097,O_element092]
  conduct = 2
  density = 1
  expand = 3
  formula = G4_SUCROSE
  name = G4_SUCROSE
  specific = 4
FEATURE [App::DocumentObjectGroupPython] C_element107  label="C_element : 18"  # scripted group (container) (typed FeaturePython)
  n = 18
  ref = C_element
FEATURE [App::DocumentObjectGroupPython] H_element098  label="H_element : 054"  # scripted group (container) (typed FeaturePython)
  n = 14
  ref = H_element
FEATURE [App::DocumentObjectGroupPython] G4_TERPHENYL  # scripted group (container) (typed FeaturePython)
  Dunit = g/cm3
  Dvalue = 1.24
  Group = -> [C_element107,H_element098]
  conduct = 2
  density = 1
  expand = 3
  formula = G4_TERPHENYL
  name = G4_TERPHENYL
  specific = 4
FEATURE [App::DocumentObjectGroupPython] H_element099  label="H_element : 0.146"  # scripted group (container) (typed FeaturePython)
  n = 0.106
FEATURE [App::DocumentObjectGroupPython] C_element108  label="C_element : 0.883"  # scripted group (container) (typed FeaturePython)
  n = 0.099
FEATURE [App::DocumentObjectGroupPython] N_element041  label="N_element : 0.020"  # scripted group (container) (typed FeaturePython)
  n = 0.02
FEATURE [App::DocumentObjectGroupPython] O_element093  label="O_element : 0.766"  # scripted group (container) (typed FeaturePython)
  n = 0.766
FEATURE [App::DocumentObjectGroupPython] Na_element018  label="Na_element : 0.101"  # scripted group (container) (typed FeaturePython)
  n = 0.002
FEATURE [App::DocumentObjectGroupPython] P_element010  label="P_element : 0.108"  # scripted group (container) (typed FeaturePython)
  n = 0.001
FEATURE [App::DocumentObjectGroupPython] S_element021  label="S_element : 0.022"  # scripted group (container) (typed FeaturePython)
  n = 0.002
FEATURE [App::DocumentObjectGroupPython] Cl_element024  label="Cl_element : 0.002"  # scripted group (container) (typed FeaturePython)
  n = 0.002
FEATURE [App::DocumentObjectGroupPython] K_element011  label="K_element : 0.017"  # scripted group (container) (typed FeaturePython)
  n = 0.002
FEATURE [App::DocumentObjectGroupPython] G4_TESTIS_ICRP  # scripted group (container) (typed FeaturePython)
  Dunit = g/cm3
  Dvalue = 1.04
  Group = -> [H_element099,C_element108,N_element041,O_element093,Na_element018,P_element010,S_element021,Cl_element024,K_element011]
  conduct = 2
  density = 1
  expand = 3
  formula = G4_TESTIS_ICRP
  name = G4_TESTIS_ICRP
  specific = 4
FEATURE [App::DocumentObjectGroupPython] C_element109  label="C_element : 060"  # scripted group (container) (typed FeaturePython)
  n = 2
  ref = C_element
FEATURE [App::DocumentObjectGroupPython] Cl_element025  label="Cl_element : 012"  # scripted group (container) (typed FeaturePython)
  n = 4
  ref = Cl_element
FEATURE [App::DocumentObjectGroupPython] G4_TETRACHLOROETHYLENE  # scripted group (container) (typed FeaturePython)
  Dunit = g/cm3
  Dvalue = 1.625
  Group = -> [C_element109,Cl_element025]
  conduct = 2
  density = 1
  expand = 3
  formula = G4_TETRACHLOROETHYLENE
  name = G4_TETRACHLOROETHYLENE
  specific = 4
FEATURE [App::DocumentObjectGroupPython] Tl_element001  label="Tl_element : 1"  # scripted group (container) (typed FeaturePython)
  n = 1
  ref = Tl_element
FEATURE [App::DocumentObjectGroupPython] Cl_element026  label="Cl_element : 013"  # scripted group (container) (typed FeaturePython)
  n = 1
  ref = Cl_element
FEATURE [App::DocumentObjectGroupPython] G4_THALLIUM_CHLORIDE  # scripted group (container) (typed FeaturePython)
  Dunit = g/cm3
  Dvalue = 7.004
  Group = -> [Tl_element001,Cl_element026]
  conduct = 2
  density = 1
  expand = 3
  formula = G4_THALLIUM_CHLORIDE
  name = G4_THALLIUM_CHLORIDE
  specific = 4
FEATURE [App::DocumentObjectGroupPython] H_element100  label="H_element : 0.147"  # scripted group (container) (typed FeaturePython)
  n = 0.105
FEATURE [App::DocumentObjectGroupPython] C_element110  label="C_element : 0.256"  # scripted group (container) (typed FeaturePython)
  n = 0.256
FEATURE [App::DocumentObjectGroupPython] N_element042  label="N_element : 0.760"  # scripted group (container) (typed FeaturePython)
  n = 0.027
FEATURE [App::DocumentObjectGroupPython] O_element094  label="O_element : 0.602"  # scripted group (container) (typed FeaturePython)
  n = 0.602
FEATURE [App::DocumentObjectGroupPython] Na_element019  label="Na_element : 0.102"  # scripted group (container) (typed FeaturePython)
  n = 0.001
FEATURE [App::DocumentObjectGroupPython] P_element011  label="P_element : 0.109"  # scripted group (container) (typed FeaturePython)
  n = 0.002
FEATURE [App::DocumentObjectGroupPython] S_element022  label="S_element : 0.023"  # scripted group (container) (typed FeaturePython)
  n = 0.003
FEATURE [App::DocumentObjectGroupPython] Cl_element027  label="Cl_element : 0.591"  # scripted group (container) (typed FeaturePython)
  n = 0.002
FEATURE [App::DocumentObjectGroupPython] K_element012  label="K_element : 0.018"  # scripted group (container) (typed FeaturePython)
  n = 0.002
FEATURE [App::DocumentObjectGroupPython] G4_TISSUE_SOFT_ICRP  # scripted group (container) (typed FeaturePython)
  Dunit = g/cm3
  Dvalue = 1.03
  Group = -> [H_element100,C_element110,N_element042,O_element094,Na_element019,P_element011,S_element022,Cl_element027,K_element012]
  conduct = 2
  density = 1
  expand = 3
  formula = G4_TISSUE_SOFT_ICRP
  name = G4_TISSUE_SOFT_ICRP
  specific = 4
FEATURE [App::DocumentObjectGroupPython] H_element101  label="H_element : 0.148"  # scripted group (container) (typed FeaturePython)
  n = 0.101
FEATURE [App::DocumentObjectGroupPython] C_element111  label="C_element : 0.111"  # scripted group (container) (typed FeaturePython)
  n = 0.111
FEATURE [App::DocumentObjectGroupPython] N_element043  label="N_element : 0.026"  # scripted group (container) (typed FeaturePython)
  n = 0.026
FEATURE [App::DocumentObjectGroupPython] O_element095  label="O_element : 0.762"  # scripted group (container) (typed FeaturePython)
  n = 0.762
FEATURE [App::DocumentObjectGroupPython] G4_TISSUE_SOFT_ICRU_4  label="G4_TISSUE_SOFT_ICRU-4"  # scripted group (container) (typed FeaturePython)
  Dunit = g/cm3
  Dvalue = 1
  Group = -> [H_element101,C_element111,N_element043,O_element095]
  conduct = 2
  density = 1
  expand = 3
  formula = G4_TISSUE_SOFT_ICRU-4
  name = G4_TISSUE_SOFT_ICRU-4
  specific = 4
FEATURE [App::DocumentObjectGroupPython] H_element102  label="H_element : 0.149"  # scripted group (container) (typed FeaturePython)
  n = 0.101869
FEATURE [App::DocumentObjectGroupPython] C_element112  label="C_element : 0.456"  # scripted group (container) (typed FeaturePython)
  n = 0.456179
FEATURE [App::DocumentObjectGroupPython] N_element044  label="N_element : 0.761"  # scripted group (container) (typed FeaturePython)
  n = 0.035172
FEATURE [App::DocumentObjectGroupPython] O_element096  label="O_element : 0.407"  # scripted group (container) (typed FeaturePython)
  n = 0.40678
FEATURE [App::DocumentObjectGroupPython] G4_TISSUE_METHANE  label="G4_TISSUE-METHANE"  # scripted group (container) (typed FeaturePython)
  Dunit = g/cm3
  Dvalue = 0.00106409
  Group = -> [H_element102,C_element112,N_element044,O_element096]
  conduct = 2
  density = 1
  expand = 3
  formula = G4_TISSUE-METHANE
  name = G4_TISSUE-METHANE
  specific = 4
FEATURE [App::DocumentObjectGroupPython] H_element103  label="H_element : 0.103"  # scripted group (container) (typed FeaturePython)
  n = 0.102672
FEATURE [App::DocumentObjectGroupPython] C_element113  label="C_element : 0.569"  # scripted group (container) (typed FeaturePython)
  n = 0.56894
FEATURE [App::DocumentObjectGroupPython] N_element045  label="N_element : 0.762"  # scripted group (container) (typed FeaturePython)
  n = 0.035022
FEATURE [App::DocumentObjectGroupPython] O_element097  label="O_element : 0.293"  # scripted group (container) (typed FeaturePython)
  n = 0.293366
FEATURE [App::DocumentObjectGroupPython] G4_TISSUE_PROPANE  label="G4_TISSUE-PROPANE"  # scripted group (container) (typed FeaturePython)
  Dunit = g/cm3
  Dvalue = 0.00182628
  Group = -> [H_element103,C_element113,N_element045,O_element097]
  conduct = 2
  density = 1
  expand = 3
  formula = G4_TISSUE-PROPANE
  name = G4_TISSUE-PROPANE
  specific = 4
FEATURE [App::DocumentObjectGroupPython] Ti_element003  label="Ti_element : 1"  # scripted group (container) (typed FeaturePython)
  n = 1
  ref = Ti_element
FEATURE [App::DocumentObjectGroupPython] O_element098  label="O_element : 052"  # scripted group (container) (typed FeaturePython)
  n = 2
  ref = O_element
FEATURE [App::DocumentObjectGroupPython] G4_TITANIUM_DIOXIDE  # scripted group (container) (typed FeaturePython)
  Dunit = g/cm3
  Dvalue = 4.26
  Group = -> [Ti_element003,O_element098]
  conduct = 2
  density = 1
  expand = 3
  formula = G4_TITANIUM_DIOXIDE
  name = G4_TITANIUM_DIOXIDE
  specific = 4
FEATURE [App::DocumentObjectGroupPython] C_element114  label="C_element : 061"  # scripted group (container) (typed FeaturePython)
  n = 7
  ref = C_element
FEATURE [App::DocumentObjectGroupPython] H_element104  label="H_element : 055"  # scripted group (container) (typed FeaturePython)
  n = 8
  ref = H_element
FEATURE [App::DocumentObjectGroupPython] G4_TOLUENE  # scripted group (container) (typed FeaturePython)
  Dunit = g/cm3
  Dvalue = 0.8669
  Group = -> [C_element114,H_element104]
  conduct = 2
  density = 1
  expand = 3
  formula = G4_TOLUENE
  name = G4_TOLUENE
  specific = 4
FEATURE [App::DocumentObjectGroupPython] C_element115  label="C_element : 062"  # scripted group (container) (typed FeaturePython)
  n = 2
  ref = C_element
FEATURE [App::DocumentObjectGroupPython] H_element105  label="H_element : 056"  # scripted group (container) (typed FeaturePython)
  n = 1
  ref = H_element
FEATURE [App::DocumentObjectGroupPython] Cl_element028  label="Cl_element : 014"  # scripted group (container) (typed FeaturePython)
  n = 3
  ref = Cl_element
FEATURE [App::DocumentObjectGroupPython] G4_TRICHLOROETHYLENE  # scripted group (container) (typed FeaturePython)
  Dunit = g/cm3
  Dvalue = 1.46
  Group = -> [C_element115,H_element105,Cl_element028]
  conduct = 2
  density = 1
  expand = 3
  formula = G4_TRICHLOROETHYLENE
  name = G4_TRICHLOROETHYLENE
  specific = 4
FEATURE [App::DocumentObjectGroupPython] C_element116  label="C_element : 063"  # scripted group (container) (typed FeaturePython)
  n = 6
  ref = C_element
FEATURE [App::DocumentObjectGroupPython] H_element106  label="H_element : 15"  # scripted group (container) (typed FeaturePython)
  n = 15
  ref = H_element
FEATURE [App::DocumentObjectGroupPython] O_element099  label="O_element : 053"  # scripted group (container) (typed FeaturePython)
  n = 4
  ref = O_element
FEATURE [App::DocumentObjectGroupPython] P_element012  label="P_element : 1"  # scripted group (container) (typed FeaturePython)
  n = 1
  ref = P_element
FEATURE [App::DocumentObjectGroupPython] G4_TRIETHYL_PHOSPHATE  # scripted group (container) (typed FeaturePython)
  Dunit = g/cm3
  Dvalue = 1.07
  Group = -> [C_element116,H_element106,O_element099,P_element012]
  conduct = 2
  density = 1
  expand = 3
  formula = G4_TRIETHYL_PHOSPHATE
  name = G4_TRIETHYL_PHOSPHATE
  specific = 4
FEATURE [App::DocumentObjectGroupPython] W_element003  label="W_element : 003"  # scripted group (container) (typed FeaturePython)
  n = 1
  ref = W_element
FEATURE [App::DocumentObjectGroupPython] F_element017  label="F_element : 6"  # scripted group (container) (typed FeaturePython)
  n = 6
  ref = F_element
FEATURE [App::DocumentObjectGroupPython] G4_TUNGSTEN_HEXAFLUORIDE  # scripted group (container) (typed FeaturePython)
  Dunit = g/cm3
  Dvalue = 2.4
  Group = -> [W_element003,F_element017]
  conduct = 2
  density = 1
  expand = 3
  formula = G4_TUNGSTEN_HEXAFLUORIDE
  name = G4_TUNGSTEN_HEXAFLUORIDE
  specific = 4
FEATURE [App::DocumentObjectGroupPython] U_element001  label="U_element : 1"  # scripted group (container) (typed FeaturePython)
  n = 1
  ref = U_element
FEATURE [App::DocumentObjectGroupPython] C_element117  label="C_element : 064"  # scripted group (container) (typed FeaturePython)
  n = 2
  ref = C_element
FEATURE [App::DocumentObjectGroupPython] G4_URANIUM_DICARBIDE  # scripted group (container) (typed FeaturePython)
  Dunit = g/cm3
  Dvalue = 11.28
  Group = -> [U_element001,C_element117]
  conduct = 2
  density = 1
  expand = 3
  formula = G4_URANIUM_DICARBIDE
  name = G4_URANIUM_DICARBIDE
  specific = 4
FEATURE [App::DocumentObjectGroupPython] U_element002  label="U_element : 002"  # scripted group (container) (typed FeaturePython)
  n = 1
  ref = U_element
FEATURE [App::DocumentObjectGroupPython] C_element118  label="C_element : 065"  # scripted group (container) (typed FeaturePython)
  n = 1
  ref = C_element
FEATURE [App::DocumentObjectGroupPython] G4_URANIUM_MONOCARBIDE  # scripted group (container) (typed FeaturePython)
  Dunit = g/cm3
  Dvalue = 13.63
  Group = -> [U_element002,C_element118]
  conduct = 2
  density = 1
  expand = 3
  formula = G4_URANIUM_MONOCARBIDE
  name = G4_URANIUM_MONOCARBIDE
  specific = 4
FEATURE [App::DocumentObjectGroupPython] U_element003  label="U_element : 003"  # scripted group (container) (typed FeaturePython)
  n = 1
  ref = U_element
FEATURE [App::DocumentObjectGroupPython] O_element100  label="O_element : 054"  # scripted group (container) (typed FeaturePython)
  n = 2
  ref = O_element
FEATURE [App::DocumentObjectGroupPython] G4_URANIUM_OXIDE  # scripted group (container) (typed FeaturePython)
  Dunit = g/cm3
  Dvalue = 10.96
  Group = -> [U_element003,O_element100]
  conduct = 2
  density = 1
  expand = 3
  formula = G4_URANIUM_OXIDE
  name = G4_URANIUM_OXIDE
  specific = 4
FEATURE [App::DocumentObjectGroupPython] C_element119  label="C_element : 066"  # scripted group (container) (typed FeaturePython)
  n = 1
  ref = C_element
FEATURE [App::DocumentObjectGroupPython] H_element107  label="H_element : 057"  # scripted group (container) (typed FeaturePython)
  n = 4
  ref = H_element
FEATURE [App::DocumentObjectGroupPython] N_element046  label="N_element : 019"  # scripted group (container) (typed FeaturePython)
  n = 2
  ref = N_element
FEATURE [App::DocumentObjectGroupPython] O_element101  label="O_element : 055"  # scripted group (container) (typed FeaturePython)
  n = 1
  ref = O_element
FEATURE [App::DocumentObjectGroupPython] G4_UREA  # scripted group (container) (typed FeaturePython)
  Dunit = g/cm3
  Dvalue = 1.323
  Group = -> [C_element119,H_element107,N_element046,O_element101]
  conduct = 2
  density = 1
  expand = 3
  formula = G4_UREA
  name = G4_UREA
  specific = 4
FEATURE [App::DocumentObjectGroupPython] C_element120  label="C_element : 067"  # scripted group (container) (typed FeaturePython)
  n = 5
  ref = C_element
FEATURE [App::DocumentObjectGroupPython] H_element108  label="H_element : 058"  # scripted group (container) (typed FeaturePython)
  n = 11
  ref = H_element
FEATURE [App::DocumentObjectGroupPython] N_element047  label="N_element : 020"  # scripted group (container) (typed FeaturePython)
  n = 1
  ref = N_element
FEATURE [App::DocumentObjectGroupPython] O_element102  label="O_element : 056"  # scripted group (container) (typed FeaturePython)
  n = 2
  ref = O_element
FEATURE [App::DocumentObjectGroupPython] G4_VALINE  # scripted group (container) (typed FeaturePython)
  Dunit = g/cm3
  Dvalue = 1.23
  Group = -> [C_element120,H_element108,N_element047,O_element102]
  conduct = 2
  density = 1
  expand = 3
  formula = G4_VALINE
  name = G4_VALINE
  specific = 4
FEATURE [App::DocumentObjectGroupPython] H_element109  label="H_element : 0.009"  # scripted group (container) (typed FeaturePython)
  n = 0.009417
FEATURE [App::DocumentObjectGroupPython] C_element121  label="C_element : 0.281"  # scripted group (container) (typed FeaturePython)
  n = 0.280555
FEATURE [App::DocumentObjectGroupPython] F_element018  label="F_element : 0.710"  # scripted group (container) (typed FeaturePython)
  n = 0.710028
FEATURE [App::DocumentObjectGroupPython] G4_VITON  # scripted group (container) (typed FeaturePython)
  Dunit = g/cm3
  Dvalue = 1.8
  Group = -> [H_element109,C_element121,F_element018]
  conduct = 2
  density = 1
  expand = 3
  formula = G4_VITON
  name = G4_VITON
  specific = 4
FEATURE [App::DocumentObjectGroupPython] H_element110  label="H_element : 059"  # scripted group (container) (typed FeaturePython)
  n = 2
  ref = H_element
FEATURE [App::DocumentObjectGroupPython] O_element103  label="O_element : 057"  # scripted group (container) (typed FeaturePython)
  n = 1
  ref = O_element
FEATURE [App::DocumentObjectGroupPython] G4_WATER  # scripted group (container) (typed FeaturePython)
  Dunit = g/cm3
  Dvalue = 1
  Group = -> [H_element110,O_element103]
  conduct = 2
  density = 1
  expand = 3
  formula = G4_WATER
  name = G4_WATER
  specific = 4
FEATURE [App::DocumentObjectGroupPython] H_element111  label="H_element : 060"  # scripted group (container) (typed FeaturePython)
  n = 2
  ref = H_element
FEATURE [App::DocumentObjectGroupPython] O_element104  label="O_element : 058"  # scripted group (container) (typed FeaturePython)
  n = 1
  ref = O_element
FEATURE [App::DocumentObjectGroupPython] G4_WATER_VAPOR  # scripted group (container) (typed FeaturePython)
  Dunit = g/cm3
  Dvalue = 0.000756182
  Group = -> [H_element111,O_element104]
  conduct = 2
  density = 1
  expand = 3
  formula = G4_WATER_VAPOR
  name = G4_WATER_VAPOR
  specific = 4
FEATURE [App::DocumentObjectGroupPython] C_element122  label="C_element : 068"  # scripted group (container) (typed FeaturePython)
  n = 8
  ref = C_element
FEATURE [App::DocumentObjectGroupPython] H_element112  label="H_element : 061"  # scripted group (container) (typed FeaturePython)
  n = 10
  ref = H_element
FEATURE [App::DocumentObjectGroupPython] G4_XYLENE  # scripted group (container) (typed FeaturePython)
  Dunit = g/cm3
  Dvalue = 0.87
  Group = -> [C_element122,H_element112]
  conduct = 2
  density = 1
  expand = 3
  formula = G4_XYLENE
  name = G4_XYLENE
  specific = 4
FEATURE [App::DocumentObjectGroupPython] C_element123  label="C_element : 069"  # scripted group (container) (typed FeaturePython)
  n = 1
  ref = C_element
FEATURE [App::DocumentObjectGroupPython] G4_GRAPHITE  # scripted group (container) (typed FeaturePython)
  Dunit = g/cm3
  Dvalue = 2.21
  Group = -> [C_element123]
  conduct = 2
  density = 1
  expand = 3
  formula = G4_GRAPHITE
  name = G4_GRAPHITE
  specific = 4
FEATURE [App::DocumentObjectGroupPython] NIST  # scripted group (container) (typed FeaturePython)
  Group = -> [G4_A_150_TISSUE,G4_ACETONE,G4_ACETYLENE,G4_ADENINE,G4_ADIPOSE_TISSUE_ICRP,G4_AIR,G4_ALANINE,G4_ALUMINUM_OXIDE,G4_AMBER,G4_AMMONIA,G4_ANILINE,G4_ANTHRACENE,G4_B_100_BONE,G4_BAKELITE,G4_BARIUM_FLUORIDE,G4_BARIUM_SULFATE,G4_BENZENE,G4_BERYLLIUM_OXIDE,G4_BGO,G4_BLOOD_ICRP,G4_BONE_COMPACT_ICRU,G4_BONE_CORTICAL_ICRP,G4_BORON_CARBIDE,G4_BORON_OXIDE,G4_BRAIN_ICRP,G4_BUTANE,G4_N_BUTYL_ALCOHOL,G4_C_552,+152 more]
FEATURE [App::DocumentObjectGroupPython] H_element113  label="H_element : 062"  # scripted group (container) (typed FeaturePython)
  n = 1
  ref = H_element
FEATURE [App::DocumentObjectGroupPython] G4_H  # scripted group (container) (typed FeaturePython)
  Dunit = g/cm3
  Dvalue = 8.3748e-05
  Group = -> [H_element113]
  conduct = 2
  density = 1
  expand = 3
  formula = H
  name = G4_H
  specific = 4
FEATURE [App::DocumentObjectGroupPython] He_element001  label="He_element : 1"  # scripted group (container) (typed FeaturePython)
  n = 1
  ref = He_element
FEATURE [App::DocumentObjectGroupPython] G4_He  # scripted group (container) (typed FeaturePython)
  Dunit = g/cm3
  Dvalue = 0.000166322
  Group = -> [He_element001]
  conduct = 2
  density = 1
  expand = 3
  formula = He
  name = G4_He
  specific = 4
FEATURE [App::DocumentObjectGroupPython] Li_element008  label="Li_element : 008"  # scripted group (container) (typed FeaturePython)
  n = 1
  ref = Li_element
FEATURE [App::DocumentObjectGroupPython] G4_Li  # scripted group (container) (typed FeaturePython)
  Dunit = g/cm3
  Dvalue = 0.534
  Group = -> [Li_element008]
  conduct = 2
  density = 1
  expand = 3
  formula = Li
  name = G4_Li
  specific = 4
FEATURE [App::DocumentObjectGroupPython] Be_element002  label="Be_element : 002"  # scripted group (container) (typed FeaturePython)
  n = 1
  ref = Be_element
FEATURE [App::DocumentObjectGroupPython] G4_Be  # scripted group (container) (typed FeaturePython)
  Dunit = g/cm3
  Dvalue = 1.848
  Group = -> [Be_element002]
  conduct = 2
  density = 1
  expand = 3
  formula = Be
  name = G4_Be
  specific = 4
FEATURE [App::DocumentObjectGroupPython] B_element007  label="B_element : 007"  # scripted group (container) (typed FeaturePython)
  n = 1
  ref = B_element
FEATURE [App::DocumentObjectGroupPython] G4_B  # scripted group (container) (typed FeaturePython)
  Dunit = g/cm3
  Dvalue = 2.37
  Group = -> [B_element007]
  conduct = 2
  density = 1
  expand = 3
  formula = B
  name = G4_B
  specific = 4
FEATURE [App::DocumentObjectGroupPython] C_element124  label="C_element : 070"  # scripted group (container) (typed FeaturePython)
  n = 1
  ref = C_element
FEATURE [App::DocumentObjectGroupPython] G4_C  # scripted group (container) (typed FeaturePython)
  Dunit = g/cm3
  Dvalue = 2
  Group = -> [C_element124]
  conduct = 2
  density = 1
  expand = 3
  formula = C
  name = G4_C
  specific = 4
FEATURE [App::DocumentObjectGroupPython] N_element048  label="N_element : 021"  # scripted group (container) (typed FeaturePython)
  n = 1
  ref = N_element
FEATURE [App::DocumentObjectGroupPython] G4_N  # scripted group (container) (typed FeaturePython)
  Dunit = g/cm3
  Dvalue = 0.0011652
  Group = -> [N_element048]
  conduct = 2
  density = 1
  expand = 3
  formula = N
  name = G4_N
  specific = 4
FEATURE [App::DocumentObjectGroupPython] O_element105  label="O_element : 059"  # scripted group (container) (typed FeaturePython)
  n = 1
  ref = O_element
FEATURE [App::DocumentObjectGroupPython] G4_O  # scripted group (container) (typed FeaturePython)
  Dunit = g/cm3
  Dvalue = 0.00133151
  Group = -> [O_element105]
  conduct = 2
  density = 1
  expand = 3
  formula = O
  name = G4_O
  specific = 4
FEATURE [App::DocumentObjectGroupPython] F_element019  label="F_element : 008"  # scripted group (container) (typed FeaturePython)
  n = 1
  ref = F_element
FEATURE [App::DocumentObjectGroupPython] G4_F  # scripted group (container) (typed FeaturePython)
  Dunit = g/cm3
  Dvalue = 0.00158029
  Group = -> [F_element019]
  conduct = 2
  density = 1
  expand = 3
  formula = F
  name = G4_F
  specific = 4
FEATURE [App::DocumentObjectGroupPython] Ne_element001  label="Ne_element : 1"  # scripted group (container) (typed FeaturePython)
  n = 1
  ref = Ne_element
FEATURE [App::DocumentObjectGroupPython] G4_Ne  # scripted group (container) (typed FeaturePython)
  Dunit = g/cm3
  Dvalue = 0.000838505
  Group = -> [Ne_element001]
  conduct = 2
  density = 1
  expand = 3
  formula = Ne
  name = G4_Ne
  specific = 4
FEATURE [App::DocumentObjectGroupPython] Na_element020  label="Na_element : 005"  # scripted group (container) (typed FeaturePython)
  n = 1
  ref = Na_element
FEATURE [App::DocumentObjectGroupPython] G4_Na  # scripted group (container) (typed FeaturePython)
  Dunit = g/cm3
  Dvalue = 0.971
  Group = -> [Na_element020]
  conduct = 2
  density = 1
  expand = 3
  formula = Na
  name = G4_Na
  specific = 4
FEATURE [App::DocumentObjectGroupPython] Mg_element011  label="Mg_element : 005"  # scripted group (container) (typed FeaturePython)
  n = 1
  ref = Mg_element
FEATURE [App::DocumentObjectGroupPython] G4_Mg  # scripted group (container) (typed FeaturePython)
  Dunit = g/cm3
  Dvalue = 1.74
  Group = -> [Mg_element011]
  conduct = 2
  density = 1
  expand = 3
  formula = Mg
  name = G4_Mg
  specific = 4
FEATURE [App::DocumentObjectGroupPython] Al_element004  label="Al_element : 1"  # scripted group (container) (typed FeaturePython)
  n = 1
  ref = Al_element
FEATURE [App::DocumentObjectGroupPython] G4_Al  # scripted group (container) (typed FeaturePython)
  Dunit = g/cm3
  Dvalue = 2.699
  Group = -> [Al_element004]
  conduct = 2
  density = 1
  expand = 3
  formula = Al
  name = G4_Al
  specific = 4
FEATURE [App::DocumentObjectGroupPython] Si_element007  label="Si_element : 002"  # scripted group (container) (typed FeaturePython)
  n = 1
  ref = Si_element
FEATURE [App::DocumentObjectGroupPython] G4_Si  # scripted group (container) (typed FeaturePython)
  Dunit = g/cm3
  Dvalue = 2.33
  Group = -> [Si_element007]
  conduct = 2
  density = 1
  expand = 3
  formula = Si
  name = G4_Si
  specific = 4
FEATURE [App::DocumentObjectGroupPython] P_element013  label="P_element : 002"  # scripted group (container) (typed FeaturePython)
  n = 1
  ref = P_element
FEATURE [App::DocumentObjectGroupPython] G4_P  # scripted group (container) (typed FeaturePython)
  Dunit = g/cm3
  Dvalue = 2.2
  Group = -> [P_element013]
  conduct = 2
  density = 1
  expand = 3
  formula = P
  name = G4_P
  specific = 4
FEATURE [App::DocumentObjectGroupPython] S_element023  label="S_element : 007"  # scripted group (container) (typed FeaturePython)
  n = 1
  ref = S_element
FEATURE [App::DocumentObjectGroupPython] G4_S  # scripted group (container) (typed FeaturePython)
  Dunit = g/cm3
  Dvalue = 2
  Group = -> [S_element023]
  conduct = 2
  density = 1
  expand = 3
  formula = S
  name = G4_S
  specific = 4
FEATURE [App::DocumentObjectGroupPython] Cl_element029  label="Cl_element : 015"  # scripted group (container) (typed FeaturePython)
  n = 1
  ref = Cl_element
FEATURE [App::DocumentObjectGroupPython] G4_Cl  # scripted group (container) (typed FeaturePython)
  Dunit = g/cm3
  Dvalue = 0.00299473
  Group = -> [Cl_element029]
  conduct = 2
  density = 1
  expand = 3
  formula = Cl
  name = G4_Cl
  specific = 4
FEATURE [App::DocumentObjectGroupPython] Ar_element002  label="Ar_element : 1"  # scripted group (container) (typed FeaturePython)
  n = 1
  ref = Ar_element
FEATURE [App::DocumentObjectGroupPython] G4_Ar  # scripted group (container) (typed FeaturePython)
  Dunit = g/cm3
  Dvalue = 0.00166201
  Group = -> [Ar_element002]
  conduct = 2
  density = 1
  expand = 3
  formula = Ar
  name = G4_Ar
  specific = 4
FEATURE [App::DocumentObjectGroupPython] K_element013  label="K_element : 003"  # scripted group (container) (typed FeaturePython)
  n = 1
  ref = K_element
FEATURE [App::DocumentObjectGroupPython] G4_K  # scripted group (container) (typed FeaturePython)
  Dunit = g/cm3
  Dvalue = 0.862
  Group = -> [K_element013]
  conduct = 2
  density = 1
  expand = 3
  formula = K
  name = G4_K
  specific = 4
FEATURE [App::DocumentObjectGroupPython] Ca_element014  label="Ca_element : 007"  # scripted group (container) (typed FeaturePython)
  n = 1
  ref = Ca_element
FEATURE [App::DocumentObjectGroupPython] G4_Ca  # scripted group (container) (typed FeaturePython)
  Dunit = g/cm3
  Dvalue = 1.55
  Group = -> [Ca_element014]
  conduct = 2
  density = 1
  expand = 3
  formula = Ca
  name = G4_Ca
  specific = 4
FEATURE [App::DocumentObjectGroupPython] Sc_element001  label="Sc_element : 1"  # scripted group (container) (typed FeaturePython)
  n = 1
  ref = Sc_element
FEATURE [App::DocumentObjectGroupPython] G4_Sc  # scripted group (container) (typed FeaturePython)
  Dunit = g/cm3
  Dvalue = 2.989
  Group = -> [Sc_element001]
  conduct = 2
  density = 1
  expand = 3
  formula = Sc
  name = G4_Sc
  specific = 4
FEATURE [App::DocumentObjectGroupPython] Ti_element004  label="Ti_element : 002"  # scripted group (container) (typed FeaturePython)
  n = 1
  ref = Ti_element
FEATURE [App::DocumentObjectGroupPython] G4_Ti  # scripted group (container) (typed FeaturePython)
  Dunit = g/cm3
  Dvalue = 4.54
  Group = -> [Ti_element004]
  conduct = 2
  density = 1
  expand = 3
  formula = Ti
  name = G4_Ti
  specific = 4
FEATURE [App::DocumentObjectGroupPython] V_element001  label="V_element : 1"  # scripted group (container) (typed FeaturePython)
  n = 1
  ref = V_element
FEATURE [App::DocumentObjectGroupPython] G4_V  # scripted group (container) (typed FeaturePython)
  Dunit = g/cm3
  Dvalue = 6.11
  Group = -> [V_element001]
  conduct = 2
  density = 1
  expand = 3
  formula = V
  name = G4_V
  specific = 4
FEATURE [App::DocumentObjectGroupPython] Cr_element001  label="Cr_element : 1"  # scripted group (container) (typed FeaturePython)
  n = 1
  ref = Cr_element
FEATURE [App::DocumentObjectGroupPython] G4_Cr  # scripted group (container) (typed FeaturePython)
  Dunit = g/cm3
  Dvalue = 7.18
  Group = -> [Cr_element001]
  conduct = 2
  density = 1
  expand = 3
  formula = Cr
  name = G4_Cr
  specific = 4
FEATURE [App::DocumentObjectGroupPython] Mn_element001  label="Mn_element : 1"  # scripted group (container) (typed FeaturePython)
  n = 1
  ref = Mn_element
FEATURE [App::DocumentObjectGroupPython] G4_Mn  # scripted group (container) (typed FeaturePython)
  Dunit = g/cm3
  Dvalue = 7.44
  Group = -> [Mn_element001]
  conduct = 2
  density = 1
  expand = 3
  formula = Mn
  name = G4_Mn
  specific = 4
FEATURE [App::DocumentObjectGroupPython] Fe_element007  label="Fe_element : 004"  # scripted group (container) (typed FeaturePython)
  n = 1
  ref = Fe_element
FEATURE [App::DocumentObjectGroupPython] G4_Fe  # scripted group (container) (typed FeaturePython)
  Dunit = g/cm3
  Dvalue = 7.874
  Group = -> [Fe_element007]
  conduct = 2
  density = 1
  expand = 3
  formula = Fe
  name = G4_Fe
  specific = 4
FEATURE [App::DocumentObjectGroupPython] Co_element001  label="Co_element : 1"  # scripted group (container) (typed FeaturePython)
  n = 1
  ref = Co_element
FEATURE [App::DocumentObjectGroupPython] G4_Co  # scripted group (container) (typed FeaturePython)
  Dunit = g/cm3
  Dvalue = 8.9
  Group = -> [Co_element001]
  conduct = 2
  density = 1
  expand = 3
  formula = Co
  name = G4_Co
  specific = 4
FEATURE [App::DocumentObjectGroupPython] Ni_element001  label="Ni_element : 1"  # scripted group (container) (typed FeaturePython)
  n = 1
  ref = Ni_element
FEATURE [App::DocumentObjectGroupPython] G4_Ni  # scripted group (container) (typed FeaturePython)
  Dunit = g/cm3
  Dvalue = 8.902
  Group = -> [Ni_element001]
  conduct = 2
  density = 1
  expand = 3
  formula = Ni
  name = G4_Ni
  specific = 4
FEATURE [App::DocumentObjectGroupPython] Cu_element001  label="Cu_element : 1"  # scripted group (container) (typed FeaturePython)
  n = 1
  ref = Cu_element
FEATURE [App::DocumentObjectGroupPython] G4_Cu  # scripted group (container) (typed FeaturePython)
  Dunit = g/cm3
  Dvalue = 8.96
  Group = -> [Cu_element001]
  conduct = 2
  density = 1
  expand = 3
  formula = Cu
  name = G4_Cu
  specific = 4
FEATURE [App::DocumentObjectGroupPython] Zn_element001  label="Zn_element : 1"  # scripted group (container) (typed FeaturePython)
  n = 1
  ref = Zn_element
FEATURE [App::DocumentObjectGroupPython] G4_Zn  # scripted group (container) (typed FeaturePython)
  Dunit = g/cm3
  Dvalue = 7.133
  Group = -> [Zn_element001]
  conduct = 2
  density = 1
  expand = 3
  formula = Zn
  name = G4_Zn
  specific = 4
FEATURE [App::DocumentObjectGroupPython] Ga_element002  label="Ga_element : 002"  # scripted group (container) (typed FeaturePython)
  n = 1
  ref = Ga_element
FEATURE [App::DocumentObjectGroupPython] G4_Ga  # scripted group (container) (typed FeaturePython)
  Dunit = g/cm3
  Dvalue = 5.904
  Group = -> [Ga_element002]
  conduct = 2
  density = 1
  expand = 3
  formula = Ga
  name = G4_Ga
  specific = 4
FEATURE [App::DocumentObjectGroupPython] Ge_element002  label="Ge_element : 1"  # scripted group (container) (typed FeaturePython)
  n = 1
  ref = Ge_element
FEATURE [App::DocumentObjectGroupPython] G4_Ge  # scripted group (container) (typed FeaturePython)
  Dunit = g/cm3
  Dvalue = 5.323
  Group = -> [Ge_element002]
  conduct = 2
  density = 1
  expand = 3
  formula = Ge
  name = G4_Ge
  specific = 4
FEATURE [App::DocumentObjectGroupPython] As_element003  label="As_element : 002"  # scripted group (container) (typed FeaturePython)
  n = 1
  ref = As_element
FEATURE [App::DocumentObjectGroupPython] G4_As  # scripted group (container) (typed FeaturePython)
  Dunit = g/cm3
  Dvalue = 5.73
  Group = -> [As_element003]
  conduct = 2
  density = 1
  expand = 3
  formula = As
  name = G4_As
  specific = 4
FEATURE [App::DocumentObjectGroupPython] Se_element001  label="Se_element : 1"  # scripted group (container) (typed FeaturePython)
  n = 1
  ref = Se_element
FEATURE [App::DocumentObjectGroupPython] G4_Se  # scripted group (container) (typed FeaturePython)
  Dunit = g/cm3
  Dvalue = 4.5
  Group = -> [Se_element001]
  conduct = 2
  density = 1
  expand = 3
  formula = Se
  name = G4_Se
  specific = 4
FEATURE [App::DocumentObjectGroupPython] Br_element007  label="Br_element : 004"  # scripted group (container) (typed FeaturePython)
  n = 1
  ref = Br_element
FEATURE [App::DocumentObjectGroupPython] G4_Br  # scripted group (container) (typed FeaturePython)
  Dunit = g/cm3
  Dvalue = 0.0070721
  Group = -> [Br_element007]
  conduct = 2
  density = 1
  expand = 3
  formula = Br
  name = G4_Br
  specific = 4
FEATURE [App::DocumentObjectGroupPython] Kr_element001  label="Kr_element : 1"  # scripted group (container) (typed FeaturePython)
  n = 1
  ref = Kr_element
FEATURE [App::DocumentObjectGroupPython] G4_Kr  # scripted group (container) (typed FeaturePython)
  Dunit = g/cm3
  Dvalue = 0.00347832
  Group = -> [Kr_element001]
  conduct = 2
  density = 1
  expand = 3
  formula = Kr
  name = G4_Kr
  specific = 4
FEATURE [App::DocumentObjectGroupPython] Rb_element001  label="Rb_element : 1"  # scripted group (container) (typed FeaturePython)
  n = 1
  ref = Rb_element
FEATURE [App::DocumentObjectGroupPython] G4_Rb  # scripted group (container) (typed FeaturePython)
  Dunit = g/cm3
  Dvalue = 1.532
  Group = -> [Rb_element001]
  conduct = 2
  density = 1
  expand = 3
  formula = Rb
  name = G4_Rb
  specific = 4
FEATURE [App::DocumentObjectGroupPython] Sr_element001  label="Sr_element : 1"  # scripted group (container) (typed FeaturePython)
  n = 1
  ref = Sr_element
FEATURE [App::DocumentObjectGroupPython] G4_Sr  # scripted group (container) (typed FeaturePython)
  Dunit = g/cm3
  Dvalue = 2.54
  Group = -> [Sr_element001]
  conduct = 2
  density = 1
  expand = 3
  formula = Sr
  name = G4_Sr
  specific = 4
FEATURE [App::DocumentObjectGroupPython] Y_element001  label="Y_element : 1"  # scripted group (container) (typed FeaturePython)
  n = 1
  ref = Y_element
FEATURE [App::DocumentObjectGroupPython] G4_Y  # scripted group (container) (typed FeaturePython)
  Dunit = g/cm3
  Dvalue = 4.469
  Group = -> [Y_element001]
  conduct = 2
  density = 1
  expand = 3
  formula = Y
  name = G4_Y
  specific = 4
FEATURE [App::DocumentObjectGroupPython] Zr_element001  label="Zr_element : 1"  # scripted group (container) (typed FeaturePython)
  n = 1
  ref = Zr_element
FEATURE [App::DocumentObjectGroupPython] G4_Zr  # scripted group (container) (typed FeaturePython)
  Dunit = g/cm3
  Dvalue = 6.506
  Group = -> [Zr_element001]
  conduct = 2
  density = 1
  expand = 3
  formula = Zr
  name = G4_Zr
  specific = 4
FEATURE [App::DocumentObjectGroupPython] Nb_element001  label="Nb_element : 1"  # scripted group (container) (typed FeaturePython)
  n = 1
  ref = Nb_element
FEATURE [App::DocumentObjectGroupPython] G4_Nb  # scripted group (container) (typed FeaturePython)
  Dunit = g/cm3
  Dvalue = 8.57
  Group = -> [Nb_element001]
  conduct = 2
  density = 1
  expand = 3
  formula = Nb
  name = G4_Nb
  specific = 4
FEATURE [App::DocumentObjectGroupPython] Mo_element001  label="Mo_element : 1"  # scripted group (container) (typed FeaturePython)
  n = 1
  ref = Mo_element
FEATURE [App::DocumentObjectGroupPython] G4_Mo  # scripted group (container) (typed FeaturePython)
  Dunit = g/cm3
  Dvalue = 10.22
  Group = -> [Mo_element001]
  conduct = 2
  density = 1
  expand = 3
  formula = Mo
  name = G4_Mo
  specific = 4
FEATURE [App::DocumentObjectGroupPython] Tc_element001  label="Tc_element : 1"  # scripted group (container) (typed FeaturePython)
  n = 1
  ref = Tc_element
FEATURE [App::DocumentObjectGroupPython] G4_Tc  # scripted group (container) (typed FeaturePython)
  Dunit = g/cm3
  Dvalue = 11.5
  Group = -> [Tc_element001]
  conduct = 2
  density = 1
  expand = 3
  formula = Tc
  name = G4_Tc
  specific = 4
FEATURE [App::DocumentObjectGroupPython] Ru_element001  label="Ru_element : 1"  # scripted group (container) (typed FeaturePython)
  n = 1
  ref = Ru_element
FEATURE [App::DocumentObjectGroupPython] G4_Ru  # scripted group (container) (typed FeaturePython)
  Dunit = g/cm3
  Dvalue = 12.41
  Group = -> [Ru_element001]
  conduct = 2
  density = 1
  expand = 3
  formula = Ru
  name = G4_Ru
  specific = 4
FEATURE [App::DocumentObjectGroupPython] Rh_element001  label="Rh_element : 1"  # scripted group (container) (typed FeaturePython)
  n = 1
  ref = Rh_element
FEATURE [App::DocumentObjectGroupPython] G4_Rh  # scripted group (container) (typed FeaturePython)
  Dunit = g/cm3
  Dvalue = 12.41
  Group = -> [Rh_element001]
  conduct = 2
  density = 1
  expand = 3
  formula = Rh
  name = G4_Rh
  specific = 4
FEATURE [App::DocumentObjectGroupPython] Pd_element001  label="Pd_element : 1"  # scripted group (container) (typed FeaturePython)
  n = 1
  ref = Pd_element
FEATURE [App::DocumentObjectGroupPython] G4_Pd  # scripted group (container) (typed FeaturePython)
  Dunit = g/cm3
  Dvalue = 12.02
  Group = -> [Pd_element001]
  conduct = 2
  density = 1
  expand = 3
  formula = Pd
  name = G4_Pd
  specific = 4
FEATURE [App::DocumentObjectGroupPython] Ag_element006  label="Ag_element : 004"  # scripted group (container) (typed FeaturePython)
  n = 1
  ref = Ag_element
FEATURE [App::DocumentObjectGroupPython] G4_Ag  # scripted group (container) (typed FeaturePython)
  Dunit = g/cm3
  Dvalue = 10.5
  Group = -> [Ag_element006]
  conduct = 2
  density = 1
  expand = 3
  formula = Ag
  name = G4_Ag
  specific = 4
FEATURE [App::DocumentObjectGroupPython] Cd_element003  label="Cd_element : 003"  # scripted group (container) (typed FeaturePython)
  n = 1
  ref = Cd_element
FEATURE [App::DocumentObjectGroupPython] G4_Cd  # scripted group (container) (typed FeaturePython)
  Dunit = g/cm3
  Dvalue = 8.65
  Group = -> [Cd_element003]
  conduct = 2
  density = 1
  expand = 3
  formula = Cd
  name = G4_Cd
  specific = 4
FEATURE [App::DocumentObjectGroupPython] In_element001  label="In_element : 1"  # scripted group (container) (typed FeaturePython)
  n = 1
  ref = In_element
FEATURE [App::DocumentObjectGroupPython] G4_In  # scripted group (container) (typed FeaturePython)
  Dunit = g/cm3
  Dvalue = 7.31
  Group = -> [In_element001]
  conduct = 2
  density = 1
  expand = 3
  formula = In
  name = G4_In
  specific = 4
FEATURE [App::DocumentObjectGroupPython] Sn_element001  label="Sn_element : 1"  # scripted group (container) (typed FeaturePython)
  n = 1
  ref = Sn_element
FEATURE [App::DocumentObjectGroupPython] G4_Sn  # scripted group (container) (typed FeaturePython)
  Dunit = g/cm3
  Dvalue = 7.31
  Group = -> [Sn_element001]
  conduct = 2
  density = 1
  expand = 3
  formula = Sn
  name = G4_Sn
  specific = 4
FEATURE [App::DocumentObjectGroupPython] Sb_element001  label="Sb_element : 1"  # scripted group (container) (typed FeaturePython)
  n = 1
  ref = Sb_element
FEATURE [App::DocumentObjectGroupPython] G4_Sb  # scripted group (container) (typed FeaturePython)
  Dunit = g/cm3
  Dvalue = 6.691
  Group = -> [Sb_element001]
  conduct = 2
  density = 1
  expand = 3
  formula = Sb
  name = G4_Sb
  specific = 4
FEATURE [App::DocumentObjectGroupPython] Te_element002  label="Te_element : 002"  # scripted group (container) (typed FeaturePython)
  n = 1
  ref = Te_element
FEATURE [App::DocumentObjectGroupPython] G4_Te  # scripted group (container) (typed FeaturePython)
  Dunit = g/cm3
  Dvalue = 6.24
  Group = -> [Te_element002]
  conduct = 2
  density = 1
  expand = 3
  formula = Te
  name = G4_Te
  specific = 4
FEATURE [App::DocumentObjectGroupPython] I_element010  label="I_element : 006"  # scripted group (container) (typed FeaturePython)
  n = 1
  ref = I_element
FEATURE [App::DocumentObjectGroupPython] G4_I  # scripted group (container) (typed FeaturePython)
  Dunit = g/cm3
  Dvalue = 4.93
  Group = -> [I_element010]
  conduct = 2
  density = 1
  expand = 3
  formula = I
  name = G4_I
  specific = 4
FEATURE [App::DocumentObjectGroupPython] Xe_element001  label="Xe_element : 1"  # scripted group (container) (typed FeaturePython)
  n = 1
  ref = Xe_element
FEATURE [App::DocumentObjectGroupPython] G4_Xe  # scripted group (container) (typed FeaturePython)
  Dunit = g/cm3
  Dvalue = 0.00548536
  Group = -> [Xe_element001]
  conduct = 2
  density = 1
  expand = 3
  formula = Xe
  name = G4_Xe
  specific = 4
FEATURE [App::DocumentObjectGroupPython] Cs_element003  label="Cs_element : 003"  # scripted group (container) (typed FeaturePython)
  n = 1
  ref = Cs_element
FEATURE [App::DocumentObjectGroupPython] G4_Cs  # scripted group (container) (typed FeaturePython)
  Dunit = g/cm3
  Dvalue = 1.873
  Group = -> [Cs_element003]
  conduct = 2
  density = 1
  expand = 3
  formula = Cs
  name = G4_Cs
  specific = 4
FEATURE [App::DocumentObjectGroupPython] Ba_element003  label="Ba_element : 003"  # scripted group (container) (typed FeaturePython)
  n = 1
  ref = Ba_element
FEATURE [App::DocumentObjectGroupPython] G4_Ba  # scripted group (container) (typed FeaturePython)
  Dunit = g/cm3
  Dvalue = 3.5
  Group = -> [Ba_element003]
  conduct = 2
  density = 1
  expand = 3
  formula = Ba
  name = G4_Ba
  specific = 4
FEATURE [App::DocumentObjectGroupPython] La_element003  label="La_element : 003"  # scripted group (container) (typed FeaturePython)
  n = 1
  ref = La_element
FEATURE [App::DocumentObjectGroupPython] G4_La  # scripted group (container) (typed FeaturePython)
  Dunit = g/cm3
  Dvalue = 6.154
  Group = -> [La_element003]
  conduct = 2
  density = 1
  expand = 3
  formula = La
  name = G4_La
  specific = 4
FEATURE [App::DocumentObjectGroupPython] Ce_element002  label="Ce_element : 1"  # scripted group (container) (typed FeaturePython)
  n = 1
  ref = Ce_element
FEATURE [App::DocumentObjectGroupPython] G4_Ce  # scripted group (container) (typed FeaturePython)
  Dunit = g/cm3
  Dvalue = 6.657
  Group = -> [Ce_element002]
  conduct = 2
  density = 1
  expand = 3
  formula = Ce
  name = G4_Ce
  specific = 4
FEATURE [App::DocumentObjectGroupPython] Pr_element001  label="Pr_element : 1"  # scripted group (container) (typed FeaturePython)
  n = 1
  ref = Pr_element
FEATURE [App::DocumentObjectGroupPython] G4_Pr  # scripted group (container) (typed FeaturePython)
  Dunit = g/cm3
  Dvalue = 6.71
  Group = -> [Pr_element001]
  conduct = 2
  density = 1
  expand = 3
  formula = Pr
  name = G4_Pr
  specific = 4
FEATURE [App::DocumentObjectGroupPython] Nd_element001  label="Nd_element : 1"  # scripted group (container) (typed FeaturePython)
  n = 1
  ref = Nd_element
FEATURE [App::DocumentObjectGroupPython] G4_Nd  # scripted group (container) (typed FeaturePython)
  Dunit = g/cm3
  Dvalue = 6.9
  Group = -> [Nd_element001]
  conduct = 2
  density = 1
  expand = 3
  formula = Nd
  name = G4_Nd
  specific = 4
FEATURE [App::DocumentObjectGroupPython] Pm_element001  label="Pm_element : 1"  # scripted group (container) (typed FeaturePython)
  n = 1
  ref = Pm_element
FEATURE [App::DocumentObjectGroupPython] G4_Pm  # scripted group (container) (typed FeaturePython)
  Dunit = g/cm3
  Dvalue = 7.22
  Group = -> [Pm_element001]
  conduct = 2
  density = 1
  expand = 3
  formula = Pm
  name = G4_Pm
  specific = 4
FEATURE [App::DocumentObjectGroupPython] Sm_element001  label="Sm_element : 1"  # scripted group (container) (typed FeaturePython)
  n = 1
  ref = Sm_element
FEATURE [App::DocumentObjectGroupPython] G4_Sm  # scripted group (container) (typed FeaturePython)
  Dunit = g/cm3
  Dvalue = 7.46
  Group = -> [Sm_element001]
  conduct = 2
  density = 1
  expand = 3
  formula = Sm
  name = G4_Sm
  specific = 4
FEATURE [App::DocumentObjectGroupPython] Eu_element001  label="Eu_element : 1"  # scripted group (container) (typed FeaturePython)
  n = 1
  ref = Eu_element
FEATURE [App::DocumentObjectGroupPython] G4_Eu  # scripted group (container) (typed FeaturePython)
  Dunit = g/cm3
  Dvalue = 5.243
  Group = -> [Eu_element001]
  conduct = 2
  density = 1
  expand = 3
  formula = Eu
  name = G4_Eu
  specific = 4
FEATURE [App::DocumentObjectGroupPython] Gd_element002  label="Gd_element : 1"  # scripted group (container) (typed FeaturePython)
  n = 1
  ref = Gd_element
FEATURE [App::DocumentObjectGroupPython] G4_Gd  # scripted group (container) (typed FeaturePython)
  Dunit = g/cm3
  Dvalue = 7.9004
  Group = -> [Gd_element002]
  conduct = 2
  density = 1
  expand = 3
  formula = Gd
  name = G4_Gd
  specific = 4
FEATURE [App::DocumentObjectGroupPython] Tb_element001  label="Tb_element : 1"  # scripted group (container) (typed FeaturePython)
  n = 1
  ref = Tb_element
FEATURE [App::DocumentObjectGroupPython] G4_Tb  # scripted group (container) (typed FeaturePython)
  Dunit = g/cm3
  Dvalue = 8.229
  Group = -> [Tb_element001]
  conduct = 2
  density = 1
  expand = 3
  formula = Tb
  name = G4_Tb
  specific = 4
FEATURE [App::DocumentObjectGroupPython] Dy_element001  label="Dy_element : 1"  # scripted group (container) (typed FeaturePython)
  n = 1
  ref = Dy_element
FEATURE [App::DocumentObjectGroupPython] G4_Dy  # scripted group (container) (typed FeaturePython)
  Dunit = g/cm3
  Dvalue = 8.55
  Group = -> [Dy_element001]
  conduct = 2
  density = 1
  expand = 3
  formula = Dy
  name = G4_Dy
  specific = 4
FEATURE [App::DocumentObjectGroupPython] Ho_element001  label="Ho_element : 1"  # scripted group (container) (typed FeaturePython)
  n = 1
  ref = Ho_element
FEATURE [App::DocumentObjectGroupPython] G4_Ho  # scripted group (container) (typed FeaturePython)
  Dunit = g/cm3
  Dvalue = 8.795
  Group = -> [Ho_element001]
  conduct = 2
  density = 1
  expand = 3
  formula = Ho
  name = G4_Ho
  specific = 4
FEATURE [App::DocumentObjectGroupPython] Er_element001  label="Er_element : 1"  # scripted group (container) (typed FeaturePython)
  n = 1
  ref = Er_element
FEATURE [App::DocumentObjectGroupPython] G4_Er  # scripted group (container) (typed FeaturePython)
  Dunit = g/cm3
  Dvalue = 9.066
  Group = -> [Er_element001]
  conduct = 2
  density = 1
  expand = 3
  formula = Er
  name = G4_Er
  specific = 4
FEATURE [App::DocumentObjectGroupPython] Tm_element001  label="Tm_element : 1"  # scripted group (container) (typed FeaturePython)
  n = 1
  ref = Tm_element
FEATURE [App::DocumentObjectGroupPython] G4_Tm  # scripted group (container) (typed FeaturePython)
  Dunit = g/cm3
  Dvalue = 9.321
  Group = -> [Tm_element001]
  conduct = 2
  density = 1
  expand = 3
  formula = Tm
  name = G4_Tm
  specific = 4
FEATURE [App::DocumentObjectGroupPython] Yb_element001  label="Yb_element : 1"  # scripted group (container) (typed FeaturePython)
  n = 1
  ref = Yb_element
FEATURE [App::DocumentObjectGroupPython] G4_Yb  # scripted group (container) (typed FeaturePython)
  Dunit = g/cm3
  Dvalue = 6.73
  Group = -> [Yb_element001]
  conduct = 2
  density = 1
  expand = 3
  formula = Yb
  name = G4_Yb
  specific = 4
FEATURE [App::DocumentObjectGroupPython] Lu_element001  label="Lu_element : 1"  # scripted group (container) (typed FeaturePython)
  n = 1
  ref = Lu_element
FEATURE [App::DocumentObjectGroupPython] G4_Lu  # scripted group (container) (typed FeaturePython)
  Dunit = g/cm3
  Dvalue = 9.84
  Group = -> [Lu_element001]
  conduct = 2
  density = 1
  expand = 3
  formula = Lu
  name = G4_Lu
  specific = 4
FEATURE [App::DocumentObjectGroupPython] Hf_element001  label="Hf_element : 1"  # scripted group (container) (typed FeaturePython)
  n = 1
  ref = Hf_element
FEATURE [App::DocumentObjectGroupPython] G4_Hf  # scripted group (container) (typed FeaturePython)
  Dunit = g/cm3
  Dvalue = 13.31
  Group = -> [Hf_element001]
  conduct = 2
  density = 1
  expand = 3
  formula = Hf
  name = G4_Hf
  specific = 4
FEATURE [App::DocumentObjectGroupPython] Ta_element001  label="Ta_element : 1"  # scripted group (container) (typed FeaturePython)
  n = 1
  ref = Ta_element
FEATURE [App::DocumentObjectGroupPython] G4_Ta  # scripted group (container) (typed FeaturePython)
  Dunit = g/cm3
  Dvalue = 16.654
  Group = -> [Ta_element001]
  conduct = 2
  density = 1
  expand = 3
  formula = Ta
  name = G4_Ta
  specific = 4
FEATURE [App::DocumentObjectGroupPython] W_element004  label="W_element : 004"  # scripted group (container) (typed FeaturePython)
  n = 1
  ref = W_element
FEATURE [App::DocumentObjectGroupPython] G4_W  # scripted group (container) (typed FeaturePython)
  Dunit = g/cm3
  Dvalue = 19.3
  Group = -> [W_element004]
  conduct = 2
  density = 1
  expand = 3
  formula = W
  name = G4_W
  specific = 4
FEATURE [App::DocumentObjectGroupPython] Re_element001  label="Re_element : 1"  # scripted group (container) (typed FeaturePython)
  n = 1
  ref = Re_element
FEATURE [App::DocumentObjectGroupPython] G4_Re  # scripted group (container) (typed FeaturePython)
  Dunit = g/cm3
  Dvalue = 21.02
  Group = -> [Re_element001]
  conduct = 2
  density = 1
  expand = 3
  formula = Re
  name = G4_Re
  specific = 4
FEATURE [App::DocumentObjectGroupPython] Os_element001  label="Os_element : 1"  # scripted group (container) (typed FeaturePython)
  n = 1
  ref = Os_element
FEATURE [App::DocumentObjectGroupPython] G4_Os  # scripted group (container) (typed FeaturePython)
  Dunit = g/cm3
  Dvalue = 22.57
  Group = -> [Os_element001]
  conduct = 2
  density = 1
  expand = 3
  formula = Os
  name = G4_Os
  specific = 4
FEATURE [App::DocumentObjectGroupPython] Ir_element001  label="Ir_element : 1"  # scripted group (container) (typed FeaturePython)
  n = 1
  ref = Ir_element
FEATURE [App::DocumentObjectGroupPython] G4_Ir  # scripted group (container) (typed FeaturePython)
  Dunit = g/cm3
  Dvalue = 22.42
  Group = -> [Ir_element001]
  conduct = 2
  density = 1
  expand = 3
  formula = Ir
  name = G4_Ir
  specific = 4
FEATURE [App::DocumentObjectGroupPython] Pt_element001  label="Pt_element : 1"  # scripted group (container) (typed FeaturePython)
  n = 1
  ref = Pt_element
FEATURE [App::DocumentObjectGroupPython] G4_Pt  # scripted group (container) (typed FeaturePython)
  Dunit = g/cm3
  Dvalue = 21.45
  Group = -> [Pt_element001]
  conduct = 2
  density = 1
  expand = 3
  formula = Pt
  name = G4_Pt
  specific = 4
FEATURE [App::DocumentObjectGroupPython] Au_element001  label="Au_element : 1"  # scripted group (container) (typed FeaturePython)
  n = 1
  ref = Au_element
FEATURE [App::DocumentObjectGroupPython] G4_Au  # scripted group (container) (typed FeaturePython)
  Dunit = g/cm3
  Dvalue = 19.32
  Group = -> [Au_element001]
  conduct = 2
  density = 1
  expand = 3
  formula = Au
  name = G4_Au
  specific = 4
FEATURE [App::DocumentObjectGroupPython] Hg_element002  label="Hg_element : 002"  # scripted group (container) (typed FeaturePython)
  n = 1
  ref = Hg_element
FEATURE [App::DocumentObjectGroupPython] G4_Hg  # scripted group (container) (typed FeaturePython)
  Dunit = g/cm3
  Dvalue = 13.546
  Group = -> [Hg_element002]
  conduct = 2
  density = 1
  expand = 3
  formula = Hg
  name = G4_Hg
  specific = 4
FEATURE [App::DocumentObjectGroupPython] Tl_element002  label="Tl_element : 002"  # scripted group (container) (typed FeaturePython)
  n = 1
  ref = Tl_element
FEATURE [App::DocumentObjectGroupPython] G4_Tl  # scripted group (container) (typed FeaturePython)
  Dunit = g/cm3
  Dvalue = 11.72
  Group = -> [Tl_element002]
  conduct = 2
  density = 1
  expand = 3
  formula = Tl
  name = G4_Tl
  specific = 4
FEATURE [App::DocumentObjectGroupPython] Pb_element003  label="Pb_element : 1"  # scripted group (container) (typed FeaturePython)
  n = 1
  ref = Pb_element
FEATURE [App::DocumentObjectGroupPython] G4_Pb  # scripted group (container) (typed FeaturePython)
  Dunit = g/cm3
  Dvalue = 11.35
  Group = -> [Pb_element003]
  conduct = 2
  density = 1
  expand = 3
  formula = Pb
  name = G4_Pb
  specific = 4
FEATURE [App::DocumentObjectGroupPython] Bi_element002  label="Bi_element : 1"  # scripted group (container) (typed FeaturePython)
  n = 1
  ref = Bi_element
FEATURE [App::DocumentObjectGroupPython] G4_Bi  # scripted group (container) (typed FeaturePython)
  Dunit = g/cm3
  Dvalue = 9.747
  Group = -> [Bi_element002]
  conduct = 2
  density = 1
  expand = 3
  formula = Bi
  name = G4_Bi
  specific = 4
FEATURE [App::DocumentObjectGroupPython] Po_element001  label="Po_element : 1"  # scripted group (container) (typed FeaturePython)
  n = 1
  ref = Po_element
FEATURE [App::DocumentObjectGroupPython] G4_Po  # scripted group (container) (typed FeaturePython)
  Dunit = g/cm3
  Dvalue = 9.32
  Group = -> [Po_element001]
  conduct = 2
  density = 1
  expand = 3
  formula = Po
  name = G4_Po
  specific = 4
FEATURE [App::DocumentObjectGroupPython] At_element001  label="At_element : 1"  # scripted group (container) (typed FeaturePython)
  n = 1
  ref = At_element
FEATURE [App::DocumentObjectGroupPython] G4_At  # scripted group (container) (typed FeaturePython)
  Dunit = g/cm3
  Dvalue = 9.32
  Group = -> [At_element001]
  conduct = 2
  density = 1
  expand = 3
  formula = At
  name = G4_At
  specific = 4
FEATURE [App::DocumentObjectGroupPython] Rn_element001  label="Rn_element : 1"  # scripted group (container) (typed FeaturePython)
  n = 1
  ref = Rn_element
FEATURE [App::DocumentObjectGroupPython] G4_Rn  # scripted group (container) (typed FeaturePython)
  Dunit = g/cm3
  Dvalue = 0.00900662
  Group = -> [Rn_element001]
  conduct = 2
  density = 1
  expand = 3
  formula = Rn
  name = G4_Rn
  specific = 4
FEATURE [App::DocumentObjectGroupPython] Fr_element001  label="Fr_element : 1"  # scripted group (container) (typed FeaturePython)
  n = 1
  ref = Fr_element
FEATURE [App::DocumentObjectGroupPython] G4_Fr  # scripted group (container) (typed FeaturePython)
  Dunit = g/cm3
  Dvalue = 1
  Group = -> [Fr_element001]
  conduct = 2
  density = 1
  expand = 3
  formula = Fr
  name = G4_Fr
  specific = 4
FEATURE [App::DocumentObjectGroupPython] Ra_element001  label="Ra_element : 1"  # scripted group (container) (typed FeaturePython)
  n = 1
  ref = Ra_element
FEATURE [App::DocumentObjectGroupPython] G4_Ra  # scripted group (container) (typed FeaturePython)
  Dunit = g/cm3
  Dvalue = 5
  Group = -> [Ra_element001]
  conduct = 2
  density = 1
  expand = 3
  formula = Ra
  name = G4_Ra
  specific = 4
FEATURE [App::DocumentObjectGroupPython] Ac_element001  label="Ac_element : 1"  # scripted group (container) (typed FeaturePython)
  n = 1
  ref = Ac_element
FEATURE [App::DocumentObjectGroupPython] G4_Ac  # scripted group (container) (typed FeaturePython)
  Dunit = g/cm3
  Dvalue = 10.07
  Group = -> [Ac_element001]
  conduct = 2
  density = 1
  expand = 3
  formula = Ac
  name = G4_Ac
  specific = 4
FEATURE [App::DocumentObjectGroupPython] Th_element001  label="Th_element : 1"  # scripted group (container) (typed FeaturePython)
  n = 1
  ref = Th_element
FEATURE [App::DocumentObjectGroupPython] G4_Th  # scripted group (container) (typed FeaturePython)
  Dunit = g/cm3
  Dvalue = 11.72
  Group = -> [Th_element001]
  conduct = 2
  density = 1
  expand = 3
  formula = Th
  name = G4_Th
  specific = 4
FEATURE [App::DocumentObjectGroupPython] Pa_element001  label="Pa_element : 1"  # scripted group (container) (typed FeaturePython)
  n = 1
  ref = Pa_element
FEATURE [App::DocumentObjectGroupPython] G4_Pa  # scripted group (container) (typed FeaturePython)
  Dunit = g/cm3
  Dvalue = 15.37
  Group = -> [Pa_element001]
  conduct = 2
  density = 1
  expand = 3
  formula = Pa
  name = G4_Pa
  specific = 4
FEATURE [App::DocumentObjectGroupPython] U_element004  label="U_element : 004"  # scripted group (container) (typed FeaturePython)
  n = 1
  ref = U_element
FEATURE [App::DocumentObjectGroupPython] G4_U  # scripted group (container) (typed FeaturePython)
  Dunit = g/cm3
  Dvalue = 18.95
  Group = -> [U_element004]
  conduct = 2
  density = 1
  expand = 3
  formula = U
  name = G4_U
  specific = 4
FEATURE [App::DocumentObjectGroupPython] Np_element001  label="Np_element : 1"  # scripted group (container) (typed FeaturePython)
  n = 1
  ref = Np_element
FEATURE [App::DocumentObjectGroupPython] G4_Np  # scripted group (container) (typed FeaturePython)
  Dunit = g/cm3
  Dvalue = 20.25
  Group = -> [Np_element001]
  conduct = 2
  density = 1
  expand = 3
  formula = Np
  name = G4_Np
  specific = 4
FEATURE [App::DocumentObjectGroupPython] Pu_element002  label="Pu_element : 002"  # scripted group (container) (typed FeaturePython)
  n = 1
  ref = Pu_element
FEATURE [App::DocumentObjectGroupPython] G4_Pu  # scripted group (container) (typed FeaturePython)
  Dunit = g/cm3
  Dvalue = 19.84
  Group = -> [Pu_element002]
  conduct = 2
  density = 1
  expand = 3
  formula = Pu
  name = G4_Pu
  specific = 4
FEATURE [App::DocumentObjectGroupPython] Am_element001  label="Am_element : 1"  # scripted group (container) (typed FeaturePython)
  n = 1
  ref = Am_element
FEATURE [App::DocumentObjectGroupPython] G4_Am  # scripted group (container) (typed FeaturePython)
  Dunit = g/cm3
  Dvalue = 13.67
  Group = -> [Am_element001]
  conduct = 2
  density = 1
  expand = 3
  formula = Am
  name = G4_Am
  specific = 4
FEATURE [App::DocumentObjectGroupPython] Cm_element001  label="Cm_element : 1"  # scripted group (container) (typed FeaturePython)
  n = 1
  ref = Cm_element
FEATURE [App::DocumentObjectGroupPython] G4_Cm  # scripted group (container) (typed FeaturePython)
  Dunit = g/cm3
  Dvalue = 13.51
  Group = -> [Cm_element001]
  conduct = 2
  density = 1
  expand = 3
  formula = Cm
  name = G4_Cm
  specific = 4
FEATURE [App::DocumentObjectGroupPython] Bk_element001  label="Bk_element : 1"  # scripted group (container) (typed FeaturePython)
  n = 1
  ref = Bk_element
FEATURE [App::DocumentObjectGroupPython] G4_Bk  # scripted group (container) (typed FeaturePython)
  Dunit = g/cm3
  Dvalue = 14
  Group = -> [Bk_element001]
  conduct = 2
  density = 1
  expand = 3
  formula = Bk
  name = G4_Bk
  specific = 4
FEATURE [App::DocumentObjectGroupPython] Cf_element001  label="Cf_element : 1"  # scripted group (container) (typed FeaturePython)
  n = 1
  ref = Cf_element
FEATURE [App::DocumentObjectGroupPython] G4_Cf  # scripted group (container) (typed FeaturePython)
  Dunit = g/cm3
  Dvalue = 10
  Group = -> [Cf_element001]
  conduct = 2
  density = 1
  expand = 3
  formula = Cf
  name = G4_Cf
  specific = 4
FEATURE [App::DocumentObjectGroupPython] Element  # scripted group (container) (typed FeaturePython)
  Group = -> [G4_H,G4_He,G4_Li,G4_Be,G4_B,G4_C,G4_N,G4_O,G4_F,G4_Ne,G4_Na,G4_Mg,G4_Al,G4_Si,G4_P,G4_S,G4_Cl,G4_Ar,G4_K,G4_Ca,G4_Sc,G4_Ti,G4_V,G4_Cr,G4_Mn,G4_Fe,G4_Co,G4_Ni,G4_Cu,G4_Zn,G4_Ga,G4_Ge,G4_As,G4_Se,G4_Br,G4_Kr,G4_Rb,G4_Sr,G4_Y,G4_Zr,G4_Nb,G4_Mo,G4_Tc,G4_Ru,G4_Rh,G4_Pd,G4_Ag,G4_Cd,G4_In,G4_Sn,G4_Sb,G4_Te,G4_I,G4_Xe,G4_Cs,G4_Ba,G4_La,G4_Ce,G4_Pr,G4_Nd,G4_Pm,G4_Sm,G4_Eu,G4_Gd,G4_Tb,G4_Dy,G4_Ho,G4_Er,+30 more]
FEATURE [App::DocumentObjectGroupPython] H_element114  label="H_element : 063"  # scripted group (container) (typed FeaturePython)
  n = 2
  ref = H_element
FEATURE [App::DocumentObjectGroupPython] G4_lH2  # scripted group (container) (typed FeaturePython)
  Dunit = g/cm3
  Dvalue = 0.0708
  Group = -> [H_element114]
  conduct = 2
  density = 1
  expand = 3
  formula = G4_lH2
  name = G4_lH2
  specific = 4
FEATURE [App::DocumentObjectGroupPython] N_element049  label="N_element : 022"  # scripted group (container) (typed FeaturePython)
  n = 2
  ref = N_element
FEATURE [App::DocumentObjectGroupPython] G4_lN2  # scripted group (container) (typed FeaturePython)
  Dunit = g/cm3
  Dvalue = 0.807
  Group = -> [N_element049]
  conduct = 2
  density = 1
  expand = 3
  formula = G4_lN2
  name = G4_lN2
  specific = 4
FEATURE [App::DocumentObjectGroupPython] O_element106  label="O_element : 060"  # scripted group (container) (typed FeaturePython)
  n = 2
  ref = O_element
FEATURE [App::DocumentObjectGroupPython] G4_lO2  # scripted group (container) (typed FeaturePython)
  Dunit = g/cm3
  Dvalue = 1.141
  Group = -> [O_element106]
  conduct = 2
  density = 1
  expand = 3
  formula = G4_lO2
  name = G4_lO2
  specific = 4
FEATURE [App::DocumentObjectGroupPython] Ar  label="Ar : 1"  # scripted group (container) (typed FeaturePython)
  n = 1
  ref = Ar
FEATURE [App::DocumentObjectGroupPython] G4_lAr  # scripted group (container) (typed FeaturePython)
  Dunit = g/cm3
  Dvalue = 1.396
  Group = -> [Ar]
  conduct = 2
  density = 1
  expand = 3
  formula = G4_lAr
  name = G4_lAr
  specific = 4
FEATURE [App::DocumentObjectGroupPython] Br  label="Br : 1"  # scripted group (container) (typed FeaturePython)
  n = 1
  ref = Br
FEATURE [App::DocumentObjectGroupPython] G4_lBr  # scripted group (container) (typed FeaturePython)
  Dunit = g/cm3
  Dvalue = 3.1028
  Group = -> [Br]
  conduct = 2
  density = 1
  expand = 3
  formula = G4_lBr
  name = G4_lBr
  specific = 4
FEATURE [App::DocumentObjectGroupPython] Kr  label="Kr : 1"  # scripted group (container) (typed FeaturePython)
  n = 1
  ref = Kr
FEATURE [App::DocumentObjectGroupPython] G4_lKr  # scripted group (container) (typed FeaturePython)
  Dunit = g/cm3
  Dvalue = 2.418
  Group = -> [Kr]
  conduct = 2
  density = 1
  expand = 3
  formula = G4_lKr
  name = G4_lKr
  specific = 4
FEATURE [App::DocumentObjectGroupPython] Xe  label="Xe : 1"  # scripted group (container) (typed FeaturePython)
  n = 1
  ref = Xe
FEATURE [App::DocumentObjectGroupPython] G4_lXe  # scripted group (container) (typed FeaturePython)
  Dunit = g/cm3
  Dvalue = 2.953
  Group = -> [Xe]
  conduct = 2
  density = 1
  expand = 3
  formula = G4_lXe
  name = G4_lXe
  specific = 4
FEATURE [App::DocumentObjectGroupPython] O_element107  label="O_element : 061"  # scripted group (container) (typed FeaturePython)
  n = 4
  ref = O_element
FEATURE [App::DocumentObjectGroupPython] Pb_element004  label="Pb_element : 002"  # scripted group (container) (typed FeaturePython)
  n = 1
  ref = Pb_element
FEATURE [App::DocumentObjectGroupPython] W_element005  label="W_element : 005"  # scripted group (container) (typed FeaturePython)
  n = 1
  ref = W_element
FEATURE [App::DocumentObjectGroupPython] G4_PbWO4  # scripted group (container) (typed FeaturePython)
  Dunit = g/cm3
  Dvalue = 8.28
  Group = -> [O_element107,Pb_element004,W_element005]
  conduct = 2
  density = 1
  expand = 3
  formula = G4_PbWO4
  name = G4_PbWO4
  specific = 4
FEATURE [App::DocumentObjectGroupPython] alactic  label="alactic : 1"  # scripted group (container) (typed FeaturePython)
  n = 1
  ref = alactic
FEATURE [App::DocumentObjectGroupPython] G4_Galactic  # scripted group (container) (typed FeaturePython)
  Dunit = g/cm3
  Dvalue = 0
  Group = -> [alactic]
  conduct = 2
  density = 1
  expand = 3
  formula = G4_Galactic
  name = G4_Galactic
  specific = 4
FEATURE [App::DocumentObjectGroupPython] RAPHITE_POROUS  label="RAPHITE_POROUS : 1"  # scripted group (container) (typed FeaturePython)
  n = 1
  ref = RAPHITE_POROUS
FEATURE [App::DocumentObjectGroupPython] G4_GRAPHITE_POROUS  # scripted group (container) (typed FeaturePython)
  Dunit = g/cm3
  Dvalue = 1.7
  Group = -> [RAPHITE_POROUS]
  conduct = 2
  density = 1
  expand = 3
  formula = G4_GRAPHITE_POROUS
  name = G4_GRAPHITE_POROUS
  specific = 4
FEATURE [App::DocumentObjectGroupPython] H_element115  label="H_element : 0.150"  # scripted group (container) (typed FeaturePython)
  n = 0.080538
FEATURE [App::DocumentObjectGroupPython] C_element125  label="C_element : 0.600"  # scripted group (container) (typed FeaturePython)
  n = 0.599848
FEATURE [App::DocumentObjectGroupPython] O_element108  label="O_element : 0.320"  # scripted group (container) (typed FeaturePython)
  n = 0.319614
FEATURE [App::DocumentObjectGroupPython] G4_LUCITE  # scripted group (container) (typed FeaturePython)
  Dunit = g/cm3
  Dvalue = 1.19
  Group = -> [H_element115,C_element125,O_element108]
  conduct = 2
  density = 1
  expand = 3
  formula = G4_LUCITE
  name = G4_LUCITE
  specific = 4
FEATURE [App::DocumentObjectGroupPython] Cu_element002  label="Cu_element : 62"  # scripted group (container) (typed FeaturePython)
  n = 62
  ref = Cu_element
FEATURE [App::DocumentObjectGroupPython] Zn_element002  label="Zn_element : 35"  # scripted group (container) (typed FeaturePython)
  n = 35
  ref = Zn_element
FEATURE [App::DocumentObjectGroupPython] Pb_element005  label="Pb_element : 3"  # scripted group (container) (typed FeaturePython)
  n = 3
  ref = Pb_element
FEATURE [App::DocumentObjectGroupPython] G4_BRASS  # scripted group (container) (typed FeaturePython)
  Dunit = g/cm3
  Dvalue = 8.52
  Group = -> [Cu_element002,Zn_element002,Pb_element005]
  conduct = 2
  density = 1
  expand = 3
  formula = G4_BRASS
  name = G4_BRASS
  specific = 4
FEATURE [App::DocumentObjectGroupPython] Cu_element003  label="Cu_element : 89"  # scripted group (container) (typed FeaturePython)
  n = 89
  ref = Cu_element
FEATURE [App::DocumentObjectGroupPython] Zn_element003  label="Zn_element : 9"  # scripted group (container) (typed FeaturePython)
  n = 9
  ref = Zn_element
FEATURE [App::DocumentObjectGroupPython] Pb_element006  label="Pb_element : 2"  # scripted group (container) (typed FeaturePython)
  n = 2
  ref = Pb_element
FEATURE [App::DocumentObjectGroupPython] G4_BRONZE  # scripted group (container) (typed FeaturePython)
  Dunit = g/cm3
  Dvalue = 8.82
  Group = -> [Cu_element003,Zn_element003,Pb_element006]
  conduct = 2
  density = 1
  expand = 3
  formula = G4_BRONZE
  name = G4_BRONZE
  specific = 4
FEATURE [App::DocumentObjectGroupPython] Fe_element008  label="Fe_element : 74"  # scripted group (container) (typed FeaturePython)
  n = 74
  ref = Fe_element
FEATURE [App::DocumentObjectGroupPython] Cr_element002  label="Cr_element : 18"  # scripted group (container) (typed FeaturePython)
  n = 18
  ref = Cr_element
FEATURE [App::DocumentObjectGroupPython] Ni_element002  label="Ni_element : 8"  # scripted group (container) (typed FeaturePython)
  n = 8
  ref = Ni_element
FEATURE [App::DocumentObjectGroupPython] G4_STAINLESS_STEEL  label="G4_STAINLESS-STEEL"  # scripted group (container) (typed FeaturePython)
  Dunit = g/cm3
  Dvalue = 8
  Group = -> [Fe_element008,Cr_element002,Ni_element002]
  conduct = 2
  density = 1
  expand = 3
  formula = G4_STAINLESS-STEEL
  name = G4_STAINLESS-STEEL
  specific = 4
FEATURE [App::DocumentObjectGroupPython] H_element116  label="H_element : 064"  # scripted group (container) (typed FeaturePython)
  n = 18
  ref = H_element
FEATURE [App::DocumentObjectGroupPython] C_element126  label="C_element : 071"  # scripted group (container) (typed FeaturePython)
  n = 12
  ref = C_element
FEATURE [App::DocumentObjectGroupPython] O_element109  label="O_element : 062"  # scripted group (container) (typed FeaturePython)
  n = 7
  ref = O_element
FEATURE [App::DocumentObjectGroupPython] G4_CR39  # scripted group (container) (typed FeaturePython)
  Dunit = g/cm3
  Dvalue = 1.32
  Group = -> [H_element116,C_element126,O_element109]
  conduct = 2
  density = 1
  expand = 3
  formula = G4_CR39
  name = G4_CR39
  specific = 4
FEATURE [App::DocumentObjectGroupPython] H_element117  label="H_element : 38"  # scripted group (container) (typed FeaturePython)
  n = 38
  ref = H_element
FEATURE [App::DocumentObjectGroupPython] C_element127  label="C_element : 072"  # scripted group (container) (typed FeaturePython)
  n = 18
  ref = C_element
FEATURE [App::DocumentObjectGroupPython] O_element110  label="O_element : 063"  # scripted group (container) (typed FeaturePython)
  n = 1
  ref = O_element
FEATURE [App::DocumentObjectGroupPython] G4_OCTADECANOL  # scripted group (container) (typed FeaturePython)
  Dunit = g/cm3
  Dvalue = 0.812
  Group = -> [H_element117,C_element127,O_element110]
  conduct = 2
  density = 1
  expand = 3
  formula = G4_OCTADECANOL
  name = G4_OCTADECANOL
  specific = 4
FEATURE [App::DocumentObjectGroupPython] HEP  # scripted group (container) (typed FeaturePython)
  Group = -> [G4_lH2,G4_lN2,G4_lO2,G4_lAr,G4_lBr,G4_lKr,G4_lXe,G4_PbWO4,G4_Galactic,G4_GRAPHITE_POROUS,G4_LUCITE,G4_BRASS,G4_BRONZE,G4_STAINLESS_STEEL,G4_CR39,G4_OCTADECANOL]
FEATURE [App::DocumentObjectGroupPython] C_element128  label="C_element : 073"  # scripted group (container) (typed FeaturePython)
  n = 14
  ref = C_element
FEATURE [App::DocumentObjectGroupPython] H_element118  label="H_element : 065"  # scripted group (container) (typed FeaturePython)
  n = 10
  ref = H_element
FEATURE [App::DocumentObjectGroupPython] O_element111  label="O_element : 064"  # scripted group (container) (typed FeaturePython)
  n = 2
  ref = O_element
FEATURE [App::DocumentObjectGroupPython] N_element050  label="N_element : 023"  # scripted group (container) (typed FeaturePython)
  n = 2
  ref = N_element
FEATURE [App::DocumentObjectGroupPython] G4_KEVLAR  # scripted group (container) (typed FeaturePython)
  Dunit = g/cm3
  Dvalue = 1.44
  Group = -> [C_element128,H_element118,O_element111,N_element050]
  conduct = 2
  density = 1
  expand = 3
  formula = G4_KEVLAR
  name = G4_KEVLAR
  specific = 4
FEATURE [App::DocumentObjectGroupPython] C_element129  label="C_element : 074"  # scripted group (container) (typed FeaturePython)
  n = 10
  ref = C_element
FEATURE [App::DocumentObjectGroupPython] H_element119  label="H_element : 066"  # scripted group (container) (typed FeaturePython)
  n = 8
  ref = H_element
FEATURE [App::DocumentObjectGroupPython] O_element112  label="O_element : 065"  # scripted group (container) (typed FeaturePython)
  n = 4
  ref = O_element
FEATURE [App::DocumentObjectGroupPython] G4_DACRON  # scripted group (container) (typed FeaturePython)
  Dunit = g/cm3
  Dvalue = 1.4
  Group = -> [C_element129,H_element119,O_element112]
  conduct = 2
  density = 1
  expand = 3
  formula = G4_DACRON
  name = G4_DACRON
  specific = 4
FEATURE [App::DocumentObjectGroupPython] C_element130  label="C_element : 075"  # scripted group (container) (typed FeaturePython)
  n = 4
  ref = C_element
FEATURE [App::DocumentObjectGroupPython] H_element120  label="H_element : 067"  # scripted group (container) (typed FeaturePython)
  n = 5
  ref = H_element
FEATURE [App::DocumentObjectGroupPython] Cl_element030  label="Cl_element : 016"  # scripted group (container) (typed FeaturePython)
  n = 1
  ref = Cl_element
FEATURE [App::DocumentObjectGroupPython] G4_NEOPRENE  # scripted group (container) (typed FeaturePython)
  Dunit = g/cm3
  Dvalue = 1.23
  Group = -> [C_element130,H_element120,Cl_element030]
  conduct = 2
  density = 1
  expand = 3
  formula = G4_NEOPRENE
  name = G4_NEOPRENE
  specific = 4
FEATURE [App::DocumentObjectGroupPython] Space  # scripted group (container) (typed FeaturePython)
  Group = -> [G4_KEVLAR,G4_DACRON,G4_NEOPRENE]
FEATURE [App::DocumentObjectGroupPython] H_element121  label="H_element : 068"  # scripted group (container) (typed FeaturePython)
  n = 5
  ref = H_element
FEATURE [App::DocumentObjectGroupPython] C_element131  label="C_element : 076"  # scripted group (container) (typed FeaturePython)
  n = 4
  ref = C_element
FEATURE [App::DocumentObjectGroupPython] N_element051  label="N_element : 3"  # scripted group (container) (typed FeaturePython)
  n = 3
  ref = N_element
FEATURE [App::DocumentObjectGroupPython] O_element113  label="O_element : 066"  # scripted group (container) (typed FeaturePython)
  n = 1
  ref = O_element
FEATURE [App::DocumentObjectGroupPython] G4_CYTOSINE  # scripted group (container) (typed FeaturePython)
  Dunit = g/cm3
  Dvalue = 1.55
  Group = -> [H_element121,C_element131,N_element051,O_element113]
  conduct = 2
  density = 1
  expand = 3
  formula = G4_CYTOSINE
  name = G4_CYTOSINE
  specific = 4
FEATURE [App::DocumentObjectGroupPython] H_element122  label="H_element : 069"  # scripted group (container) (typed FeaturePython)
  n = 6
  ref = H_element
FEATURE [App::DocumentObjectGroupPython] C_element132  label="C_element : 077"  # scripted group (container) (typed FeaturePython)
  n = 5
  ref = C_element
FEATURE [App::DocumentObjectGroupPython] N_element052  label="N_element : 024"  # scripted group (container) (typed FeaturePython)
  n = 2
  ref = N_element
FEATURE [App::DocumentObjectGroupPython] O_element114  label="O_element : 067"  # scripted group (container) (typed FeaturePython)
  n = 2
  ref = O_element
FEATURE [App::DocumentObjectGroupPython] G4_THYMINE  # scripted group (container) (typed FeaturePython)
  Dunit = g/cm3
  Dvalue = 1.23
  Group = -> [H_element122,C_element132,N_element052,O_element114]
  conduct = 2
  density = 1
  expand = 3
  formula = G4_THYMINE
  name = G4_THYMINE
  specific = 4
FEATURE [App::DocumentObjectGroupPython] H_element123  label="H_element : 070"  # scripted group (container) (typed FeaturePython)
  n = 4
  ref = H_element
FEATURE [App::DocumentObjectGroupPython] C_element133  label="C_element : 078"  # scripted group (container) (typed FeaturePython)
  n = 4
  ref = C_element
FEATURE [App::DocumentObjectGroupPython] N_element053  label="N_element : 025"  # scripted group (container) (typed FeaturePython)
  n = 2
  ref = N_element
FEATURE [App::DocumentObjectGroupPython] O_element115  label="O_element : 068"  # scripted group (container) (typed FeaturePython)
  n = 2
  ref = O_element
FEATURE [App::DocumentObjectGroupPython] G4_URACIL  # scripted group (container) (typed FeaturePython)
  Dunit = g/cm3
  Dvalue = 1.32
  Group = -> [H_element123,C_element133,N_element053,O_element115]
  conduct = 2
  density = 1
  expand = 3
  formula = G4_URACIL
  name = G4_URACIL
  specific = 4
FEATURE [App::DocumentObjectGroupPython] H_element124  label="H_element : 071"  # scripted group (container) (typed FeaturePython)
  n = 4
  ref = H_element
FEATURE [App::DocumentObjectGroupPython] C_element134  label="C_element : 079"  # scripted group (container) (typed FeaturePython)
  n = 5
  ref = C_element
FEATURE [App::DocumentObjectGroupPython] N_element054  label="N_element : 026"  # scripted group (container) (typed FeaturePython)
  n = 5
  ref = N_element
FEATURE [App::DocumentObjectGroupPython] G4_DNA_ADENINE  # scripted group (container) (typed FeaturePython)
  Dunit = g/cm3
  Dvalue = 1
  Group = -> [H_element124,C_element134,N_element054]
  conduct = 2
  density = 1
  expand = 3
  formula = G4_DNA_ADENINE
  name = G4_DNA_ADENINE
  specific = 4
FEATURE [App::DocumentObjectGroupPython] H_element125  label="H_element : 072"  # scripted group (container) (typed FeaturePython)
  n = 4
  ref = H_element
FEATURE [App::DocumentObjectGroupPython] C_element135  label="C_element : 080"  # scripted group (container) (typed FeaturePython)
  n = 5
  ref = C_element
FEATURE [App::DocumentObjectGroupPython] N_element055  label="N_element : 027"  # scripted group (container) (typed FeaturePython)
  n = 5
  ref = N_element
FEATURE [App::DocumentObjectGroupPython] O_element116  label="O_element : 069"  # scripted group (container) (typed FeaturePython)
  n = 1
  ref = O_element
FEATURE [App::DocumentObjectGroupPython] G4_DNA_GUANINE  # scripted group (container) (typed FeaturePython)
  Dunit = g/cm3
  Dvalue = 1
  Group = -> [H_element125,C_element135,N_element055,O_element116]
  conduct = 2
  density = 1
  expand = 3
  formula = G4_DNA_GUANINE
  name = G4_DNA_GUANINE
  specific = 4
FEATURE [App::DocumentObjectGroupPython] H_element126  label="H_element : 073"  # scripted group (container) (typed FeaturePython)
  n = 4
  ref = H_element
FEATURE [App::DocumentObjectGroupPython] C_element136  label="C_element : 081"  # scripted group (container) (typed FeaturePython)
  n = 4
  ref = C_element
FEATURE [App::DocumentObjectGroupPython] N_element056  label="N_element : 028"  # scripted group (container) (typed FeaturePython)
  n = 3
  ref = N_element
FEATURE [App::DocumentObjectGroupPython] O_element117  label="O_element : 070"  # scripted group (container) (typed FeaturePython)
  n = 1
  ref = O_element
FEATURE [App::DocumentObjectGroupPython] G4_DNA_CYTOSINE  # scripted group (container) (typed FeaturePython)
  Dunit = g/cm3
  Dvalue = 1
  Group = -> [H_element126,C_element136,N_element056,O_element117]
  conduct = 2
  density = 1
  expand = 3
  formula = G4_DNA_CYTOSINE
  name = G4_DNA_CYTOSINE
  specific = 4
FEATURE [App::DocumentObjectGroupPython] H_element127  label="H_element : 074"  # scripted group (container) (typed FeaturePython)
  n = 5
  ref = H_element
FEATURE [App::DocumentObjectGroupPython] C_element137  label="C_element : 082"  # scripted group (container) (typed FeaturePython)
  n = 5
  ref = C_element
FEATURE [App::DocumentObjectGroupPython] N_element057  label="N_element : 029"  # scripted group (container) (typed FeaturePython)
  n = 2
  ref = N_element
FEATURE [App::DocumentObjectGroupPython] O_element118  label="O_element : 071"  # scripted group (container) (typed FeaturePython)
  n = 2
  ref = O_element
FEATURE [App::DocumentObjectGroupPython] G4_DNA_THYMINE  # scripted group (container) (typed FeaturePython)
  Dunit = g/cm3
  Dvalue = 1
  Group = -> [H_element127,C_element137,N_element057,O_element118]
  conduct = 2
  density = 1
  expand = 3
  formula = G4_DNA_THYMINE
  name = G4_DNA_THYMINE
  specific = 4
FEATURE [App::DocumentObjectGroupPython] H_element128  label="H_element : 075"  # scripted group (container) (typed FeaturePython)
  n = 3
  ref = H_element
FEATURE [App::DocumentObjectGroupPython] C_element138  label="C_element : 083"  # scripted group (container) (typed FeaturePython)
  n = 4
  ref = C_element
FEATURE [App::DocumentObjectGroupPython] N_element058  label="N_element : 030"  # scripted group (container) (typed FeaturePython)
  n = 2
  ref = N_element
FEATURE [App::DocumentObjectGroupPython] O_element119  label="O_element : 072"  # scripted group (container) (typed FeaturePython)
  n = 2
  ref = O_element
FEATURE [App::DocumentObjectGroupPython] G4_DNA_URACIL  # scripted group (container) (typed FeaturePython)
  Dunit = g/cm3
  Dvalue = 1
  Group = -> [H_element128,C_element138,N_element058,O_element119]
  conduct = 2
  density = 1
  expand = 3
  formula = G4_DNA_URACIL
  name = G4_DNA_URACIL
  specific = 4
FEATURE [App::DocumentObjectGroupPython] H_element129  label="H_element : 076"  # scripted group (container) (typed FeaturePython)
  n = 10
  ref = H_element
FEATURE [App::DocumentObjectGroupPython] C_element139  label="C_element : 084"  # scripted group (container) (typed FeaturePython)
  n = 10
  ref = C_element
FEATURE [App::DocumentObjectGroupPython] N_element059  label="N_element : 031"  # scripted group (container) (typed FeaturePython)
  n = 5
  ref = N_element
FEATURE [App::DocumentObjectGroupPython] O_element120  label="O_element : 073"  # scripted group (container) (typed FeaturePython)
  n = 4
  ref = O_element
FEATURE [App::DocumentObjectGroupPython] G4_DNA_ADENOSINE  # scripted group (container) (typed FeaturePython)
  Dunit = g/cm3
  Dvalue = 1
  Group = -> [H_element129,C_element139,N_element059,O_element120]
  conduct = 2
  density = 1
  expand = 3
  formula = G4_DNA_ADENOSINE
  name = G4_DNA_ADENOSINE
  specific = 4
FEATURE [App::DocumentObjectGroupPython] H_element130  label="H_element : 077"  # scripted group (container) (typed FeaturePython)
  n = 10
  ref = H_element
FEATURE [App::DocumentObjectGroupPython] C_element140  label="C_element : 085"  # scripted group (container) (typed FeaturePython)
  n = 10
  ref = C_element
FEATURE [App::DocumentObjectGroupPython] N_element060  label="N_element : 032"  # scripted group (container) (typed FeaturePython)
  n = 5
  ref = N_element
FEATURE [App::DocumentObjectGroupPython] O_element121  label="O_element : 074"  # scripted group (container) (typed FeaturePython)
  n = 5
  ref = O_element
FEATURE [App::DocumentObjectGroupPython] G4_DNA_GUANOSINE  # scripted group (container) (typed FeaturePython)
  Dunit = g/cm3
  Dvalue = 1
  Group = -> [H_element130,C_element140,N_element060,O_element121]
  conduct = 2
  density = 1
  expand = 3
  formula = G4_DNA_GUANOSINE
  name = G4_DNA_GUANOSINE
  specific = 4
FEATURE [App::DocumentObjectGroupPython] H_element131  label="H_element : 078"  # scripted group (container) (typed FeaturePython)
  n = 10
  ref = H_element
FEATURE [App::DocumentObjectGroupPython] C_element141  label="C_element : 086"  # scripted group (container) (typed FeaturePython)
  n = 9
  ref = C_element
FEATURE [App::DocumentObjectGroupPython] N_element061  label="N_element : 033"  # scripted group (container) (typed FeaturePython)
  n = 3
  ref = N_element
FEATURE [App::DocumentObjectGroupPython] O_element122  label="O_element : 075"  # scripted group (container) (typed FeaturePython)
  n = 5
  ref = O_element
FEATURE [App::DocumentObjectGroupPython] G4_DNA_CYTIDINE  # scripted group (container) (typed FeaturePython)
  Dunit = g/cm3
  Dvalue = 1
  Group = -> [H_element131,C_element141,N_element061,O_element122]
  conduct = 2
  density = 1
  expand = 3
  formula = G4_DNA_CYTIDINE
  name = G4_DNA_CYTIDINE
  specific = 4
FEATURE [App::DocumentObjectGroupPython] H_element132  label="H_element : 079"  # scripted group (container) (typed FeaturePython)
  n = 9
  ref = H_element
FEATURE [App::DocumentObjectGroupPython] C_element142  label="C_element : 087"  # scripted group (container) (typed FeaturePython)
  n = 9
  ref = C_element
FEATURE [App::DocumentObjectGroupPython] N_element062  label="N_element : 034"  # scripted group (container) (typed FeaturePython)
  n = 2
  ref = N_element
FEATURE [App::DocumentObjectGroupPython] O_element123  label="O_element : 076"  # scripted group (container) (typed FeaturePython)
  n = 6
  ref = O_element
FEATURE [App::DocumentObjectGroupPython] G4_DNA_URIDINE  # scripted group (container) (typed FeaturePython)
  Dunit = g/cm3
  Dvalue = 1
  Group = -> [H_element132,C_element142,N_element062,O_element123]
  conduct = 2
  density = 1
  expand = 3
  formula = G4_DNA_URIDINE
  name = G4_DNA_URIDINE
  specific = 4
FEATURE [App::DocumentObjectGroupPython] H_element133  label="H_element : 080"  # scripted group (container) (typed FeaturePython)
  n = 11
  ref = H_element
FEATURE [App::DocumentObjectGroupPython] C_element143  label="C_element : 088"  # scripted group (container) (typed FeaturePython)
  n = 10
  ref = C_element
FEATURE [App::DocumentObjectGroupPython] N_element063  label="N_element : 035"  # scripted group (container) (typed FeaturePython)
  n = 2
  ref = N_element
FEATURE [App::DocumentObjectGroupPython] O_element124  label="O_element : 077"  # scripted group (container) (typed FeaturePython)
  n = 6
  ref = O_element
FEATURE [App::DocumentObjectGroupPython] G4_DNA_METHYLURIDINE  # scripted group (container) (typed FeaturePython)
  Dunit = g/cm3
  Dvalue = 1
  Group = -> [H_element133,C_element143,N_element063,O_element124]
  conduct = 2
  density = 1
  expand = 3
  formula = G4_DNA_METHYLURIDINE
  name = G4_DNA_METHYLURIDINE
  specific = 4
FEATURE [App::DocumentObjectGroupPython] P_element014  label="P_element : 003"  # scripted group (container) (typed FeaturePython)
  n = 1
  ref = P_element
FEATURE [App::DocumentObjectGroupPython] O_element125  label="O_element : 078"  # scripted group (container) (typed FeaturePython)
  n = 3
  ref = O_element
FEATURE [App::DocumentObjectGroupPython] G4_DNA_MONOPHOSPHATE  # scripted group (container) (typed FeaturePython)
  Dunit = g/cm3
  Dvalue = 1
  Group = -> [P_element014,O_element125]
  conduct = 2
  density = 1
  expand = 3
  formula = G4_DNA_MONOPHOSPHATE
  name = G4_DNA_MONOPHOSPHATE
  specific = 4
FEATURE [App::DocumentObjectGroupPython] H_element134  label="H_element : 081"  # scripted group (container) (typed FeaturePython)
  n = 10
  ref = H_element
FEATURE [App::DocumentObjectGroupPython] C_element144  label="C_element : 089"  # scripted group (container) (typed FeaturePython)
  n = 10
  ref = C_element
FEATURE [App::DocumentObjectGroupPython] N_element064  label="N_element : 036"  # scripted group (container) (typed FeaturePython)
  n = 5
  ref = N_element
FEATURE [App::DocumentObjectGroupPython] O_element126  label="O_element : 079"  # scripted group (container) (typed FeaturePython)
  n = 7
  ref = O_element
FEATURE [App::DocumentObjectGroupPython] P_element015  label="P_element : 004"  # scripted group (container) (typed FeaturePython)
  n = 1
  ref = P_element
FEATURE [App::DocumentObjectGroupPython] G4_DNA_A  # scripted group (container) (typed FeaturePython)
  Dunit = g/cm3
  Dvalue = 1
  Group = -> [H_element134,C_element144,N_element064,O_element126,P_element015]
  conduct = 2
  density = 1
  expand = 3
  formula = G4_DNA_A
  name = G4_DNA_A
  specific = 4
FEATURE [App::DocumentObjectGroupPython] H_element135  label="H_element : 082"  # scripted group (container) (typed FeaturePython)
  n = 10
  ref = H_element
FEATURE [App::DocumentObjectGroupPython] C_element145  label="C_element : 090"  # scripted group (container) (typed FeaturePython)
  n = 10
  ref = C_element
FEATURE [App::DocumentObjectGroupPython] N_element065  label="N_element : 037"  # scripted group (container) (typed FeaturePython)
  n = 5
  ref = N_element
FEATURE [App::DocumentObjectGroupPython] O_element127  label="O_element : 8"  # scripted group (container) (typed FeaturePython)
  n = 8
  ref = O_element
FEATURE [App::DocumentObjectGroupPython] P_element016  label="P_element : 005"  # scripted group (container) (typed FeaturePython)
  n = 1
  ref = P_element
FEATURE [App::DocumentObjectGroupPython] G4_DNA_G  # scripted group (container) (typed FeaturePython)
  Dunit = g/cm3
  Dvalue = 1
  Group = -> [H_element135,C_element145,N_element065,O_element127,P_element016]
  conduct = 2
  density = 1
  expand = 3
  formula = G4_DNA_G
  name = G4_DNA_G
  specific = 4
FEATURE [App::DocumentObjectGroupPython] H_element136  label="H_element : 083"  # scripted group (container) (typed FeaturePython)
  n = 10
  ref = H_element
FEATURE [App::DocumentObjectGroupPython] C_element146  label="C_element : 091"  # scripted group (container) (typed FeaturePython)
  n = 9
  ref = C_element
FEATURE [App::DocumentObjectGroupPython] N_element066  label="N_element : 038"  # scripted group (container) (typed FeaturePython)
  n = 3
  ref = N_element
FEATURE [App::DocumentObjectGroupPython] O_element128  label="O_element : 080"  # scripted group (container) (typed FeaturePython)
  n = 8
  ref = O_element
FEATURE [App::DocumentObjectGroupPython] P_element017  label="P_element : 006"  # scripted group (container) (typed FeaturePython)
  n = 1
  ref = P_element
FEATURE [App::DocumentObjectGroupPython] G4_DNA_C  # scripted group (container) (typed FeaturePython)
  Dunit = g/cm3
  Dvalue = 1
  Group = -> [H_element136,C_element146,N_element066,O_element128,P_element017]
  conduct = 2
  density = 1
  expand = 3
  formula = G4_DNA_C
  name = G4_DNA_C
  specific = 4
FEATURE [App::DocumentObjectGroupPython] H_element137  label="H_element : 084"  # scripted group (container) (typed FeaturePython)
  n = 9
  ref = H_element
FEATURE [App::DocumentObjectGroupPython] C_element147  label="C_element : 092"  # scripted group (container) (typed FeaturePython)
  n = 9
  ref = C_element
FEATURE [App::DocumentObjectGroupPython] N_element067  label="N_element : 039"  # scripted group (container) (typed FeaturePython)
  n = 2
  ref = N_element
FEATURE [App::DocumentObjectGroupPython] O_element129  label="O_element : 9"  # scripted group (container) (typed FeaturePython)
  n = 9
  ref = O_element
FEATURE [App::DocumentObjectGroupPython] P_element018  label="P_element : 007"  # scripted group (container) (typed FeaturePython)
  n = 1
  ref = P_element
FEATURE [App::DocumentObjectGroupPython] G4_DNA_U  # scripted group (container) (typed FeaturePython)
  Dunit = g/cm3
  Dvalue = 1
  Group = -> [H_element137,C_element147,N_element067,O_element129,P_element018]
  conduct = 2
  density = 1
  expand = 3
  formula = G4_DNA_U
  name = G4_DNA_U
  specific = 4
FEATURE [App::DocumentObjectGroupPython] H_element138  label="H_element : 085"  # scripted group (container) (typed FeaturePython)
  n = 11
  ref = H_element
FEATURE [App::DocumentObjectGroupPython] C_element148  label="C_element : 093"  # scripted group (container) (typed FeaturePython)
  n = 10
  ref = C_element
FEATURE [App::DocumentObjectGroupPython] N_element068  label="N_element : 040"  # scripted group (container) (typed FeaturePython)
  n = 2
  ref = N_element
FEATURE [App::DocumentObjectGroupPython] O_element130  label="O_element : 081"  # scripted group (container) (typed FeaturePython)
  n = 9
  ref = O_element
FEATURE [App::DocumentObjectGroupPython] P_element019  label="P_element : 008"  # scripted group (container) (typed FeaturePython)
  n = 1
  ref = P_element
FEATURE [App::DocumentObjectGroupPython] G4_DNA_MU  # scripted group (container) (typed FeaturePython)
  Dunit = g/cm3
  Dvalue = 1
  Group = -> [H_element138,C_element148,N_element068,O_element130,P_element019]
  conduct = 2
  density = 1
  expand = 3
  formula = G4_DNA_MU
  name = G4_DNA_MU
  specific = 4
FEATURE [App::DocumentObjectGroupPython] BioChemical  # scripted group (container) (typed FeaturePython)
  Group = -> [G4_CYTOSINE,G4_THYMINE,G4_URACIL,G4_DNA_ADENINE,G4_DNA_GUANINE,G4_DNA_CYTOSINE,G4_DNA_THYMINE,G4_DNA_URACIL,G4_DNA_ADENOSINE,G4_DNA_GUANOSINE,G4_DNA_CYTIDINE,G4_DNA_URIDINE,G4_DNA_METHYLURIDINE,G4_DNA_MONOPHOSPHATE,G4_DNA_A,G4_DNA_G,G4_DNA_C,G4_DNA_U,G4_DNA_MU]
FEATURE [App::DocumentObjectGroupPython] G4Materials  # scripted group (container) (typed FeaturePython)
  Group = -> [NIST,Element,HEP,Space,BioChemical]
  version = 1
FEATURE [App::DocumentObjectGroupPython] Geant4  # scripted group (container) (typed FeaturePython)
  Group = -> [G4Isotopes,G4Elements,G4Materials]
FEATURE [App::DocumentObjectGroupPython] Materials  # scripted group (container) (typed FeaturePython)
  Group = -> [Geant4]
FEATURE [Part::FeaturePython] GDMLBox_WorldBox  # WARN: FeaturePython — macro-defined, semantics opaque (R4)
  lunit = 2
  material = 5
  x = 200
  y = 200
  z = 200
FEATURE [Sketcher::SketchObject] Sketch
  ArcFitTolerance = 0
  FullyConstrained = false
  MakeInternals = false
  sketch-geometry (36):
    g0: ArcOfParabola CenterX=18.1274 CenterY=-16.2535 CenterZ=0 NormalX=0 NormalY=0 NormalZ=1 Focal=8.09223 AngleXU=-3.10749 StartAngle=-21.4534 EndAngle=19.9625
    g1: GeomPoint [constr] X=10.0399 Y=-16.5294 Z=0
    g2: LineSegment [constr] StartX=18.1274 StartY=-16.2535 StartZ=0 EndX=10.0399 EndY=-16.5294 EndZ=0
    g3: ArcOfCircle CenterX=-6.88152 CenterY=-4.99689 CenterZ=0 NormalX=0 NormalY=0 NormalZ=1 AngleXU=0 Radius=13.9794 StartAngle=2.38084 EndAngle=7.05
    g4: ArcOfEllipse CenterX=-7.78764 CenterY=-33.8957 CenterZ=0 NormalX=0 NormalY=0 NormalZ=1 MajorRadius=18.086 MinorRadius=7.91522 AngleXU=-0.556234 StartAngle=4.96298 EndAngle=7.00481
    g5: LineSegment [constr] StartX=7.57186 StartY=-43.4449 StartZ=0 EndX=-23.1471 EndY=-24.3464 EndZ=0
    g6: LineSegment [constr] StartX=-3.60847 StartY=-27.1737 StartZ=0 EndX=-11.9668 EndY=-40.6177 EndZ=0
    g7: GeomPoint [constr] X=6.02282 Y=-42.4819 Z=0
    g8: GeomPoint [constr] X=-21.5981 Y=-25.3095 Z=0
    g9-g16: Circle [constr] x8 (B-spline internal-alignment scaffolding for g17; pole/knot coordinates omitted)
    g17: BSplineCurve PolesCount=8 KnotsCount=6 Degree=3 IsPeriodic=0
    g18-g23: GeomPoint [constr] x6 (B-spline internal-alignment scaffolding for g17; pole/knot coordinates omitted)
    g24: LineSegment StartX=-41.714 StartY=-18.5032 StartZ=0 EndX=-43.2734 EndY=-9.67993 EndZ=0
    g25: LineSegment StartX=-35.6082 StartY=7.90793 StartZ=0 EndX=-17.007 EndY=4.64145 EndZ=0
    g26: Circle CenterX=-9.18911 CenterY=-31.0442 CenterZ=0 NormalX=0 NormalY=0 NormalZ=1 AngleXU=0 Radius=8.40034
    g27: ArcOfHyperbola CenterX=-68.367 CenterY=18.2732 CenterZ=0 NormalX=0 NormalY=0 NormalZ=1 MajorRadius=22.1156 MinorRadius=7.852 AngleXU=-0.565391 StartAngle=-1.07469 EndAngle=0.964065
    g28: LineSegment [constr] StartX=-49.6931 StartY=6.4249 StartZ=0 EndX=-87.0409 EndY=30.1216 EndZ=0
    g29: LineSegment [constr] StartX=-45.4864 StartY=13.055 StartZ=0 EndX=-53.8998 EndY=-0.205161 EndZ=0
    g30: GeomPoint [constr] X=-48.551 Y=5.70028 Z=0
    g31: Ellipse CenterX=-34.2322 CenterY=-6.26645 CenterZ=0 NormalX=0 NormalY=0 NormalZ=1 MajorRadius=7.12528 MinorRadius=4.84017 AngleXU=-0.84953
    g32: LineSegment [constr] StartX=-29.5272 StartY=-11.6173 StartZ=0 EndX=-38.9373 EndY=-0.915575 EndZ=0
    g33: LineSegment [constr] StartX=-30.5974 StartY=-3.07031 StartZ=0 EndX=-37.8671 EndY=-9.46258 EndZ=0
    g34: GeomPoint [constr] X=-30.7794 Y=-10.1933 Z=0
    g35: GeomPoint [constr] X=-37.6851 Y=-2.33963 Z=0
  constraints (18):
    c: InternalAlignment(g1,g0)
    c: InternalAlignment(g2,g0)
    c: Coincident(g3,g0)
    c: InternalAlignment(g5-g8 -> g4) x4
    c: Coincident(g4,g0)
    c: Coincident(g17,g4)
    c: Weight(g9) = 1
    c: Equal(g9, g10-g16) x7
    c: InternalAlignment(g9-g16 -> g17) x8
    c: InternalAlignment(g18-g23 -> g17) x6
    c: Coincident(g24,g17)
    c: Coincident(g25,g3)
    c: InternalAlignment(g28,g27)
    c: InternalAlignment(g29,g27)
    c: InternalAlignment(g30,g27)
    c: Coincident(g24,g27)
    c: Coincident(g25,g27)
    c: InternalAlignment(g32-g35 -> g31) x4
FEATURE [Part::Extrusion] Extrude
  Base = -> Sketch
  Dir = (0,0,1)
  DirMode = 2
  FaceMakerClass = Part::FaceMakerBullseye
  FaceMakerMode = 3
  LengthFwd = 10
  LengthRev = 0
  Solid = true
  Symmetric = false
FEATURE [App::Part] Part
  Group = -> [Sketch,Extrude]
  Origin = -> Origin001
  material = 5
FEATURE [App::Part] worldVOL
  Group = -> [GDMLBox_WorldBox,Part]
  Origin = -> Origin
